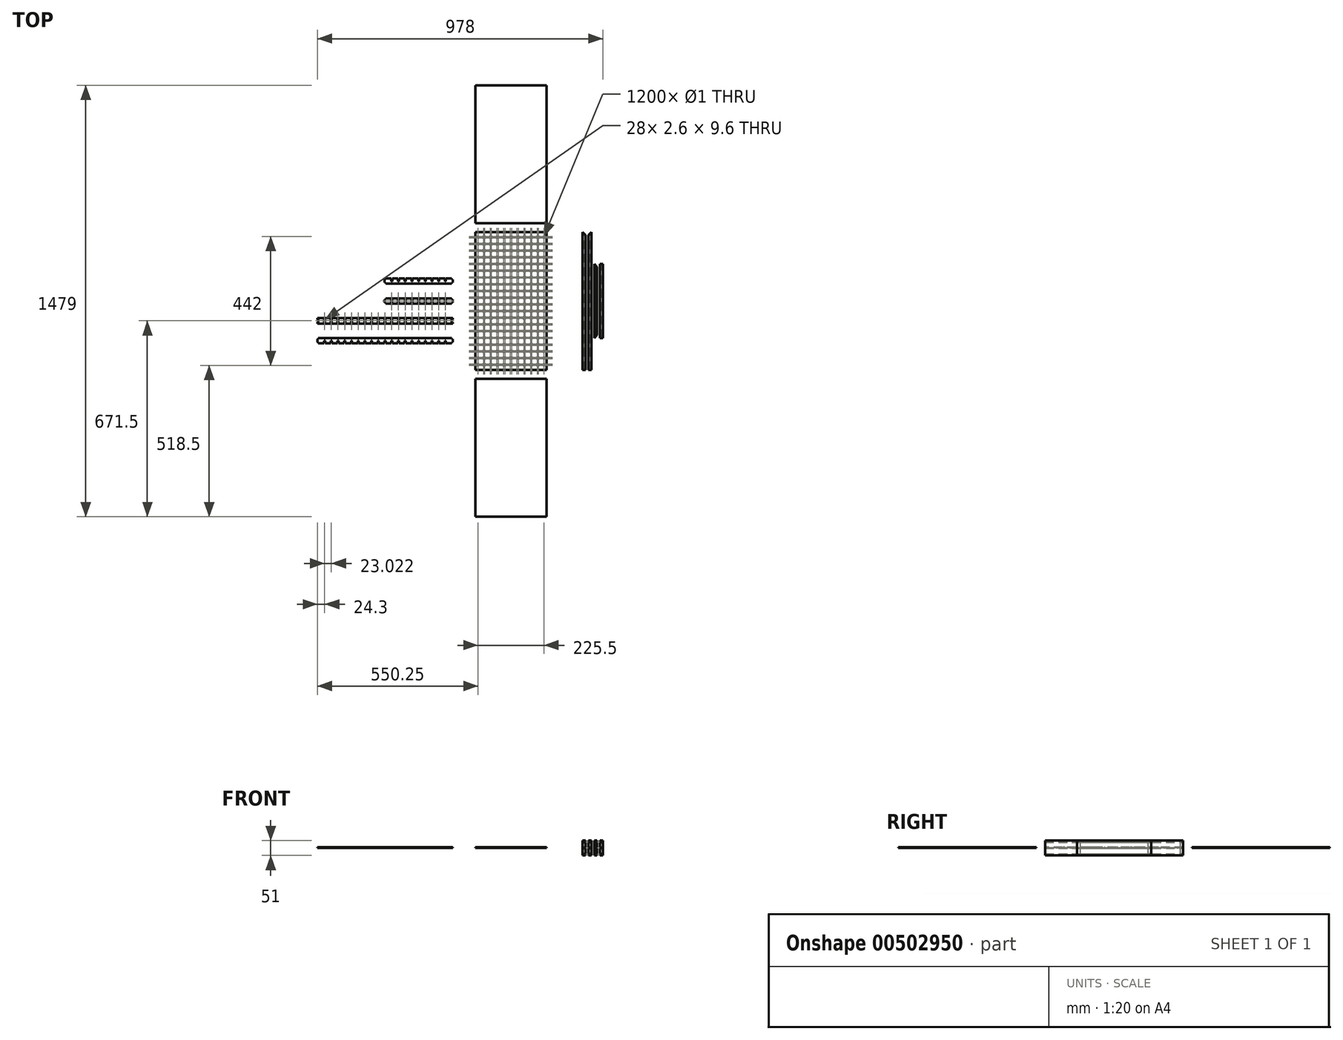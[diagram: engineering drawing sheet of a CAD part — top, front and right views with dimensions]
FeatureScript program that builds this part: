
annotation { "Feature Type Name" : "Feature", "Feature Type Description" : "" }
export const myFeature = defineFeature(function(context is Context, id is Id, definition is map)
    precondition{}
    {
        {
            assignVariable(context, id + "F0", {"name" : "Board_Size", "anyValue" : 10});
        }
        {
            assignVariable(context, id + "F1", {"name" : "Thickness", "anyValue" : 3});
        }
        {
            assignVariable(context, id + "F2", {"name" : "LED_Space", "anyValue" : 20});
        }
        {
            assignVariable(context, id + "F3", {"name" : "Gap_Fit", "anyValue" : 5});
        }
        {
            assignVariable(context, id + "F4", {"name" : "LED_Width", "anyValue" : (getVariable(context, 'Gap_Fit') * 2 + 10 * getVariable(context, 'LED_Space') + 11 * getVariable(context, 'Thickness'))});
        }
        {
            assignVariable(context, id + "F5", {"name" : "LED_Height", "anyValue" : (getVariable(context, 'Gap_Fit') * 2 + 20 * getVariable(context, 'LED_Space') + 21 * getVariable(context, 'Thickness'))});
        }
        {
            var Q0;
            Q0=qCreatedBy(makeId("Front.planeOp"),FACE);
            var sketch = newSketch(context, id + "F6", { "sketchPlane" : qUnion([Q0])});
            skLineSegment(sketch, "E0", {"start": v(5, 25.5) * mm, "end": v(-5, 25.5) * mm});
            skLineSegment(sketch, "E1", {"start": v(-5, 25.5) * mm, "end": v(-5, -25.5) * mm});
            skLineSegment(sketch, "E2", {"start": v(-5, -25.5) * mm, "end": v(5, -25.5) * mm});
            skLineSegment(sketch, "E3", {"start": v(5, -25.5) * mm, "end": v(5, -22.5) * mm});
            skLineSegment(sketch, "E4", {"start": v(5, -22.5) * mm, "end": v(0, -22.5) * mm});
            skLineSegment(sketch, "E5", {"start": v(0, -22.5) * mm, "end": v(0, -19.5) * mm});
            skLineSegment(sketch, "E6", {"start": v(0, -19.5) * mm, "end": v(5, -19.5) * mm});
            skLineSegment(sketch, "E7", {"start": v(5, -19.5) * mm, "end": v(5, -1.5) * mm});
            skLineSegment(sketch, "E8", {"start": v(5, -1.5) * mm, "end": v(0, -1.5) * mm});
            skLineSegment(sketch, "E9", {"start": v(0, -1.5) * mm, "end": v(0, 1.5) * mm});
            skLineSegment(sketch, "E10", {"start": v(0, 1.5) * mm, "end": v(5, 1.5) * mm});
            skLineSegment(sketch, "E11", {"start": v(5, 1.5) * mm, "end": v(5, 19.5) * mm});
            skLineSegment(sketch, "E12", {"start": v(5, 19.5) * mm, "end": v(0, 19.5) * mm});
            skLineSegment(sketch, "E13", {"start": v(0, 19.5) * mm, "end": v(0, 22.5) * mm});
            skLineSegment(sketch, "E14", {"start": v(0, 22.5) * mm, "end": v(5, 22.5) * mm});
            skLineSegment(sketch, "E15", {"start": v(5, 22.5) * mm, "end": v(5, 25.5) * mm});
            skSolve(sketch);
        }
        {
            var Q0;
            Q0=makeQuery(id+"F6.imprint","IMPRINT",FACE,{"disambiguationData":[TD([[makeQuery(id+"F6.imprint","IMPRINT",EDGE,{"derivedFrom":sQuery(id+"F6.wireOp",EDGE,"E0")}),1.0]])]});
            extrude(context, id + "F7", {"entities" : qUnion([Q0]), "endBound" : BoundingType.SYMMETRIC, "depth" : (getVariable(context, 'LED_Height')) * mm, "offsetDistance" : 25 * mm});
        }
        {
            var Q0;
            Q0=makeQuery(id+"F7.opExtrude","CAP_EDGE",EDGE,{"disambiguationData":[OSD([sQuery(id+"F6.wireOp",EDGE,"E11")])],"isStart":true});
            var Q1;
            Q1=makeQuery(id+"F7.opExtrude","CAP_EDGE",EDGE,{"disambiguationData":[OSD([sQuery(id+"F6.wireOp",EDGE,"E15")])],"isStart":true});
            var Q2;
            Q2=makeQuery(id+"F7.opExtrude","CAP_EDGE",EDGE,{"disambiguationData":[OSD([sQuery(id+"F6.wireOp",EDGE,"E7")])],"isStart":true});
            var Q3;
            Q3=makeQuery(id+"F7.opExtrude","CAP_EDGE",EDGE,{"disambiguationData":[OSD([sQuery(id+"F6.wireOp",EDGE,"E3")])],"isStart":true});
            chamfer(context, id + "F8", {"entities" : qUnion([Q0, Q1, Q2, Q3]), "width" : (getVariable(context, 'Board_Size')) * mm, "tangentPropagation" : true});
        }
        {
            var Q0;
            Q0=qCreatedBy(makeId("Front.planeOp"),FACE);
            var sketch = newSketch(context, id + "F9", { "sketchPlane" : qUnion([Q0])});
            skLineSegment(sketch, "E16", {"start": v(10, 50) * mm, "end": v(10, -50) * mm, "construction": true});
            skPoint(sketch, "E17", {"position": v(10, 0) * mm});
            skLineSegment(sketch, "E18", {"start": v(-5, 25.5) * mm, "end": v(5, 25.5) * mm, "construction": true});
            skLineSegment(sketch, "E19", {"start": v(5, 25.5) * mm, "end": v(5, 22.5) * mm, "construction": true});
            skLineSegment(sketch, "E20", {"start": v(5, 22.5) * mm, "end": v(0, 22.5) * mm, "construction": true});
            skLineSegment(sketch, "E21", {"start": v(0, 22.5) * mm, "end": v(0, 19.5) * mm, "construction": true});
            skLineSegment(sketch, "E22", {"start": v(0, 19.5) * mm, "end": v(5, 19.5) * mm, "construction": true});
            skLineSegment(sketch, "E23", {"start": v(5, 19.5) * mm, "end": v(5, 1.5) * mm, "construction": true});
            skLineSegment(sketch, "E24", {"start": v(5, -1.5) * mm, "end": v(5, -19.5) * mm, "construction": true});
            skLineSegment(sketch, "E25", {"start": v(5, 1.5) * mm, "end": v(0, 1.5) * mm, "construction": true});
            skLineSegment(sketch, "E26", {"start": v(0, 1.5) * mm, "end": v(0, -1.5) * mm, "construction": true});
            skLineSegment(sketch, "E27", {"start": v(0, -1.5) * mm, "end": v(5, -1.5) * mm, "construction": true});
            skLineSegment(sketch, "E28", {"start": v(0, -19.5) * mm, "end": v(0, -22.5) * mm, "construction": true});
            skLineSegment(sketch, "E29", {"start": v(5, -19.5) * mm, "end": v(0, -19.5) * mm, "construction": true});
            skLineSegment(sketch, "E30", {"start": v(0, -22.5) * mm, "end": v(5, -22.5) * mm, "construction": true});
            skLineSegment(sketch, "E31", {"start": v(5, -22.5) * mm, "end": v(5, -25.5) * mm, "construction": true});
            skLineSegment(sketch, "E32", {"start": v(5, -25.5) * mm, "end": v(-5, -25.5) * mm, "construction": true});
            skLineSegment(sketch, "E33", {"start": v(-5, -25.5) * mm, "end": v(-5, 25.5) * mm, "construction": true});
            skLineSegment(sketch, "E34.MirrorCS", {"start": v(15, 25.5) * mm, "end": v(15, 22.5) * mm});
            skLineSegment(sketch, "E35.MirrorCS", {"start": v(20, 22.5) * mm, "end": v(20, 19.5) * mm});
            skLineSegment(sketch, "E36.MirrorCS", {"start": v(20, 1.5) * mm, "end": v(20, -1.5) * mm});
            skLineSegment(sketch, "E37.MirrorCS", {"start": v(20, -19.5) * mm, "end": v(20, -22.5) * mm});
            skLineSegment(sketch, "E38.MirrorCS", {"start": v(15, -22.5) * mm, "end": v(15, -25.5) * mm});
            skLineSegment(sketch, "E39.MirrorCS", {"start": v(20, -22.5) * mm, "end": v(15, -22.5) * mm});
            skLineSegment(sketch, "E40.MirrorCS", {"start": v(15, 22.5) * mm, "end": v(20, 22.5) * mm});
            skLineSegment(sketch, "E41.MirrorCS", {"start": v(15, -25.5) * mm, "end": v(25, -25.5) * mm});
            skLineSegment(sketch, "E42.MirrorCS", {"start": v(15, 1.5) * mm, "end": v(20, 1.5) * mm});
            skLineSegment(sketch, "E43.MirrorCS", {"start": v(20, -1.5) * mm, "end": v(15, -1.5) * mm});
            skLineSegment(sketch, "E44.MirrorCS", {"start": v(15, -1.5) * mm, "end": v(15, -19.5) * mm});
            skLineSegment(sketch, "E45.MirrorCS", {"start": v(15, 19.5) * mm, "end": v(15, 1.5) * mm});
            skLineSegment(sketch, "E46.MirrorCS", {"start": v(15, -19.5) * mm, "end": v(20, -19.5) * mm});
            skLineSegment(sketch, "E47.MirrorCS", {"start": v(20, 19.5) * mm, "end": v(15, 19.5) * mm});
            skLineSegment(sketch, "E48.MirrorCS", {"start": v(25, -25.5) * mm, "end": v(25, 25.5) * mm});
            skLineSegment(sketch, "E49.MirrorCS", {"start": v(25, 25.5) * mm, "end": v(15, 25.5) * mm});
            skLineSegment(sketch, "E50", {"start": v(30, 50) * mm, "end": v(30, -50) * mm, "construction": true});
            skLineSegment(sketch, "E51.MirrorCS", {"start": v(45, -22.5) * mm, "end": v(45, -25.5) * mm});
            skLineSegment(sketch, "E52.MirrorCS", {"start": v(40, -19.5) * mm, "end": v(40, -22.5) * mm});
            skLineSegment(sketch, "E53.MirrorCS", {"start": v(45, -19.5) * mm, "end": v(40, -19.5) * mm});
            skLineSegment(sketch, "E54.MirrorCS", {"start": v(45, 1.5) * mm, "end": v(40, 1.5) * mm});
            skLineSegment(sketch, "E55.MirrorCS", {"start": v(35, 25.5) * mm, "end": v(45, 25.5) * mm});
            skLineSegment(sketch, "E56.MirrorCS", {"start": v(40, 1.5) * mm, "end": v(40, -1.5) * mm});
            skLineSegment(sketch, "E57.MirrorCS", {"start": v(40, 19.5) * mm, "end": v(45, 19.5) * mm});
            skLineSegment(sketch, "E58.MirrorCS", {"start": v(45, -25.5) * mm, "end": v(35, -25.5) * mm});
            skLineSegment(sketch, "E59.MirrorCS", {"start": v(40, 22.5) * mm, "end": v(40, 19.5) * mm});
            skLineSegment(sketch, "E60.MirrorCS", {"start": v(40, -1.5) * mm, "end": v(45, -1.5) * mm});
            skLineSegment(sketch, "E61.MirrorCS", {"start": v(40, -22.5) * mm, "end": v(45, -22.5) * mm});
            skLineSegment(sketch, "E62.MirrorCS", {"start": v(45, 22.5) * mm, "end": v(40, 22.5) * mm});
            skLineSegment(sketch, "E63.MirrorCS", {"start": v(45, 25.5) * mm, "end": v(45, 22.5) * mm});
            skLineSegment(sketch, "E64.MirrorCS", {"start": v(35, -25.5) * mm, "end": v(35, 25.5) * mm});
            skLineSegment(sketch, "E65.MirrorCS", {"start": v(45, -1.5) * mm, "end": v(45, -19.5) * mm});
            skLineSegment(sketch, "E66.MirrorCS", {"start": v(45, 19.5) * mm, "end": v(45, 1.5) * mm});
            skLineSegment(sketch, "E67.MirrorCS", {"start": v(55, -22.5) * mm, "end": v(55, -25.5) * mm});
            skLineSegment(sketch, "E68.MirrorCS", {"start": v(55, -19.5) * mm, "end": v(60, -19.5) * mm});
            skLineSegment(sketch, "E69.MirrorCS", {"start": v(60, 1.5) * mm, "end": v(60, -1.5) * mm});
            skLineSegment(sketch, "E70.MirrorCS", {"start": v(60, 19.5) * mm, "end": v(55, 19.5) * mm});
            skLineSegment(sketch, "E71.MirrorCS", {"start": v(60, 22.5) * mm, "end": v(60, 19.5) * mm});
            skLineSegment(sketch, "E72.MirrorCS", {"start": v(55, 22.5) * mm, "end": v(60, 22.5) * mm});
            skLineSegment(sketch, "E73.MirrorCS", {"start": v(55, 25.5) * mm, "end": v(55, 22.5) * mm});
            skLineSegment(sketch, "E74.MirrorCS", {"start": v(55, 1.5) * mm, "end": v(60, 1.5) * mm});
            skLineSegment(sketch, "E75.MirrorCS", {"start": v(60, -1.5) * mm, "end": v(55, -1.5) * mm});
            skLineSegment(sketch, "E76.MirrorCS", {"start": v(60, -19.5) * mm, "end": v(60, -22.5) * mm});
            skLineSegment(sketch, "E77.MirrorCS", {"start": v(60, -22.5) * mm, "end": v(55, -22.5) * mm});
            skLineSegment(sketch, "E78.MirrorCS", {"start": v(65, -25.5) * mm, "end": v(65, 25.5) * mm});
            skLineSegment(sketch, "E79.MirrorCS", {"start": v(55, 19.5) * mm, "end": v(55, 1.5) * mm});
            skLineSegment(sketch, "E80.MirrorCS", {"start": v(55, -25.5) * mm, "end": v(65, -25.5) * mm});
            skLineSegment(sketch, "E81.MirrorCS", {"start": v(55, -1.5) * mm, "end": v(55, -19.5) * mm});
            skLineSegment(sketch, "E82.MirrorCS", {"start": v(65, 25.5) * mm, "end": v(55, 25.5) * mm});
            skSolve(sketch);
        }
        {
            var Q0;
            Q0=makeQuery(id+"F9.imprint","IMPRINT",FACE,{"disambiguationData":[TD([[makeQuery(id+"F9.imprint","IMPRINT",EDGE,{"derivedFrom":sQuery(id+"F9.wireOp",EDGE,"E34.MirrorCS")}),1.0]])]});
            extrude(context, id + "F10", {"entities" : qUnion([Q0]), "endBound" : BoundingType.SYMMETRIC, "depth" : (getVariable(context, 'LED_Height')) * mm, "offsetDistance" : 25 * mm});
        }
        {
            var Q0;
            Q0=makeQuery(id+"F10.opExtrude","CAP_EDGE",EDGE,{"disambiguationData":[OSD([sQuery(id+"F9.wireOp",EDGE,"E44.MirrorCS")])],"isStart":true});
            var Q1;
            Q1=makeQuery(id+"F10.opExtrude","CAP_EDGE",EDGE,{"disambiguationData":[OSD([sQuery(id+"F9.wireOp",EDGE,"E38.MirrorCS")])],"isStart":true});
            var Q2;
            Q2=makeQuery(id+"F10.opExtrude","CAP_EDGE",EDGE,{"disambiguationData":[OSD([sQuery(id+"F9.wireOp",EDGE,"E45.MirrorCS")])],"isStart":true});
            var Q3;
            Q3=makeQuery(id+"F10.opExtrude","CAP_EDGE",EDGE,{"disambiguationData":[OSD([sQuery(id+"F9.wireOp",EDGE,"E34.MirrorCS")])],"isStart":true});
            chamfer(context, id + "F11", {"entities" : qUnion([Q0, Q1, Q2, Q3]), "width" : (getVariable(context, 'Board_Size')) * mm, "tangentPropagation" : true});
        }
        {
            var Q0;
            Q0=makeQuery(id+"F9.imprint","IMPRINT",FACE,{"disambiguationData":[TD([[makeQuery(id+"F9.imprint","IMPRINT",EDGE,{"derivedFrom":sQuery(id+"F9.wireOp",EDGE,"E51.MirrorCS")}),-1.0]])]});
            extrude(context, id + "F12", {"entities" : qUnion([Q0]), "endBound" : BoundingType.SYMMETRIC, "depth" : (getVariable(context, 'LED_Width') + 2 * getVariable(context, 'Gap_Fit')) * mm, "offsetDistance" : 25 * mm});
        }
        {
            var Q0;
            Q0=makeQuery(id+"F12.opExtrude","CAP_EDGE",EDGE,{"disambiguationData":[OSD([sQuery(id+"F9.wireOp",EDGE,"E63.MirrorCS")])],"isStart":false});
            var Q1;
            Q1=makeQuery(id+"F12.opExtrude","CAP_EDGE",EDGE,{"disambiguationData":[OSD([sQuery(id+"F9.wireOp",EDGE,"E66.MirrorCS")])],"isStart":false});
            var Q2;
            Q2=makeQuery(id+"F12.opExtrude","CAP_EDGE",EDGE,{"disambiguationData":[OSD([sQuery(id+"F9.wireOp",EDGE,"E65.MirrorCS")])],"isStart":false});
            var Q3;
            Q3=makeQuery(id+"F12.opExtrude","CAP_EDGE",EDGE,{"disambiguationData":[OSD([sQuery(id+"F9.wireOp",EDGE,"E51.MirrorCS")])],"isStart":false});
            var Q4;
            Q4=makeQuery(id+"F12.opExtrude","CAP_EDGE",EDGE,{"disambiguationData":[OSD([sQuery(id+"F9.wireOp",EDGE,"E63.MirrorCS")])],"isStart":true});
            var Q5;
            Q5=makeQuery(id+"F12.opExtrude","CAP_EDGE",EDGE,{"disambiguationData":[OSD([sQuery(id+"F9.wireOp",EDGE,"E66.MirrorCS")])],"isStart":true});
            var Q6;
            Q6=makeQuery(id+"F12.opExtrude","CAP_EDGE",EDGE,{"disambiguationData":[OSD([sQuery(id+"F9.wireOp",EDGE,"E65.MirrorCS")])],"isStart":true});
            var Q7;
            Q7=makeQuery(id+"F12.opExtrude","CAP_EDGE",EDGE,{"disambiguationData":[OSD([sQuery(id+"F9.wireOp",EDGE,"E51.MirrorCS")])],"isStart":true});
            chamfer(context, id + "F13", {"entities" : qUnion([Q0, Q1, Q2, Q3, Q4, Q5, Q6, Q7]), "width" : (getVariable(context, 'Board_Size')) * mm, "tangentPropagation" : true});
        }
        {
            var Q0;
            Q0=makeQuery(id+"F9.imprint","IMPRINT",FACE,{"disambiguationData":[TD([[makeQuery(id+"F9.imprint","IMPRINT",EDGE,{"derivedFrom":sQuery(id+"F9.wireOp",EDGE,"E67.MirrorCS")}),1.0]])]});
            extrude(context, id + "F14", {"entities" : qUnion([Q0]), "endBound" : BoundingType.SYMMETRIC, "depth" : (getVariable(context, 'LED_Width') + getVariable(context, 'Board_Size')) * mm, "offsetDistance" : 25 * mm});
        }
        {
            var Q0;
            Q0=qCreatedBy(makeId("Top.planeOp"),FACE);
            var sketch = newSketch(context, id + "F15", { "sketchPlane" : qUnion([Q0])});
            skLineSegment(sketch, "E83.bottom", {"start": v(-128.5, 236.5) * mm, "end": v(-371.5, 236.5) * mm});
            skLineSegment(sketch, "E83.top", {"start": v(-128.5, -236.5) * mm, "end": v(-371.5, -236.5) * mm});
            skLineSegment(sketch, "E83.left", {"start": v(-128.5, 236.5) * mm, "end": v(-128.5, -236.5) * mm});
            skLineSegment(sketch, "E83.right", {"start": v(-371.5, 236.5) * mm, "end": v(-371.5, -236.5) * mm});
            skPoint(sketch, "E83.middle", {"position": v(-250, 0) * mm});
            skLineSegment(sketch, "E84.bottom", {"start": v(-371.5, 266.5) * mm, "end": v(-128.5, 266.5) * mm});
            skLineSegment(sketch, "E84.top", {"start": v(-371.5, 739.5) * mm, "end": v(-128.5, 739.5) * mm});
            skLineSegment(sketch, "E84.left", {"start": v(-371.5, 266.5) * mm, "end": v(-371.5, 739.5) * mm});
            skLineSegment(sketch, "E84.right", {"start": v(-128.5, 266.5) * mm, "end": v(-128.5, 739.5) * mm});
            skLineSegment(sketch, "E85.bottom", {"start": v(-128.5, -266.5) * mm, "end": v(-371.5, -266.5) * mm});
            skLineSegment(sketch, "E85.top", {"start": v(-128.5, -739.5) * mm, "end": v(-371.5, -739.5) * mm});
            skLineSegment(sketch, "E85.left", {"start": v(-128.5, -266.5) * mm, "end": v(-128.5, -739.5) * mm});
            skLineSegment(sketch, "E85.right", {"start": v(-371.5, -266.5) * mm, "end": v(-371.5, -739.5) * mm});
            skLineSegment(sketch, "E86", {"start": v(-335.5, 236.5) * mm, "end": v(-335.5, 200.5) * mm, "construction": true});
            skLineSegment(sketch, "E87", {"start": v(-335.5, 200.5) * mm, "end": v(-371.5, 200.5) * mm, "construction": true});
            skCircle(sketch, "E88", {"center": v(-362.75, 221) * mm, "radius": 0.5 * mm});
            skCircle(sketch, "E89", {"center": v(-362.75, 218.5) * mm, "radius": 0.5 * mm});
            skCircle(sketch, "E90", {"center": v(-362.75, 216) * mm, "radius": 0.5 * mm});
            skCircle(sketch, "E91", {"center": v(-344.25, 221) * mm, "radius": 0.5 * mm});
            skCircle(sketch, "E92", {"center": v(-344.25, 218.5) * mm, "radius": 0.5 * mm});
            skCircle(sketch, "E93", {"center": v(-344.25, 216) * mm, "radius": 0.5 * mm});
            skLineSegment(sketch, "E94.bottom", {"start": v(-345, 223.5) * mm, "end": v(-362, 223.5) * mm, "construction": true});
            skLineSegment(sketch, "E94.top", {"start": v(-345, 213.5) * mm, "end": v(-362, 213.5) * mm, "construction": true});
            skLineSegment(sketch, "E94.left", {"start": v(-345, 223.5) * mm, "end": v(-345, 213.5) * mm, "construction": true});
            skLineSegment(sketch, "E94.right", {"start": v(-362, 223.5) * mm, "end": v(-362, 213.5) * mm, "construction": true});
            skPoint(sketch, "E94.middle", {"position": v(-353.5, 218.5) * mm});
            skPoint(sketch, "E94.middle.positionSnap0", {"position": v(-353.5, 200.5) * mm});
            skPoint(sketch, "E94.middle.positionSnap1", {"position": v(-335.5, 218.5) * mm});
            skPoint(sketch, "E94.centerSnap0", {"position": v(-353.5, 200.5) * mm});
            skPoint(sketch, "E94.centerSnap1", {"position": v(-335.5, 218.5) * mm});
            skCircle(sketch, "E95.1.0.0", {"center": v(-339.75, 216) * mm, "radius": 0.5 * mm});
            skCircle(sketch, "E95.1.0.1", {"center": v(-339.75, 221) * mm, "radius": 0.5 * mm});
            skCircle(sketch, "E95.1.0.2", {"center": v(-339.75, 218.5) * mm, "radius": 0.5 * mm});
            skCircle(sketch, "E95.1.0.3", {"center": v(-321.25, 221) * mm, "radius": 0.5 * mm});
            skCircle(sketch, "E95.1.0.4", {"center": v(-321.25, 216) * mm, "radius": 0.5 * mm});
            skCircle(sketch, "E95.1.0.5", {"center": v(-321.25, 218.5) * mm, "radius": 0.5 * mm});
            skCircle(sketch, "E95.2.0.0", {"center": v(-316.75, 216) * mm, "radius": 0.5 * mm});
            skCircle(sketch, "E95.2.0.1", {"center": v(-316.75, 221) * mm, "radius": 0.5 * mm});
            skCircle(sketch, "E95.2.0.2", {"center": v(-316.75, 218.5) * mm, "radius": 0.5 * mm});
            skCircle(sketch, "E95.2.0.3", {"center": v(-298.25, 221) * mm, "radius": 0.5 * mm});
            skCircle(sketch, "E95.2.0.4", {"center": v(-298.25, 216) * mm, "radius": 0.5 * mm});
            skCircle(sketch, "E95.2.0.5", {"center": v(-298.25, 218.5) * mm, "radius": 0.5 * mm});
            skCircle(sketch, "E95.3.0.0", {"center": v(-293.75, 216) * mm, "radius": 0.5 * mm});
            skCircle(sketch, "E95.3.0.1", {"center": v(-293.75, 221) * mm, "radius": 0.5 * mm});
            skCircle(sketch, "E95.3.0.2", {"center": v(-293.75, 218.5) * mm, "radius": 0.5 * mm});
            skCircle(sketch, "E95.3.0.3", {"center": v(-275.25, 221) * mm, "radius": 0.5 * mm});
            skCircle(sketch, "E95.3.0.4", {"center": v(-275.25, 216) * mm, "radius": 0.5 * mm});
            skCircle(sketch, "E95.3.0.5", {"center": v(-275.25, 218.5) * mm, "radius": 0.5 * mm});
            skCircle(sketch, "E95.4.0.0", {"center": v(-270.75, 216) * mm, "radius": 0.5 * mm});
            skCircle(sketch, "E95.4.0.1", {"center": v(-270.75, 221) * mm, "radius": 0.5 * mm});
            skCircle(sketch, "E95.4.0.2", {"center": v(-270.75, 218.5) * mm, "radius": 0.5 * mm});
            skCircle(sketch, "E95.4.0.3", {"center": v(-252.25, 221) * mm, "radius": 0.5 * mm});
            skCircle(sketch, "E95.4.0.4", {"center": v(-252.25, 216) * mm, "radius": 0.5 * mm});
            skCircle(sketch, "E95.4.0.5", {"center": v(-252.25, 218.5) * mm, "radius": 0.5 * mm});
            skCircle(sketch, "E95.5.0.0", {"center": v(-247.75, 216) * mm, "radius": 0.5 * mm});
            skCircle(sketch, "E95.5.0.1", {"center": v(-247.75, 221) * mm, "radius": 0.5 * mm});
            skCircle(sketch, "E95.5.0.2", {"center": v(-247.75, 218.5) * mm, "radius": 0.5 * mm});
            skCircle(sketch, "E95.5.0.3", {"center": v(-229.25, 221) * mm, "radius": 0.5 * mm});
            skCircle(sketch, "E95.5.0.4", {"center": v(-229.25, 216) * mm, "radius": 0.5 * mm});
            skCircle(sketch, "E95.5.0.5", {"center": v(-229.25, 218.5) * mm, "radius": 0.5 * mm});
            skCircle(sketch, "E95.6.0.0", {"center": v(-224.75, 216) * mm, "radius": 0.5 * mm});
            skCircle(sketch, "E95.6.0.1", {"center": v(-224.75, 221) * mm, "radius": 0.5 * mm});
            skCircle(sketch, "E95.6.0.2", {"center": v(-224.75, 218.5) * mm, "radius": 0.5 * mm});
            skCircle(sketch, "E95.6.0.3", {"center": v(-206.25, 221) * mm, "radius": 0.5 * mm});
            skCircle(sketch, "E95.6.0.4", {"center": v(-206.25, 216) * mm, "radius": 0.5 * mm});
            skCircle(sketch, "E95.6.0.5", {"center": v(-206.25, 218.5) * mm, "radius": 0.5 * mm});
            skCircle(sketch, "E95.7.0.0", {"center": v(-201.75, 216) * mm, "radius": 0.5 * mm});
            skCircle(sketch, "E95.7.0.1", {"center": v(-201.75, 221) * mm, "radius": 0.5 * mm});
            skCircle(sketch, "E95.7.0.2", {"center": v(-201.75, 218.5) * mm, "radius": 0.5 * mm});
            skCircle(sketch, "E95.7.0.3", {"center": v(-183.25, 221) * mm, "radius": 0.5 * mm});
            skCircle(sketch, "E95.7.0.4", {"center": v(-183.25, 216) * mm, "radius": 0.5 * mm});
            skCircle(sketch, "E95.7.0.5", {"center": v(-183.25, 218.5) * mm, "radius": 0.5 * mm});
            skCircle(sketch, "E95.8.0.0", {"center": v(-178.75, 216) * mm, "radius": 0.5 * mm});
            skCircle(sketch, "E95.8.0.1", {"center": v(-178.75, 221) * mm, "radius": 0.5 * mm});
            skCircle(sketch, "E95.8.0.2", {"center": v(-178.75, 218.5) * mm, "radius": 0.5 * mm});
            skCircle(sketch, "E95.8.0.3", {"center": v(-160.25, 221) * mm, "radius": 0.5 * mm});
            skCircle(sketch, "E95.8.0.4", {"center": v(-160.25, 216) * mm, "radius": 0.5 * mm});
            skCircle(sketch, "E95.8.0.5", {"center": v(-160.25, 218.5) * mm, "radius": 0.5 * mm});
            skCircle(sketch, "E95.9.0.0", {"center": v(-155.75, 216) * mm, "radius": 0.5 * mm});
            skCircle(sketch, "E95.9.0.1", {"center": v(-155.75, 221) * mm, "radius": 0.5 * mm});
            skCircle(sketch, "E95.9.0.2", {"center": v(-155.75, 218.5) * mm, "radius": 0.5 * mm});
            skCircle(sketch, "E95.9.0.3", {"center": v(-137.25, 221) * mm, "radius": 0.5 * mm});
            skCircle(sketch, "E95.9.0.4", {"center": v(-137.25, 216) * mm, "radius": 0.5 * mm});
            skCircle(sketch, "E95.9.0.5", {"center": v(-137.25, 218.5) * mm, "radius": 0.5 * mm});
            skLineSegment(sketch, "E95.direction1", {"start": v(-362.75, 216) * mm, "end": v(-339.75, 216) * mm, "construction": true});
            skCircle(sketch, "E96.1.0.0", {"center": v(-224.75, 193) * mm, "radius": 0.5 * mm});
            skCircle(sketch, "E96.1.0.1", {"center": v(-206.25, 195.5) * mm, "radius": 0.5 * mm});
            skCircle(sketch, "E96.1.0.2", {"center": v(-270.75, 193) * mm, "radius": 0.5 * mm});
            skCircle(sketch, "E96.1.0.3", {"center": v(-252.25, 193) * mm, "radius": 0.5 * mm});
            skCircle(sketch, "E96.1.0.4", {"center": v(-183.25, 198) * mm, "radius": 0.5 * mm});
            skCircle(sketch, "E96.1.0.5", {"center": v(-137.25, 193) * mm, "radius": 0.5 * mm});
            skCircle(sketch, "E96.1.0.6", {"center": v(-224.75, 195.5) * mm, "radius": 0.5 * mm});
            skCircle(sketch, "E96.1.0.7", {"center": v(-321.25, 193) * mm, "radius": 0.5 * mm});
            skCircle(sketch, "E96.1.0.8", {"center": v(-275.25, 193) * mm, "radius": 0.5 * mm});
            skCircle(sketch, "E96.1.0.9", {"center": v(-155.75, 193) * mm, "radius": 0.5 * mm});
            skCircle(sketch, "E96.1.0.10", {"center": v(-298.25, 193) * mm, "radius": 0.5 * mm});
            skCircle(sketch, "E96.1.0.11", {"center": v(-270.75, 195.5) * mm, "radius": 0.5 * mm});
            skCircle(sketch, "E96.1.0.12", {"center": v(-206.25, 198) * mm, "radius": 0.5 * mm});
            skCircle(sketch, "E96.1.0.13", {"center": v(-201.75, 193) * mm, "radius": 0.5 * mm});
            skCircle(sketch, "E96.1.0.14", {"center": v(-275.25, 195.5) * mm, "radius": 0.5 * mm});
            skCircle(sketch, "E96.1.0.15", {"center": v(-270.75, 198) * mm, "radius": 0.5 * mm});
            skCircle(sketch, "E96.1.0.16", {"center": v(-178.75, 198) * mm, "radius": 0.5 * mm});
            skCircle(sketch, "E96.1.0.17", {"center": v(-137.25, 198) * mm, "radius": 0.5 * mm});
            skCircle(sketch, "E96.1.0.18", {"center": v(-321.25, 198) * mm, "radius": 0.5 * mm});
            skCircle(sketch, "E96.1.0.19", {"center": v(-183.25, 193) * mm, "radius": 0.5 * mm});
            skCircle(sketch, "E96.1.0.20", {"center": v(-293.75, 195.5) * mm, "radius": 0.5 * mm});
            skCircle(sketch, "E96.1.0.21", {"center": v(-224.75, 198) * mm, "radius": 0.5 * mm});
            skCircle(sketch, "E96.1.0.22", {"center": v(-229.25, 198) * mm, "radius": 0.5 * mm});
            skCircle(sketch, "E96.1.0.23", {"center": v(-321.25, 195.5) * mm, "radius": 0.5 * mm});
            skCircle(sketch, "E96.1.0.24", {"center": v(-293.75, 193) * mm, "radius": 0.5 * mm});
            skCircle(sketch, "E96.1.0.25", {"center": v(-160.25, 198) * mm, "radius": 0.5 * mm});
            skCircle(sketch, "E96.1.0.26", {"center": v(-183.25, 195.5) * mm, "radius": 0.5 * mm});
            skCircle(sketch, "E96.1.0.27", {"center": v(-252.25, 195.5) * mm, "radius": 0.5 * mm});
            skCircle(sketch, "E96.1.0.28", {"center": v(-155.75, 195.5) * mm, "radius": 0.5 * mm});
            skCircle(sketch, "E96.1.0.29", {"center": v(-206.25, 193) * mm, "radius": 0.5 * mm});
            skCircle(sketch, "E96.1.0.30", {"center": v(-178.75, 195.5) * mm, "radius": 0.5 * mm});
            skCircle(sketch, "E96.1.0.31", {"center": v(-155.75, 198) * mm, "radius": 0.5 * mm});
            skCircle(sketch, "E96.1.0.32", {"center": v(-178.75, 193) * mm, "radius": 0.5 * mm});
            skCircle(sketch, "E96.1.0.33", {"center": v(-247.75, 195.5) * mm, "radius": 0.5 * mm});
            skCircle(sketch, "E96.1.0.34", {"center": v(-316.75, 193) * mm, "radius": 0.5 * mm});
            skCircle(sketch, "E96.1.0.35", {"center": v(-316.75, 198) * mm, "radius": 0.5 * mm});
            skCircle(sketch, "E96.1.0.36", {"center": v(-293.75, 198) * mm, "radius": 0.5 * mm});
            skCircle(sketch, "E96.1.0.37", {"center": v(-316.75, 195.5) * mm, "radius": 0.5 * mm});
            skCircle(sketch, "E96.1.0.38", {"center": v(-247.75, 193) * mm, "radius": 0.5 * mm});
            skCircle(sketch, "E96.1.0.39", {"center": v(-275.25, 198) * mm, "radius": 0.5 * mm});
            skCircle(sketch, "E96.1.0.40", {"center": v(-229.25, 195.5) * mm, "radius": 0.5 * mm});
            skCircle(sketch, "E96.1.0.41", {"center": v(-160.25, 193) * mm, "radius": 0.5 * mm});
            skCircle(sketch, "E96.1.0.42", {"center": v(-229.25, 193) * mm, "radius": 0.5 * mm});
            skCircle(sketch, "E96.1.0.43", {"center": v(-252.25, 198) * mm, "radius": 0.5 * mm});
            skCircle(sketch, "E96.1.0.44", {"center": v(-247.75, 198) * mm, "radius": 0.5 * mm});
            skCircle(sketch, "E96.1.0.45", {"center": v(-137.25, 195.5) * mm, "radius": 0.5 * mm});
            skCircle(sketch, "E96.1.0.46", {"center": v(-201.75, 198) * mm, "radius": 0.5 * mm});
            skCircle(sketch, "E96.1.0.47", {"center": v(-298.25, 198) * mm, "radius": 0.5 * mm});
            skCircle(sketch, "E96.1.0.48", {"center": v(-298.25, 195.5) * mm, "radius": 0.5 * mm});
            skCircle(sketch, "E96.1.0.49", {"center": v(-201.75, 195.5) * mm, "radius": 0.5 * mm});
            skCircle(sketch, "E96.1.0.50", {"center": v(-160.25, 195.5) * mm, "radius": 0.5 * mm});
            skCircle(sketch, "E96.1.0.51", {"center": v(-344.25, 193) * mm, "radius": 0.5 * mm});
            skCircle(sketch, "E96.1.0.52", {"center": v(-339.75, 193) * mm, "radius": 0.5 * mm});
            skCircle(sketch, "E96.1.0.53", {"center": v(-339.75, 198) * mm, "radius": 0.5 * mm});
            skCircle(sketch, "E96.1.0.54", {"center": v(-344.25, 195.5) * mm, "radius": 0.5 * mm});
            skCircle(sketch, "E96.1.0.55", {"center": v(-344.25, 198) * mm, "radius": 0.5 * mm});
            skCircle(sketch, "E96.1.0.56", {"center": v(-339.75, 195.5) * mm, "radius": 0.5 * mm});
            skCircle(sketch, "E96.1.0.57", {"center": v(-362.75, 193) * mm, "radius": 0.5 * mm});
            skCircle(sketch, "E96.1.0.58", {"center": v(-362.75, 198) * mm, "radius": 0.5 * mm});
            skCircle(sketch, "E96.1.0.59", {"center": v(-362.75, 195.5) * mm, "radius": 0.5 * mm});
            skCircle(sketch, "E96.2.0.0", {"center": v(-224.75, 170) * mm, "radius": 0.5 * mm});
            skCircle(sketch, "E96.2.0.1", {"center": v(-206.25, 172.5) * mm, "radius": 0.5 * mm});
            skCircle(sketch, "E96.2.0.2", {"center": v(-270.75, 170) * mm, "radius": 0.5 * mm});
            skCircle(sketch, "E96.2.0.3", {"center": v(-252.25, 170) * mm, "radius": 0.5 * mm});
            skCircle(sketch, "E96.2.0.4", {"center": v(-183.25, 175) * mm, "radius": 0.5 * mm});
            skCircle(sketch, "E96.2.0.5", {"center": v(-137.25, 170) * mm, "radius": 0.5 * mm});
            skCircle(sketch, "E96.2.0.6", {"center": v(-224.75, 172.5) * mm, "radius": 0.5 * mm});
            skCircle(sketch, "E96.2.0.7", {"center": v(-321.25, 170) * mm, "radius": 0.5 * mm});
            skCircle(sketch, "E96.2.0.8", {"center": v(-275.25, 170) * mm, "radius": 0.5 * mm});
            skCircle(sketch, "E96.2.0.9", {"center": v(-155.75, 170) * mm, "radius": 0.5 * mm});
            skCircle(sketch, "E96.2.0.10", {"center": v(-298.25, 170) * mm, "radius": 0.5 * mm});
            skCircle(sketch, "E96.2.0.11", {"center": v(-270.75, 172.5) * mm, "radius": 0.5 * mm});
            skCircle(sketch, "E96.2.0.12", {"center": v(-206.25, 175) * mm, "radius": 0.5 * mm});
            skCircle(sketch, "E96.2.0.13", {"center": v(-201.75, 170) * mm, "radius": 0.5 * mm});
            skCircle(sketch, "E96.2.0.14", {"center": v(-275.25, 172.5) * mm, "radius": 0.5 * mm});
            skCircle(sketch, "E96.2.0.15", {"center": v(-270.75, 175) * mm, "radius": 0.5 * mm});
            skCircle(sketch, "E96.2.0.16", {"center": v(-178.75, 175) * mm, "radius": 0.5 * mm});
            skCircle(sketch, "E96.2.0.17", {"center": v(-137.25, 175) * mm, "radius": 0.5 * mm});
            skCircle(sketch, "E96.2.0.18", {"center": v(-321.25, 175) * mm, "radius": 0.5 * mm});
            skCircle(sketch, "E96.2.0.19", {"center": v(-183.25, 170) * mm, "radius": 0.5 * mm});
            skCircle(sketch, "E96.2.0.20", {"center": v(-293.75, 172.5) * mm, "radius": 0.5 * mm});
            skCircle(sketch, "E96.2.0.21", {"center": v(-224.75, 175) * mm, "radius": 0.5 * mm});
            skCircle(sketch, "E96.2.0.22", {"center": v(-229.25, 175) * mm, "radius": 0.5 * mm});
            skCircle(sketch, "E96.2.0.23", {"center": v(-321.25, 172.5) * mm, "radius": 0.5 * mm});
            skCircle(sketch, "E96.2.0.24", {"center": v(-293.75, 170) * mm, "radius": 0.5 * mm});
            skCircle(sketch, "E96.2.0.25", {"center": v(-160.25, 175) * mm, "radius": 0.5 * mm});
            skCircle(sketch, "E96.2.0.26", {"center": v(-183.25, 172.5) * mm, "radius": 0.5 * mm});
            skCircle(sketch, "E96.2.0.27", {"center": v(-252.25, 172.5) * mm, "radius": 0.5 * mm});
            skCircle(sketch, "E96.2.0.28", {"center": v(-155.75, 172.5) * mm, "radius": 0.5 * mm});
            skCircle(sketch, "E96.2.0.29", {"center": v(-206.25, 170) * mm, "radius": 0.5 * mm});
            skCircle(sketch, "E96.2.0.30", {"center": v(-178.75, 172.5) * mm, "radius": 0.5 * mm});
            skCircle(sketch, "E96.2.0.31", {"center": v(-155.75, 175) * mm, "radius": 0.5 * mm});
            skCircle(sketch, "E96.2.0.32", {"center": v(-178.75, 170) * mm, "radius": 0.5 * mm});
            skCircle(sketch, "E96.2.0.33", {"center": v(-247.75, 172.5) * mm, "radius": 0.5 * mm});
            skCircle(sketch, "E96.2.0.34", {"center": v(-316.75, 170) * mm, "radius": 0.5 * mm});
            skCircle(sketch, "E96.2.0.35", {"center": v(-316.75, 175) * mm, "radius": 0.5 * mm});
            skCircle(sketch, "E96.2.0.36", {"center": v(-293.75, 175) * mm, "radius": 0.5 * mm});
            skCircle(sketch, "E96.2.0.37", {"center": v(-316.75, 172.5) * mm, "radius": 0.5 * mm});
            skCircle(sketch, "E96.2.0.38", {"center": v(-247.75, 170) * mm, "radius": 0.5 * mm});
            skCircle(sketch, "E96.2.0.39", {"center": v(-275.25, 175) * mm, "radius": 0.5 * mm});
            skCircle(sketch, "E96.2.0.40", {"center": v(-229.25, 172.5) * mm, "radius": 0.5 * mm});
            skCircle(sketch, "E96.2.0.41", {"center": v(-160.25, 170) * mm, "radius": 0.5 * mm});
            skCircle(sketch, "E96.2.0.42", {"center": v(-229.25, 170) * mm, "radius": 0.5 * mm});
            skCircle(sketch, "E96.2.0.43", {"center": v(-252.25, 175) * mm, "radius": 0.5 * mm});
            skCircle(sketch, "E96.2.0.44", {"center": v(-247.75, 175) * mm, "radius": 0.5 * mm});
            skCircle(sketch, "E96.2.0.45", {"center": v(-137.25, 172.5) * mm, "radius": 0.5 * mm});
            skCircle(sketch, "E96.2.0.46", {"center": v(-201.75, 175) * mm, "radius": 0.5 * mm});
            skCircle(sketch, "E96.2.0.47", {"center": v(-298.25, 175) * mm, "radius": 0.5 * mm});
            skCircle(sketch, "E96.2.0.48", {"center": v(-298.25, 172.5) * mm, "radius": 0.5 * mm});
            skCircle(sketch, "E96.2.0.49", {"center": v(-201.75, 172.5) * mm, "radius": 0.5 * mm});
            skCircle(sketch, "E96.2.0.50", {"center": v(-160.25, 172.5) * mm, "radius": 0.5 * mm});
            skCircle(sketch, "E96.2.0.51", {"center": v(-344.25, 170) * mm, "radius": 0.5 * mm});
            skCircle(sketch, "E96.2.0.52", {"center": v(-339.75, 170) * mm, "radius": 0.5 * mm});
            skCircle(sketch, "E96.2.0.53", {"center": v(-339.75, 175) * mm, "radius": 0.5 * mm});
            skCircle(sketch, "E96.2.0.54", {"center": v(-344.25, 172.5) * mm, "radius": 0.5 * mm});
            skCircle(sketch, "E96.2.0.55", {"center": v(-344.25, 175) * mm, "radius": 0.5 * mm});
            skCircle(sketch, "E96.2.0.56", {"center": v(-339.75, 172.5) * mm, "radius": 0.5 * mm});
            skCircle(sketch, "E96.2.0.57", {"center": v(-362.75, 170) * mm, "radius": 0.5 * mm});
            skCircle(sketch, "E96.2.0.58", {"center": v(-362.75, 175) * mm, "radius": 0.5 * mm});
            skCircle(sketch, "E96.2.0.59", {"center": v(-362.75, 172.5) * mm, "radius": 0.5 * mm});
            skLineSegment(sketch, "E96.direction1", {"start": v(-362.75, 216) * mm, "end": v(-362.75, 193) * mm, "construction": true});
            skCircle(sketch, "E97.0.3.0", {"center": v(-224.75, 147) * mm, "radius": 0.5 * mm});
            skCircle(sketch, "E97.2.3.0", {"center": v(-206.25, 149.5) * mm, "radius": 0.5 * mm});
            skCircle(sketch, "E97.4.3.0", {"center": v(-270.75, 147) * mm, "radius": 0.5 * mm});
            skCircle(sketch, "E97.6.3.0", {"center": v(-252.25, 147) * mm, "radius": 0.5 * mm});
            skCircle(sketch, "E97.8.3.0", {"center": v(-183.25, 152) * mm, "radius": 0.5 * mm});
            skCircle(sketch, "E97.10.3.0", {"center": v(-137.25, 147) * mm, "radius": 0.5 * mm});
            skCircle(sketch, "E97.12.3.0", {"center": v(-224.75, 149.5) * mm, "radius": 0.5 * mm});
            skCircle(sketch, "E97.14.3.0", {"center": v(-321.25, 147) * mm, "radius": 0.5 * mm});
            skCircle(sketch, "E97.16.3.0", {"center": v(-275.25, 147) * mm, "radius": 0.5 * mm});
            skCircle(sketch, "E97.18.3.0", {"center": v(-155.75, 147) * mm, "radius": 0.5 * mm});
            skCircle(sketch, "E97.20.3.0", {"center": v(-298.25, 147) * mm, "radius": 0.5 * mm});
            skCircle(sketch, "E97.22.3.0", {"center": v(-270.75, 149.5) * mm, "radius": 0.5 * mm});
            skCircle(sketch, "E97.24.3.0", {"center": v(-206.25, 152) * mm, "radius": 0.5 * mm});
            skCircle(sketch, "E97.26.3.0", {"center": v(-201.75, 147) * mm, "radius": 0.5 * mm});
            skCircle(sketch, "E97.28.3.0", {"center": v(-275.25, 149.5) * mm, "radius": 0.5 * mm});
            skCircle(sketch, "E97.30.3.0", {"center": v(-270.75, 152) * mm, "radius": 0.5 * mm});
            skCircle(sketch, "E97.32.3.0", {"center": v(-178.75, 152) * mm, "radius": 0.5 * mm});
            skCircle(sketch, "E97.34.3.0", {"center": v(-137.25, 152) * mm, "radius": 0.5 * mm});
            skCircle(sketch, "E97.36.3.0", {"center": v(-321.25, 152) * mm, "radius": 0.5 * mm});
            skCircle(sketch, "E97.38.3.0", {"center": v(-183.25, 147) * mm, "radius": 0.5 * mm});
            skCircle(sketch, "E97.40.3.0", {"center": v(-293.75, 149.5) * mm, "radius": 0.5 * mm});
            skCircle(sketch, "E97.42.3.0", {"center": v(-224.75, 152) * mm, "radius": 0.5 * mm});
            skCircle(sketch, "E97.44.3.0", {"center": v(-229.25, 152) * mm, "radius": 0.5 * mm});
            skCircle(sketch, "E97.46.3.0", {"center": v(-321.25, 149.5) * mm, "radius": 0.5 * mm});
            skCircle(sketch, "E97.48.3.0", {"center": v(-293.75, 147) * mm, "radius": 0.5 * mm});
            skCircle(sketch, "E97.50.3.0", {"center": v(-160.25, 152) * mm, "radius": 0.5 * mm});
            skCircle(sketch, "E97.52.3.0", {"center": v(-183.25, 149.5) * mm, "radius": 0.5 * mm});
            skCircle(sketch, "E97.54.3.0", {"center": v(-252.25, 149.5) * mm, "radius": 0.5 * mm});
            skCircle(sketch, "E97.56.3.0", {"center": v(-155.75, 149.5) * mm, "radius": 0.5 * mm});
            skCircle(sketch, "E97.58.3.0", {"center": v(-206.25, 147) * mm, "radius": 0.5 * mm});
            skCircle(sketch, "E97.60.3.0", {"center": v(-178.75, 149.5) * mm, "radius": 0.5 * mm});
            skCircle(sketch, "E97.62.3.0", {"center": v(-155.75, 152) * mm, "radius": 0.5 * mm});
            skCircle(sketch, "E97.64.3.0", {"center": v(-178.75, 147) * mm, "radius": 0.5 * mm});
            skCircle(sketch, "E97.66.3.0", {"center": v(-247.75, 149.5) * mm, "radius": 0.5 * mm});
            skCircle(sketch, "E97.68.3.0", {"center": v(-316.75, 147) * mm, "radius": 0.5 * mm});
            skCircle(sketch, "E97.70.3.0", {"center": v(-316.75, 152) * mm, "radius": 0.5 * mm});
            skCircle(sketch, "E97.72.3.0", {"center": v(-293.75, 152) * mm, "radius": 0.5 * mm});
            skCircle(sketch, "E97.74.3.0", {"center": v(-316.75, 149.5) * mm, "radius": 0.5 * mm});
            skCircle(sketch, "E97.76.3.0", {"center": v(-247.75, 147) * mm, "radius": 0.5 * mm});
            skCircle(sketch, "E97.78.3.0", {"center": v(-275.25, 152) * mm, "radius": 0.5 * mm});
            skCircle(sketch, "E97.80.3.0", {"center": v(-229.25, 149.5) * mm, "radius": 0.5 * mm});
            skCircle(sketch, "E97.82.3.0", {"center": v(-160.25, 147) * mm, "radius": 0.5 * mm});
            skCircle(sketch, "E97.84.3.0", {"center": v(-229.25, 147) * mm, "radius": 0.5 * mm});
            skCircle(sketch, "E97.86.3.0", {"center": v(-252.25, 152) * mm, "radius": 0.5 * mm});
            skCircle(sketch, "E97.88.3.0", {"center": v(-247.75, 152) * mm, "radius": 0.5 * mm});
            skCircle(sketch, "E97.90.3.0", {"center": v(-137.25, 149.5) * mm, "radius": 0.5 * mm});
            skCircle(sketch, "E97.92.3.0", {"center": v(-201.75, 152) * mm, "radius": 0.5 * mm});
            skCircle(sketch, "E97.94.3.0", {"center": v(-298.25, 152) * mm, "radius": 0.5 * mm});
            skCircle(sketch, "E97.96.3.0", {"center": v(-298.25, 149.5) * mm, "radius": 0.5 * mm});
            skCircle(sketch, "E97.98.3.0", {"center": v(-201.75, 149.5) * mm, "radius": 0.5 * mm});
            skCircle(sketch, "E97.100.3.0", {"center": v(-160.25, 149.5) * mm, "radius": 0.5 * mm});
            skCircle(sketch, "E97.102.3.0", {"center": v(-344.25, 147) * mm, "radius": 0.5 * mm});
            skCircle(sketch, "E97.104.3.0", {"center": v(-339.75, 147) * mm, "radius": 0.5 * mm});
            skCircle(sketch, "E97.106.3.0", {"center": v(-339.75, 152) * mm, "radius": 0.5 * mm});
            skCircle(sketch, "E97.108.3.0", {"center": v(-344.25, 149.5) * mm, "radius": 0.5 * mm});
            skCircle(sketch, "E97.110.3.0", {"center": v(-344.25, 152) * mm, "radius": 0.5 * mm});
            skCircle(sketch, "E97.112.3.0", {"center": v(-339.75, 149.5) * mm, "radius": 0.5 * mm});
            skCircle(sketch, "E97.114.3.0", {"center": v(-362.75, 147) * mm, "radius": 0.5 * mm});
            skCircle(sketch, "E97.116.3.0", {"center": v(-362.75, 152) * mm, "radius": 0.5 * mm});
            skCircle(sketch, "E97.118.3.0", {"center": v(-362.75, 149.5) * mm, "radius": 0.5 * mm});
            skCircle(sketch, "E97.0.4.0", {"center": v(-224.75, 124) * mm, "radius": 0.5 * mm});
            skCircle(sketch, "E97.2.4.0", {"center": v(-206.25, 126.5) * mm, "radius": 0.5 * mm});
            skCircle(sketch, "E97.4.4.0", {"center": v(-270.75, 124) * mm, "radius": 0.5 * mm});
            skCircle(sketch, "E97.6.4.0", {"center": v(-252.25, 124) * mm, "radius": 0.5 * mm});
            skCircle(sketch, "E97.8.4.0", {"center": v(-183.25, 129) * mm, "radius": 0.5 * mm});
            skCircle(sketch, "E97.10.4.0", {"center": v(-137.25, 124) * mm, "radius": 0.5 * mm});
            skCircle(sketch, "E97.12.4.0", {"center": v(-224.75, 126.5) * mm, "radius": 0.5 * mm});
            skCircle(sketch, "E97.14.4.0", {"center": v(-321.25, 124) * mm, "radius": 0.5 * mm});
            skCircle(sketch, "E97.16.4.0", {"center": v(-275.25, 124) * mm, "radius": 0.5 * mm});
            skCircle(sketch, "E97.18.4.0", {"center": v(-155.75, 124) * mm, "radius": 0.5 * mm});
            skCircle(sketch, "E97.20.4.0", {"center": v(-298.25, 124) * mm, "radius": 0.5 * mm});
            skCircle(sketch, "E97.22.4.0", {"center": v(-270.75, 126.5) * mm, "radius": 0.5 * mm});
            skCircle(sketch, "E97.24.4.0", {"center": v(-206.25, 129) * mm, "radius": 0.5 * mm});
            skCircle(sketch, "E97.26.4.0", {"center": v(-201.75, 124) * mm, "radius": 0.5 * mm});
            skCircle(sketch, "E97.28.4.0", {"center": v(-275.25, 126.5) * mm, "radius": 0.5 * mm});
            skCircle(sketch, "E97.30.4.0", {"center": v(-270.75, 129) * mm, "radius": 0.5 * mm});
            skCircle(sketch, "E97.32.4.0", {"center": v(-178.75, 129) * mm, "radius": 0.5 * mm});
            skCircle(sketch, "E97.34.4.0", {"center": v(-137.25, 129) * mm, "radius": 0.5 * mm});
            skCircle(sketch, "E97.36.4.0", {"center": v(-321.25, 129) * mm, "radius": 0.5 * mm});
            skCircle(sketch, "E97.38.4.0", {"center": v(-183.25, 124) * mm, "radius": 0.5 * mm});
            skCircle(sketch, "E97.40.4.0", {"center": v(-293.75, 126.5) * mm, "radius": 0.5 * mm});
            skCircle(sketch, "E97.42.4.0", {"center": v(-224.75, 129) * mm, "radius": 0.5 * mm});
            skCircle(sketch, "E97.44.4.0", {"center": v(-229.25, 129) * mm, "radius": 0.5 * mm});
            skCircle(sketch, "E97.46.4.0", {"center": v(-321.25, 126.5) * mm, "radius": 0.5 * mm});
            skCircle(sketch, "E97.48.4.0", {"center": v(-293.75, 124) * mm, "radius": 0.5 * mm});
            skCircle(sketch, "E97.50.4.0", {"center": v(-160.25, 129) * mm, "radius": 0.5 * mm});
            skCircle(sketch, "E97.52.4.0", {"center": v(-183.25, 126.5) * mm, "radius": 0.5 * mm});
            skCircle(sketch, "E97.54.4.0", {"center": v(-252.25, 126.5) * mm, "radius": 0.5 * mm});
            skCircle(sketch, "E97.56.4.0", {"center": v(-155.75, 126.5) * mm, "radius": 0.5 * mm});
            skCircle(sketch, "E97.58.4.0", {"center": v(-206.25, 124) * mm, "radius": 0.5 * mm});
            skCircle(sketch, "E97.60.4.0", {"center": v(-178.75, 126.5) * mm, "radius": 0.5 * mm});
            skCircle(sketch, "E97.62.4.0", {"center": v(-155.75, 129) * mm, "radius": 0.5 * mm});
            skCircle(sketch, "E97.64.4.0", {"center": v(-178.75, 124) * mm, "radius": 0.5 * mm});
            skCircle(sketch, "E97.66.4.0", {"center": v(-247.75, 126.5) * mm, "radius": 0.5 * mm});
            skCircle(sketch, "E97.68.4.0", {"center": v(-316.75, 124) * mm, "radius": 0.5 * mm});
            skCircle(sketch, "E97.70.4.0", {"center": v(-316.75, 129) * mm, "radius": 0.5 * mm});
            skCircle(sketch, "E97.72.4.0", {"center": v(-293.75, 129) * mm, "radius": 0.5 * mm});
            skCircle(sketch, "E97.74.4.0", {"center": v(-316.75, 126.5) * mm, "radius": 0.5 * mm});
            skCircle(sketch, "E97.76.4.0", {"center": v(-247.75, 124) * mm, "radius": 0.5 * mm});
            skCircle(sketch, "E97.78.4.0", {"center": v(-275.25, 129) * mm, "radius": 0.5 * mm});
            skCircle(sketch, "E97.80.4.0", {"center": v(-229.25, 126.5) * mm, "radius": 0.5 * mm});
            skCircle(sketch, "E97.82.4.0", {"center": v(-160.25, 124) * mm, "radius": 0.5 * mm});
            skCircle(sketch, "E97.84.4.0", {"center": v(-229.25, 124) * mm, "radius": 0.5 * mm});
            skCircle(sketch, "E97.86.4.0", {"center": v(-252.25, 129) * mm, "radius": 0.5 * mm});
            skCircle(sketch, "E97.88.4.0", {"center": v(-247.75, 129) * mm, "radius": 0.5 * mm});
            skCircle(sketch, "E97.90.4.0", {"center": v(-137.25, 126.5) * mm, "radius": 0.5 * mm});
            skCircle(sketch, "E97.92.4.0", {"center": v(-201.75, 129) * mm, "radius": 0.5 * mm});
            skCircle(sketch, "E97.94.4.0", {"center": v(-298.25, 129) * mm, "radius": 0.5 * mm});
            skCircle(sketch, "E97.96.4.0", {"center": v(-298.25, 126.5) * mm, "radius": 0.5 * mm});
            skCircle(sketch, "E97.98.4.0", {"center": v(-201.75, 126.5) * mm, "radius": 0.5 * mm});
            skCircle(sketch, "E97.100.4.0", {"center": v(-160.25, 126.5) * mm, "radius": 0.5 * mm});
            skCircle(sketch, "E97.102.4.0", {"center": v(-344.25, 124) * mm, "radius": 0.5 * mm});
            skCircle(sketch, "E97.104.4.0", {"center": v(-339.75, 124) * mm, "radius": 0.5 * mm});
            skCircle(sketch, "E97.106.4.0", {"center": v(-339.75, 129) * mm, "radius": 0.5 * mm});
            skCircle(sketch, "E97.108.4.0", {"center": v(-344.25, 126.5) * mm, "radius": 0.5 * mm});
            skCircle(sketch, "E97.110.4.0", {"center": v(-344.25, 129) * mm, "radius": 0.5 * mm});
            skCircle(sketch, "E97.112.4.0", {"center": v(-339.75, 126.5) * mm, "radius": 0.5 * mm});
            skCircle(sketch, "E97.114.4.0", {"center": v(-362.75, 124) * mm, "radius": 0.5 * mm});
            skCircle(sketch, "E97.116.4.0", {"center": v(-362.75, 129) * mm, "radius": 0.5 * mm});
            skCircle(sketch, "E97.118.4.0", {"center": v(-362.75, 126.5) * mm, "radius": 0.5 * mm});
            skCircle(sketch, "E97.0.5.0", {"center": v(-224.75, 101) * mm, "radius": 0.5 * mm});
            skCircle(sketch, "E97.2.5.0", {"center": v(-206.25, 103.5) * mm, "radius": 0.5 * mm});
            skCircle(sketch, "E97.4.5.0", {"center": v(-270.75, 101) * mm, "radius": 0.5 * mm});
            skCircle(sketch, "E97.6.5.0", {"center": v(-252.25, 101) * mm, "radius": 0.5 * mm});
            skCircle(sketch, "E97.8.5.0", {"center": v(-183.25, 106) * mm, "radius": 0.5 * mm});
            skCircle(sketch, "E97.10.5.0", {"center": v(-137.25, 101) * mm, "radius": 0.5 * mm});
            skCircle(sketch, "E97.12.5.0", {"center": v(-224.75, 103.5) * mm, "radius": 0.5 * mm});
            skCircle(sketch, "E97.14.5.0", {"center": v(-321.25, 101) * mm, "radius": 0.5 * mm});
            skCircle(sketch, "E97.16.5.0", {"center": v(-275.25, 101) * mm, "radius": 0.5 * mm});
            skCircle(sketch, "E97.18.5.0", {"center": v(-155.75, 101) * mm, "radius": 0.5 * mm});
            skCircle(sketch, "E97.20.5.0", {"center": v(-298.25, 101) * mm, "radius": 0.5 * mm});
            skCircle(sketch, "E97.22.5.0", {"center": v(-270.75, 103.5) * mm, "radius": 0.5 * mm});
            skCircle(sketch, "E97.24.5.0", {"center": v(-206.25, 106) * mm, "radius": 0.5 * mm});
            skCircle(sketch, "E97.26.5.0", {"center": v(-201.75, 101) * mm, "radius": 0.5 * mm});
            skCircle(sketch, "E97.28.5.0", {"center": v(-275.25, 103.5) * mm, "radius": 0.5 * mm});
            skCircle(sketch, "E97.30.5.0", {"center": v(-270.75, 106) * mm, "radius": 0.5 * mm});
            skCircle(sketch, "E97.32.5.0", {"center": v(-178.75, 106) * mm, "radius": 0.5 * mm});
            skCircle(sketch, "E97.34.5.0", {"center": v(-137.25, 106) * mm, "radius": 0.5 * mm});
            skCircle(sketch, "E97.36.5.0", {"center": v(-321.25, 106) * mm, "radius": 0.5 * mm});
            skCircle(sketch, "E97.38.5.0", {"center": v(-183.25, 101) * mm, "radius": 0.5 * mm});
            skCircle(sketch, "E97.40.5.0", {"center": v(-293.75, 103.5) * mm, "radius": 0.5 * mm});
            skCircle(sketch, "E97.42.5.0", {"center": v(-224.75, 106) * mm, "radius": 0.5 * mm});
            skCircle(sketch, "E97.44.5.0", {"center": v(-229.25, 106) * mm, "radius": 0.5 * mm});
            skCircle(sketch, "E97.46.5.0", {"center": v(-321.25, 103.5) * mm, "radius": 0.5 * mm});
            skCircle(sketch, "E97.48.5.0", {"center": v(-293.75, 101) * mm, "radius": 0.5 * mm});
            skCircle(sketch, "E97.50.5.0", {"center": v(-160.25, 106) * mm, "radius": 0.5 * mm});
            skCircle(sketch, "E97.52.5.0", {"center": v(-183.25, 103.5) * mm, "radius": 0.5 * mm});
            skCircle(sketch, "E97.54.5.0", {"center": v(-252.25, 103.5) * mm, "radius": 0.5 * mm});
            skCircle(sketch, "E97.56.5.0", {"center": v(-155.75, 103.5) * mm, "radius": 0.5 * mm});
            skCircle(sketch, "E97.58.5.0", {"center": v(-206.25, 101) * mm, "radius": 0.5 * mm});
            skCircle(sketch, "E97.60.5.0", {"center": v(-178.75, 103.5) * mm, "radius": 0.5 * mm});
            skCircle(sketch, "E97.62.5.0", {"center": v(-155.75, 106) * mm, "radius": 0.5 * mm});
            skCircle(sketch, "E97.64.5.0", {"center": v(-178.75, 101) * mm, "radius": 0.5 * mm});
            skCircle(sketch, "E97.66.5.0", {"center": v(-247.75, 103.5) * mm, "radius": 0.5 * mm});
            skCircle(sketch, "E97.68.5.0", {"center": v(-316.75, 101) * mm, "radius": 0.5 * mm});
            skCircle(sketch, "E97.70.5.0", {"center": v(-316.75, 106) * mm, "radius": 0.5 * mm});
            skCircle(sketch, "E97.72.5.0", {"center": v(-293.75, 106) * mm, "radius": 0.5 * mm});
            skCircle(sketch, "E97.74.5.0", {"center": v(-316.75, 103.5) * mm, "radius": 0.5 * mm});
            skCircle(sketch, "E97.76.5.0", {"center": v(-247.75, 101) * mm, "radius": 0.5 * mm});
            skCircle(sketch, "E97.78.5.0", {"center": v(-275.25, 106) * mm, "radius": 0.5 * mm});
            skCircle(sketch, "E97.80.5.0", {"center": v(-229.25, 103.5) * mm, "radius": 0.5 * mm});
            skCircle(sketch, "E97.82.5.0", {"center": v(-160.25, 101) * mm, "radius": 0.5 * mm});
            skCircle(sketch, "E97.84.5.0", {"center": v(-229.25, 101) * mm, "radius": 0.5 * mm});
            skCircle(sketch, "E97.86.5.0", {"center": v(-252.25, 106) * mm, "radius": 0.5 * mm});
            skCircle(sketch, "E97.88.5.0", {"center": v(-247.75, 106) * mm, "radius": 0.5 * mm});
            skCircle(sketch, "E97.90.5.0", {"center": v(-137.25, 103.5) * mm, "radius": 0.5 * mm});
            skCircle(sketch, "E97.92.5.0", {"center": v(-201.75, 106) * mm, "radius": 0.5 * mm});
            skCircle(sketch, "E97.94.5.0", {"center": v(-298.25, 106) * mm, "radius": 0.5 * mm});
            skCircle(sketch, "E97.96.5.0", {"center": v(-298.25, 103.5) * mm, "radius": 0.5 * mm});
            skCircle(sketch, "E97.98.5.0", {"center": v(-201.75, 103.5) * mm, "radius": 0.5 * mm});
            skCircle(sketch, "E97.100.5.0", {"center": v(-160.25, 103.5) * mm, "radius": 0.5 * mm});
            skCircle(sketch, "E97.102.5.0", {"center": v(-344.25, 101) * mm, "radius": 0.5 * mm});
            skCircle(sketch, "E97.104.5.0", {"center": v(-339.75, 101) * mm, "radius": 0.5 * mm});
            skCircle(sketch, "E97.106.5.0", {"center": v(-339.75, 106) * mm, "radius": 0.5 * mm});
            skCircle(sketch, "E97.108.5.0", {"center": v(-344.25, 103.5) * mm, "radius": 0.5 * mm});
            skCircle(sketch, "E97.110.5.0", {"center": v(-344.25, 106) * mm, "radius": 0.5 * mm});
            skCircle(sketch, "E97.112.5.0", {"center": v(-339.75, 103.5) * mm, "radius": 0.5 * mm});
            skCircle(sketch, "E97.114.5.0", {"center": v(-362.75, 101) * mm, "radius": 0.5 * mm});
            skCircle(sketch, "E97.116.5.0", {"center": v(-362.75, 106) * mm, "radius": 0.5 * mm});
            skCircle(sketch, "E97.118.5.0", {"center": v(-362.75, 103.5) * mm, "radius": 0.5 * mm});
            skCircle(sketch, "E97.0.6.0", {"center": v(-224.75, 78) * mm, "radius": 0.5 * mm});
            skCircle(sketch, "E97.2.6.0", {"center": v(-206.25, 80.5) * mm, "radius": 0.5 * mm});
            skCircle(sketch, "E97.4.6.0", {"center": v(-270.75, 78) * mm, "radius": 0.5 * mm});
            skCircle(sketch, "E97.6.6.0", {"center": v(-252.25, 78) * mm, "radius": 0.5 * mm});
            skCircle(sketch, "E97.8.6.0", {"center": v(-183.25, 83) * mm, "radius": 0.5 * mm});
            skCircle(sketch, "E97.10.6.0", {"center": v(-137.25, 78) * mm, "radius": 0.5 * mm});
            skCircle(sketch, "E97.12.6.0", {"center": v(-224.75, 80.5) * mm, "radius": 0.5 * mm});
            skCircle(sketch, "E97.14.6.0", {"center": v(-321.25, 78) * mm, "radius": 0.5 * mm});
            skCircle(sketch, "E97.16.6.0", {"center": v(-275.25, 78) * mm, "radius": 0.5 * mm});
            skCircle(sketch, "E97.18.6.0", {"center": v(-155.75, 78) * mm, "radius": 0.5 * mm});
            skCircle(sketch, "E97.20.6.0", {"center": v(-298.25, 78) * mm, "radius": 0.5 * mm});
            skCircle(sketch, "E97.22.6.0", {"center": v(-270.75, 80.5) * mm, "radius": 0.5 * mm});
            skCircle(sketch, "E97.24.6.0", {"center": v(-206.25, 83) * mm, "radius": 0.5 * mm});
            skCircle(sketch, "E97.26.6.0", {"center": v(-201.75, 78) * mm, "radius": 0.5 * mm});
            skCircle(sketch, "E97.28.6.0", {"center": v(-275.25, 80.5) * mm, "radius": 0.5 * mm});
            skCircle(sketch, "E97.30.6.0", {"center": v(-270.75, 83) * mm, "radius": 0.5 * mm});
            skCircle(sketch, "E97.32.6.0", {"center": v(-178.75, 83) * mm, "radius": 0.5 * mm});
            skCircle(sketch, "E97.34.6.0", {"center": v(-137.25, 83) * mm, "radius": 0.5 * mm});
            skCircle(sketch, "E97.36.6.0", {"center": v(-321.25, 83) * mm, "radius": 0.5 * mm});
            skCircle(sketch, "E97.38.6.0", {"center": v(-183.25, 78) * mm, "radius": 0.5 * mm});
            skCircle(sketch, "E97.40.6.0", {"center": v(-293.75, 80.5) * mm, "radius": 0.5 * mm});
            skCircle(sketch, "E97.42.6.0", {"center": v(-224.75, 83) * mm, "radius": 0.5 * mm});
            skCircle(sketch, "E97.44.6.0", {"center": v(-229.25, 83) * mm, "radius": 0.5 * mm});
            skCircle(sketch, "E97.46.6.0", {"center": v(-321.25, 80.5) * mm, "radius": 0.5 * mm});
            skCircle(sketch, "E97.48.6.0", {"center": v(-293.75, 78) * mm, "radius": 0.5 * mm});
            skCircle(sketch, "E97.50.6.0", {"center": v(-160.25, 83) * mm, "radius": 0.5 * mm});
            skCircle(sketch, "E97.52.6.0", {"center": v(-183.25, 80.5) * mm, "radius": 0.5 * mm});
            skCircle(sketch, "E97.54.6.0", {"center": v(-252.25, 80.5) * mm, "radius": 0.5 * mm});
            skCircle(sketch, "E97.56.6.0", {"center": v(-155.75, 80.5) * mm, "radius": 0.5 * mm});
            skCircle(sketch, "E97.58.6.0", {"center": v(-206.25, 78) * mm, "radius": 0.5 * mm});
            skCircle(sketch, "E97.60.6.0", {"center": v(-178.75, 80.5) * mm, "radius": 0.5 * mm});
            skCircle(sketch, "E97.62.6.0", {"center": v(-155.75, 83) * mm, "radius": 0.5 * mm});
            skCircle(sketch, "E97.64.6.0", {"center": v(-178.75, 78) * mm, "radius": 0.5 * mm});
            skCircle(sketch, "E97.66.6.0", {"center": v(-247.75, 80.5) * mm, "radius": 0.5 * mm});
            skCircle(sketch, "E97.68.6.0", {"center": v(-316.75, 78) * mm, "radius": 0.5 * mm});
            skCircle(sketch, "E97.70.6.0", {"center": v(-316.75, 83) * mm, "radius": 0.5 * mm});
            skCircle(sketch, "E97.72.6.0", {"center": v(-293.75, 83) * mm, "radius": 0.5 * mm});
            skCircle(sketch, "E97.74.6.0", {"center": v(-316.75, 80.5) * mm, "radius": 0.5 * mm});
            skCircle(sketch, "E97.76.6.0", {"center": v(-247.75, 78) * mm, "radius": 0.5 * mm});
            skCircle(sketch, "E97.78.6.0", {"center": v(-275.25, 83) * mm, "radius": 0.5 * mm});
            skCircle(sketch, "E97.80.6.0", {"center": v(-229.25, 80.5) * mm, "radius": 0.5 * mm});
            skCircle(sketch, "E97.82.6.0", {"center": v(-160.25, 78) * mm, "radius": 0.5 * mm});
            skCircle(sketch, "E97.84.6.0", {"center": v(-229.25, 78) * mm, "radius": 0.5 * mm});
            skCircle(sketch, "E97.86.6.0", {"center": v(-252.25, 83) * mm, "radius": 0.5 * mm});
            skCircle(sketch, "E97.88.6.0", {"center": v(-247.75, 83) * mm, "radius": 0.5 * mm});
            skCircle(sketch, "E97.90.6.0", {"center": v(-137.25, 80.5) * mm, "radius": 0.5 * mm});
            skCircle(sketch, "E97.92.6.0", {"center": v(-201.75, 83) * mm, "radius": 0.5 * mm});
            skCircle(sketch, "E97.94.6.0", {"center": v(-298.25, 83) * mm, "radius": 0.5 * mm});
            skCircle(sketch, "E97.96.6.0", {"center": v(-298.25, 80.5) * mm, "radius": 0.5 * mm});
            skCircle(sketch, "E97.98.6.0", {"center": v(-201.75, 80.5) * mm, "radius": 0.5 * mm});
            skCircle(sketch, "E97.100.6.0", {"center": v(-160.25, 80.5) * mm, "radius": 0.5 * mm});
            skCircle(sketch, "E97.102.6.0", {"center": v(-344.25, 78) * mm, "radius": 0.5 * mm});
            skCircle(sketch, "E97.104.6.0", {"center": v(-339.75, 78) * mm, "radius": 0.5 * mm});
            skCircle(sketch, "E97.106.6.0", {"center": v(-339.75, 83) * mm, "radius": 0.5 * mm});
            skCircle(sketch, "E97.108.6.0", {"center": v(-344.25, 80.5) * mm, "radius": 0.5 * mm});
            skCircle(sketch, "E97.110.6.0", {"center": v(-344.25, 83) * mm, "radius": 0.5 * mm});
            skCircle(sketch, "E97.112.6.0", {"center": v(-339.75, 80.5) * mm, "radius": 0.5 * mm});
            skCircle(sketch, "E97.114.6.0", {"center": v(-362.75, 78) * mm, "radius": 0.5 * mm});
            skCircle(sketch, "E97.116.6.0", {"center": v(-362.75, 83) * mm, "radius": 0.5 * mm});
            skCircle(sketch, "E97.118.6.0", {"center": v(-362.75, 80.5) * mm, "radius": 0.5 * mm});
            skCircle(sketch, "E97.0.7.0", {"center": v(-224.75, 55) * mm, "radius": 0.5 * mm});
            skCircle(sketch, "E97.2.7.0", {"center": v(-206.25, 57.5) * mm, "radius": 0.5 * mm});
            skCircle(sketch, "E97.4.7.0", {"center": v(-270.75, 55) * mm, "radius": 0.5 * mm});
            skCircle(sketch, "E97.6.7.0", {"center": v(-252.25, 55) * mm, "radius": 0.5 * mm});
            skCircle(sketch, "E97.8.7.0", {"center": v(-183.25, 60) * mm, "radius": 0.5 * mm});
            skCircle(sketch, "E97.10.7.0", {"center": v(-137.25, 55) * mm, "radius": 0.5 * mm});
            skCircle(sketch, "E97.12.7.0", {"center": v(-224.75, 57.5) * mm, "radius": 0.5 * mm});
            skCircle(sketch, "E97.14.7.0", {"center": v(-321.25, 55) * mm, "radius": 0.5 * mm});
            skCircle(sketch, "E97.16.7.0", {"center": v(-275.25, 55) * mm, "radius": 0.5 * mm});
            skCircle(sketch, "E97.18.7.0", {"center": v(-155.75, 55) * mm, "radius": 0.5 * mm});
            skCircle(sketch, "E97.20.7.0", {"center": v(-298.25, 55) * mm, "radius": 0.5 * mm});
            skCircle(sketch, "E97.22.7.0", {"center": v(-270.75, 57.5) * mm, "radius": 0.5 * mm});
            skCircle(sketch, "E97.24.7.0", {"center": v(-206.25, 60) * mm, "radius": 0.5 * mm});
            skCircle(sketch, "E97.26.7.0", {"center": v(-201.75, 55) * mm, "radius": 0.5 * mm});
            skCircle(sketch, "E97.28.7.0", {"center": v(-275.25, 57.5) * mm, "radius": 0.5 * mm});
            skCircle(sketch, "E97.30.7.0", {"center": v(-270.75, 60) * mm, "radius": 0.5 * mm});
            skCircle(sketch, "E97.32.7.0", {"center": v(-178.75, 60) * mm, "radius": 0.5 * mm});
            skCircle(sketch, "E97.34.7.0", {"center": v(-137.25, 60) * mm, "radius": 0.5 * mm});
            skCircle(sketch, "E97.36.7.0", {"center": v(-321.25, 60) * mm, "radius": 0.5 * mm});
            skCircle(sketch, "E97.38.7.0", {"center": v(-183.25, 55) * mm, "radius": 0.5 * mm});
            skCircle(sketch, "E97.40.7.0", {"center": v(-293.75, 57.5) * mm, "radius": 0.5 * mm});
            skCircle(sketch, "E97.42.7.0", {"center": v(-224.75, 60) * mm, "radius": 0.5 * mm});
            skCircle(sketch, "E97.44.7.0", {"center": v(-229.25, 60) * mm, "radius": 0.5 * mm});
            skCircle(sketch, "E97.46.7.0", {"center": v(-321.25, 57.5) * mm, "radius": 0.5 * mm});
            skCircle(sketch, "E97.48.7.0", {"center": v(-293.75, 55) * mm, "radius": 0.5 * mm});
            skCircle(sketch, "E97.50.7.0", {"center": v(-160.25, 60) * mm, "radius": 0.5 * mm});
            skCircle(sketch, "E97.52.7.0", {"center": v(-183.25, 57.5) * mm, "radius": 0.5 * mm});
            skCircle(sketch, "E97.54.7.0", {"center": v(-252.25, 57.5) * mm, "radius": 0.5 * mm});
            skCircle(sketch, "E97.56.7.0", {"center": v(-155.75, 57.5) * mm, "radius": 0.5 * mm});
            skCircle(sketch, "E97.58.7.0", {"center": v(-206.25, 55) * mm, "radius": 0.5 * mm});
            skCircle(sketch, "E97.60.7.0", {"center": v(-178.75, 57.5) * mm, "radius": 0.5 * mm});
            skCircle(sketch, "E97.62.7.0", {"center": v(-155.75, 60) * mm, "radius": 0.5 * mm});
            skCircle(sketch, "E97.64.7.0", {"center": v(-178.75, 55) * mm, "radius": 0.5 * mm});
            skCircle(sketch, "E97.66.7.0", {"center": v(-247.75, 57.5) * mm, "radius": 0.5 * mm});
            skCircle(sketch, "E97.68.7.0", {"center": v(-316.75, 55) * mm, "radius": 0.5 * mm});
            skCircle(sketch, "E97.70.7.0", {"center": v(-316.75, 60) * mm, "radius": 0.5 * mm});
            skCircle(sketch, "E97.72.7.0", {"center": v(-293.75, 60) * mm, "radius": 0.5 * mm});
            skCircle(sketch, "E97.74.7.0", {"center": v(-316.75, 57.5) * mm, "radius": 0.5 * mm});
            skCircle(sketch, "E97.76.7.0", {"center": v(-247.75, 55) * mm, "radius": 0.5 * mm});
            skCircle(sketch, "E97.78.7.0", {"center": v(-275.25, 60) * mm, "radius": 0.5 * mm});
            skCircle(sketch, "E97.80.7.0", {"center": v(-229.25, 57.5) * mm, "radius": 0.5 * mm});
            skCircle(sketch, "E97.82.7.0", {"center": v(-160.25, 55) * mm, "radius": 0.5 * mm});
            skCircle(sketch, "E97.84.7.0", {"center": v(-229.25, 55) * mm, "radius": 0.5 * mm});
            skCircle(sketch, "E97.86.7.0", {"center": v(-252.25, 60) * mm, "radius": 0.5 * mm});
            skCircle(sketch, "E97.88.7.0", {"center": v(-247.75, 60) * mm, "radius": 0.5 * mm});
            skCircle(sketch, "E97.90.7.0", {"center": v(-137.25, 57.5) * mm, "radius": 0.5 * mm});
            skCircle(sketch, "E97.92.7.0", {"center": v(-201.75, 60) * mm, "radius": 0.5 * mm});
            skCircle(sketch, "E97.94.7.0", {"center": v(-298.25, 60) * mm, "radius": 0.5 * mm});
            skCircle(sketch, "E97.96.7.0", {"center": v(-298.25, 57.5) * mm, "radius": 0.5 * mm});
            skCircle(sketch, "E97.98.7.0", {"center": v(-201.75, 57.5) * mm, "radius": 0.5 * mm});
            skCircle(sketch, "E97.100.7.0", {"center": v(-160.25, 57.5) * mm, "radius": 0.5 * mm});
            skCircle(sketch, "E97.102.7.0", {"center": v(-344.25, 55) * mm, "radius": 0.5 * mm});
            skCircle(sketch, "E97.104.7.0", {"center": v(-339.75, 55) * mm, "radius": 0.5 * mm});
            skCircle(sketch, "E97.106.7.0", {"center": v(-339.75, 60) * mm, "radius": 0.5 * mm});
            skCircle(sketch, "E97.108.7.0", {"center": v(-344.25, 57.5) * mm, "radius": 0.5 * mm});
            skCircle(sketch, "E97.110.7.0", {"center": v(-344.25, 60) * mm, "radius": 0.5 * mm});
            skCircle(sketch, "E97.112.7.0", {"center": v(-339.75, 57.5) * mm, "radius": 0.5 * mm});
            skCircle(sketch, "E97.114.7.0", {"center": v(-362.75, 55) * mm, "radius": 0.5 * mm});
            skCircle(sketch, "E97.116.7.0", {"center": v(-362.75, 60) * mm, "radius": 0.5 * mm});
            skCircle(sketch, "E97.118.7.0", {"center": v(-362.75, 57.5) * mm, "radius": 0.5 * mm});
            skCircle(sketch, "E97.0.8.0", {"center": v(-224.75, 32) * mm, "radius": 0.5 * mm});
            skCircle(sketch, "E97.2.8.0", {"center": v(-206.25, 34.5) * mm, "radius": 0.5 * mm});
            skCircle(sketch, "E97.4.8.0", {"center": v(-270.75, 32) * mm, "radius": 0.5 * mm});
            skCircle(sketch, "E97.6.8.0", {"center": v(-252.25, 32) * mm, "radius": 0.5 * mm});
            skCircle(sketch, "E97.8.8.0", {"center": v(-183.25, 37) * mm, "radius": 0.5 * mm});
            skCircle(sketch, "E97.10.8.0", {"center": v(-137.25, 32) * mm, "radius": 0.5 * mm});
            skCircle(sketch, "E97.12.8.0", {"center": v(-224.75, 34.5) * mm, "radius": 0.5 * mm});
            skCircle(sketch, "E97.14.8.0", {"center": v(-321.25, 32) * mm, "radius": 0.5 * mm});
            skCircle(sketch, "E97.16.8.0", {"center": v(-275.25, 32) * mm, "radius": 0.5 * mm});
            skCircle(sketch, "E97.18.8.0", {"center": v(-155.75, 32) * mm, "radius": 0.5 * mm});
            skCircle(sketch, "E97.20.8.0", {"center": v(-298.25, 32) * mm, "radius": 0.5 * mm});
            skCircle(sketch, "E97.22.8.0", {"center": v(-270.75, 34.5) * mm, "radius": 0.5 * mm});
            skCircle(sketch, "E97.24.8.0", {"center": v(-206.25, 37) * mm, "radius": 0.5 * mm});
            skCircle(sketch, "E97.26.8.0", {"center": v(-201.75, 32) * mm, "radius": 0.5 * mm});
            skCircle(sketch, "E97.28.8.0", {"center": v(-275.25, 34.5) * mm, "radius": 0.5 * mm});
            skCircle(sketch, "E97.30.8.0", {"center": v(-270.75, 37) * mm, "radius": 0.5 * mm});
            skCircle(sketch, "E97.32.8.0", {"center": v(-178.75, 37) * mm, "radius": 0.5 * mm});
            skCircle(sketch, "E97.34.8.0", {"center": v(-137.25, 37) * mm, "radius": 0.5 * mm});
            skCircle(sketch, "E97.36.8.0", {"center": v(-321.25, 37) * mm, "radius": 0.5 * mm});
            skCircle(sketch, "E97.38.8.0", {"center": v(-183.25, 32) * mm, "radius": 0.5 * mm});
            skCircle(sketch, "E97.40.8.0", {"center": v(-293.75, 34.5) * mm, "radius": 0.5 * mm});
            skCircle(sketch, "E97.42.8.0", {"center": v(-224.75, 37) * mm, "radius": 0.5 * mm});
            skCircle(sketch, "E97.44.8.0", {"center": v(-229.25, 37) * mm, "radius": 0.5 * mm});
            skCircle(sketch, "E97.46.8.0", {"center": v(-321.25, 34.5) * mm, "radius": 0.5 * mm});
            skCircle(sketch, "E97.48.8.0", {"center": v(-293.75, 32) * mm, "radius": 0.5 * mm});
            skCircle(sketch, "E97.50.8.0", {"center": v(-160.25, 37) * mm, "radius": 0.5 * mm});
            skCircle(sketch, "E97.52.8.0", {"center": v(-183.25, 34.5) * mm, "radius": 0.5 * mm});
            skCircle(sketch, "E97.54.8.0", {"center": v(-252.25, 34.5) * mm, "radius": 0.5 * mm});
            skCircle(sketch, "E97.56.8.0", {"center": v(-155.75, 34.5) * mm, "radius": 0.5 * mm});
            skCircle(sketch, "E97.58.8.0", {"center": v(-206.25, 32) * mm, "radius": 0.5 * mm});
            skCircle(sketch, "E97.60.8.0", {"center": v(-178.75, 34.5) * mm, "radius": 0.5 * mm});
            skCircle(sketch, "E97.62.8.0", {"center": v(-155.75, 37) * mm, "radius": 0.5 * mm});
            skCircle(sketch, "E97.64.8.0", {"center": v(-178.75, 32) * mm, "radius": 0.5 * mm});
            skCircle(sketch, "E97.66.8.0", {"center": v(-247.75, 34.5) * mm, "radius": 0.5 * mm});
            skCircle(sketch, "E97.68.8.0", {"center": v(-316.75, 32) * mm, "radius": 0.5 * mm});
            skCircle(sketch, "E97.70.8.0", {"center": v(-316.75, 37) * mm, "radius": 0.5 * mm});
            skCircle(sketch, "E97.72.8.0", {"center": v(-293.75, 37) * mm, "radius": 0.5 * mm});
            skCircle(sketch, "E97.74.8.0", {"center": v(-316.75, 34.5) * mm, "radius": 0.5 * mm});
            skCircle(sketch, "E97.76.8.0", {"center": v(-247.75, 32) * mm, "radius": 0.5 * mm});
            skCircle(sketch, "E97.78.8.0", {"center": v(-275.25, 37) * mm, "radius": 0.5 * mm});
            skCircle(sketch, "E97.80.8.0", {"center": v(-229.25, 34.5) * mm, "radius": 0.5 * mm});
            skCircle(sketch, "E97.82.8.0", {"center": v(-160.25, 32) * mm, "radius": 0.5 * mm});
            skCircle(sketch, "E97.84.8.0", {"center": v(-229.25, 32) * mm, "radius": 0.5 * mm});
            skCircle(sketch, "E97.86.8.0", {"center": v(-252.25, 37) * mm, "radius": 0.5 * mm});
            skCircle(sketch, "E97.88.8.0", {"center": v(-247.75, 37) * mm, "radius": 0.5 * mm});
            skCircle(sketch, "E97.90.8.0", {"center": v(-137.25, 34.5) * mm, "radius": 0.5 * mm});
            skCircle(sketch, "E97.92.8.0", {"center": v(-201.75, 37) * mm, "radius": 0.5 * mm});
            skCircle(sketch, "E97.94.8.0", {"center": v(-298.25, 37) * mm, "radius": 0.5 * mm});
            skCircle(sketch, "E97.96.8.0", {"center": v(-298.25, 34.5) * mm, "radius": 0.5 * mm});
            skCircle(sketch, "E97.98.8.0", {"center": v(-201.75, 34.5) * mm, "radius": 0.5 * mm});
            skCircle(sketch, "E97.100.8.0", {"center": v(-160.25, 34.5) * mm, "radius": 0.5 * mm});
            skCircle(sketch, "E97.102.8.0", {"center": v(-344.25, 32) * mm, "radius": 0.5 * mm});
            skCircle(sketch, "E97.104.8.0", {"center": v(-339.75, 32) * mm, "radius": 0.5 * mm});
            skCircle(sketch, "E97.106.8.0", {"center": v(-339.75, 37) * mm, "radius": 0.5 * mm});
            skCircle(sketch, "E97.108.8.0", {"center": v(-344.25, 34.5) * mm, "radius": 0.5 * mm});
            skCircle(sketch, "E97.110.8.0", {"center": v(-344.25, 37) * mm, "radius": 0.5 * mm});
            skCircle(sketch, "E97.112.8.0", {"center": v(-339.75, 34.5) * mm, "radius": 0.5 * mm});
            skCircle(sketch, "E97.114.8.0", {"center": v(-362.75, 32) * mm, "radius": 0.5 * mm});
            skCircle(sketch, "E97.116.8.0", {"center": v(-362.75, 37) * mm, "radius": 0.5 * mm});
            skCircle(sketch, "E97.118.8.0", {"center": v(-362.75, 34.5) * mm, "radius": 0.5 * mm});
            skCircle(sketch, "E97.0.9.0", {"center": v(-224.75, 9) * mm, "radius": 0.5 * mm});
            skCircle(sketch, "E97.2.9.0", {"center": v(-206.25, 11.5) * mm, "radius": 0.5 * mm});
            skCircle(sketch, "E97.4.9.0", {"center": v(-270.75, 9) * mm, "radius": 0.5 * mm});
            skCircle(sketch, "E97.6.9.0", {"center": v(-252.25, 9) * mm, "radius": 0.5 * mm});
            skCircle(sketch, "E97.8.9.0", {"center": v(-183.25, 14) * mm, "radius": 0.5 * mm});
            skCircle(sketch, "E97.10.9.0", {"center": v(-137.25, 9) * mm, "radius": 0.5 * mm});
            skCircle(sketch, "E97.12.9.0", {"center": v(-224.75, 11.5) * mm, "radius": 0.5 * mm});
            skCircle(sketch, "E97.14.9.0", {"center": v(-321.25, 9) * mm, "radius": 0.5 * mm});
            skCircle(sketch, "E97.16.9.0", {"center": v(-275.25, 9) * mm, "radius": 0.5 * mm});
            skCircle(sketch, "E97.18.9.0", {"center": v(-155.75, 9) * mm, "radius": 0.5 * mm});
            skCircle(sketch, "E97.20.9.0", {"center": v(-298.25, 9) * mm, "radius": 0.5 * mm});
            skCircle(sketch, "E97.22.9.0", {"center": v(-270.75, 11.5) * mm, "radius": 0.5 * mm});
            skCircle(sketch, "E97.24.9.0", {"center": v(-206.25, 14) * mm, "radius": 0.5 * mm});
            skCircle(sketch, "E97.26.9.0", {"center": v(-201.75, 9) * mm, "radius": 0.5 * mm});
            skCircle(sketch, "E97.28.9.0", {"center": v(-275.25, 11.5) * mm, "radius": 0.5 * mm});
            skCircle(sketch, "E97.30.9.0", {"center": v(-270.75, 14) * mm, "radius": 0.5 * mm});
            skCircle(sketch, "E97.32.9.0", {"center": v(-178.75, 14) * mm, "radius": 0.5 * mm});
            skCircle(sketch, "E97.34.9.0", {"center": v(-137.25, 14) * mm, "radius": 0.5 * mm});
            skCircle(sketch, "E97.36.9.0", {"center": v(-321.25, 14) * mm, "radius": 0.5 * mm});
            skCircle(sketch, "E97.38.9.0", {"center": v(-183.25, 9) * mm, "radius": 0.5 * mm});
            skCircle(sketch, "E97.40.9.0", {"center": v(-293.75, 11.5) * mm, "radius": 0.5 * mm});
            skCircle(sketch, "E97.42.9.0", {"center": v(-224.75, 14) * mm, "radius": 0.5 * mm});
            skCircle(sketch, "E97.44.9.0", {"center": v(-229.25, 14) * mm, "radius": 0.5 * mm});
            skCircle(sketch, "E97.46.9.0", {"center": v(-321.25, 11.5) * mm, "radius": 0.5 * mm});
            skCircle(sketch, "E97.48.9.0", {"center": v(-293.75, 9) * mm, "radius": 0.5 * mm});
            skCircle(sketch, "E97.50.9.0", {"center": v(-160.25, 14) * mm, "radius": 0.5 * mm});
            skCircle(sketch, "E97.52.9.0", {"center": v(-183.25, 11.5) * mm, "radius": 0.5 * mm});
            skCircle(sketch, "E97.54.9.0", {"center": v(-252.25, 11.5) * mm, "radius": 0.5 * mm});
            skCircle(sketch, "E97.56.9.0", {"center": v(-155.75, 11.5) * mm, "radius": 0.5 * mm});
            skCircle(sketch, "E97.58.9.0", {"center": v(-206.25, 9) * mm, "radius": 0.5 * mm});
            skCircle(sketch, "E97.60.9.0", {"center": v(-178.75, 11.5) * mm, "radius": 0.5 * mm});
            skCircle(sketch, "E97.62.9.0", {"center": v(-155.75, 14) * mm, "radius": 0.5 * mm});
            skCircle(sketch, "E97.64.9.0", {"center": v(-178.75, 9) * mm, "radius": 0.5 * mm});
            skCircle(sketch, "E97.66.9.0", {"center": v(-247.75, 11.5) * mm, "radius": 0.5 * mm});
            skCircle(sketch, "E97.68.9.0", {"center": v(-316.75, 9) * mm, "radius": 0.5 * mm});
            skCircle(sketch, "E97.70.9.0", {"center": v(-316.75, 14) * mm, "radius": 0.5 * mm});
            skCircle(sketch, "E97.72.9.0", {"center": v(-293.75, 14) * mm, "radius": 0.5 * mm});
            skCircle(sketch, "E97.74.9.0", {"center": v(-316.75, 11.5) * mm, "radius": 0.5 * mm});
            skCircle(sketch, "E97.76.9.0", {"center": v(-247.75, 9) * mm, "radius": 0.5 * mm});
            skCircle(sketch, "E97.78.9.0", {"center": v(-275.25, 14) * mm, "radius": 0.5 * mm});
            skCircle(sketch, "E97.80.9.0", {"center": v(-229.25, 11.5) * mm, "radius": 0.5 * mm});
            skCircle(sketch, "E97.82.9.0", {"center": v(-160.25, 9) * mm, "radius": 0.5 * mm});
            skCircle(sketch, "E97.84.9.0", {"center": v(-229.25, 9) * mm, "radius": 0.5 * mm});
            skCircle(sketch, "E97.86.9.0", {"center": v(-252.25, 14) * mm, "radius": 0.5 * mm});
            skCircle(sketch, "E97.88.9.0", {"center": v(-247.75, 14) * mm, "radius": 0.5 * mm});
            skCircle(sketch, "E97.90.9.0", {"center": v(-137.25, 11.5) * mm, "radius": 0.5 * mm});
            skCircle(sketch, "E97.92.9.0", {"center": v(-201.75, 14) * mm, "radius": 0.5 * mm});
            skCircle(sketch, "E97.94.9.0", {"center": v(-298.25, 14) * mm, "radius": 0.5 * mm});
            skCircle(sketch, "E97.96.9.0", {"center": v(-298.25, 11.5) * mm, "radius": 0.5 * mm});
            skCircle(sketch, "E97.98.9.0", {"center": v(-201.75, 11.5) * mm, "radius": 0.5 * mm});
            skCircle(sketch, "E97.100.9.0", {"center": v(-160.25, 11.5) * mm, "radius": 0.5 * mm});
            skCircle(sketch, "E97.102.9.0", {"center": v(-344.25, 9) * mm, "radius": 0.5 * mm});
            skCircle(sketch, "E97.104.9.0", {"center": v(-339.75, 9) * mm, "radius": 0.5 * mm});
            skCircle(sketch, "E97.106.9.0", {"center": v(-339.75, 14) * mm, "radius": 0.5 * mm});
            skCircle(sketch, "E97.108.9.0", {"center": v(-344.25, 11.5) * mm, "radius": 0.5 * mm});
            skCircle(sketch, "E97.110.9.0", {"center": v(-344.25, 14) * mm, "radius": 0.5 * mm});
            skCircle(sketch, "E97.112.9.0", {"center": v(-339.75, 11.5) * mm, "radius": 0.5 * mm});
            skCircle(sketch, "E97.114.9.0", {"center": v(-362.75, 9) * mm, "radius": 0.5 * mm});
            skCircle(sketch, "E97.116.9.0", {"center": v(-362.75, 14) * mm, "radius": 0.5 * mm});
            skCircle(sketch, "E97.118.9.0", {"center": v(-362.75, 11.5) * mm, "radius": 0.5 * mm});
            skCircle(sketch, "E97.0.10.0", {"center": v(-224.75, -14) * mm, "radius": 0.5 * mm});
            skCircle(sketch, "E97.2.10.0", {"center": v(-206.25, -11.5) * mm, "radius": 0.5 * mm});
            skCircle(sketch, "E97.4.10.0", {"center": v(-270.75, -14) * mm, "radius": 0.5 * mm});
            skCircle(sketch, "E97.6.10.0", {"center": v(-252.25, -14) * mm, "radius": 0.5 * mm});
            skCircle(sketch, "E97.8.10.0", {"center": v(-183.25, -9) * mm, "radius": 0.5 * mm});
            skCircle(sketch, "E97.10.10.0", {"center": v(-137.25, -14) * mm, "radius": 0.5 * mm});
            skCircle(sketch, "E97.12.10.0", {"center": v(-224.75, -11.5) * mm, "radius": 0.5 * mm});
            skCircle(sketch, "E97.14.10.0", {"center": v(-321.25, -14) * mm, "radius": 0.5 * mm});
            skCircle(sketch, "E97.16.10.0", {"center": v(-275.25, -14) * mm, "radius": 0.5 * mm});
            skCircle(sketch, "E97.18.10.0", {"center": v(-155.75, -14) * mm, "radius": 0.5 * mm});
            skCircle(sketch, "E97.20.10.0", {"center": v(-298.25, -14) * mm, "radius": 0.5 * mm});
            skCircle(sketch, "E97.22.10.0", {"center": v(-270.75, -11.5) * mm, "radius": 0.5 * mm});
            skCircle(sketch, "E97.24.10.0", {"center": v(-206.25, -9) * mm, "radius": 0.5 * mm});
            skCircle(sketch, "E97.26.10.0", {"center": v(-201.75, -14) * mm, "radius": 0.5 * mm});
            skCircle(sketch, "E97.28.10.0", {"center": v(-275.25, -11.5) * mm, "radius": 0.5 * mm});
            skCircle(sketch, "E97.30.10.0", {"center": v(-270.75, -9) * mm, "radius": 0.5 * mm});
            skCircle(sketch, "E97.32.10.0", {"center": v(-178.75, -9) * mm, "radius": 0.5 * mm});
            skCircle(sketch, "E97.34.10.0", {"center": v(-137.25, -9) * mm, "radius": 0.5 * mm});
            skCircle(sketch, "E97.36.10.0", {"center": v(-321.25, -9) * mm, "radius": 0.5 * mm});
            skCircle(sketch, "E97.38.10.0", {"center": v(-183.25, -14) * mm, "radius": 0.5 * mm});
            skCircle(sketch, "E97.40.10.0", {"center": v(-293.75, -11.5) * mm, "radius": 0.5 * mm});
            skCircle(sketch, "E97.42.10.0", {"center": v(-224.75, -9) * mm, "radius": 0.5 * mm});
            skCircle(sketch, "E97.44.10.0", {"center": v(-229.25, -9) * mm, "radius": 0.5 * mm});
            skCircle(sketch, "E97.46.10.0", {"center": v(-321.25, -11.5) * mm, "radius": 0.5 * mm});
            skCircle(sketch, "E97.48.10.0", {"center": v(-293.75, -14) * mm, "radius": 0.5 * mm});
            skCircle(sketch, "E97.50.10.0", {"center": v(-160.25, -9) * mm, "radius": 0.5 * mm});
            skCircle(sketch, "E97.52.10.0", {"center": v(-183.25, -11.5) * mm, "radius": 0.5 * mm});
            skCircle(sketch, "E97.54.10.0", {"center": v(-252.25, -11.5) * mm, "radius": 0.5 * mm});
            skCircle(sketch, "E97.56.10.0", {"center": v(-155.75, -11.5) * mm, "radius": 0.5 * mm});
            skCircle(sketch, "E97.58.10.0", {"center": v(-206.25, -14) * mm, "radius": 0.5 * mm});
            skCircle(sketch, "E97.60.10.0", {"center": v(-178.75, -11.5) * mm, "radius": 0.5 * mm});
            skCircle(sketch, "E97.62.10.0", {"center": v(-155.75, -9) * mm, "radius": 0.5 * mm});
            skCircle(sketch, "E97.64.10.0", {"center": v(-178.75, -14) * mm, "radius": 0.5 * mm});
            skCircle(sketch, "E97.66.10.0", {"center": v(-247.75, -11.5) * mm, "radius": 0.5 * mm});
            skCircle(sketch, "E97.68.10.0", {"center": v(-316.75, -14) * mm, "radius": 0.5 * mm});
            skCircle(sketch, "E97.70.10.0", {"center": v(-316.75, -9) * mm, "radius": 0.5 * mm});
            skCircle(sketch, "E97.72.10.0", {"center": v(-293.75, -9) * mm, "radius": 0.5 * mm});
            skCircle(sketch, "E97.74.10.0", {"center": v(-316.75, -11.5) * mm, "radius": 0.5 * mm});
            skCircle(sketch, "E97.76.10.0", {"center": v(-247.75, -14) * mm, "radius": 0.5 * mm});
            skCircle(sketch, "E97.78.10.0", {"center": v(-275.25, -9) * mm, "radius": 0.5 * mm});
            skCircle(sketch, "E97.80.10.0", {"center": v(-229.25, -11.5) * mm, "radius": 0.5 * mm});
            skCircle(sketch, "E97.82.10.0", {"center": v(-160.25, -14) * mm, "radius": 0.5 * mm});
            skCircle(sketch, "E97.84.10.0", {"center": v(-229.25, -14) * mm, "radius": 0.5 * mm});
            skCircle(sketch, "E97.86.10.0", {"center": v(-252.25, -9) * mm, "radius": 0.5 * mm});
            skCircle(sketch, "E97.88.10.0", {"center": v(-247.75, -9) * mm, "radius": 0.5 * mm});
            skCircle(sketch, "E97.90.10.0", {"center": v(-137.25, -11.5) * mm, "radius": 0.5 * mm});
            skCircle(sketch, "E97.92.10.0", {"center": v(-201.75, -9) * mm, "radius": 0.5 * mm});
            skCircle(sketch, "E97.94.10.0", {"center": v(-298.25, -9) * mm, "radius": 0.5 * mm});
            skCircle(sketch, "E97.96.10.0", {"center": v(-298.25, -11.5) * mm, "radius": 0.5 * mm});
            skCircle(sketch, "E97.98.10.0", {"center": v(-201.75, -11.5) * mm, "radius": 0.5 * mm});
            skCircle(sketch, "E97.100.10.0", {"center": v(-160.25, -11.5) * mm, "radius": 0.5 * mm});
            skCircle(sketch, "E97.102.10.0", {"center": v(-344.25, -14) * mm, "radius": 0.5 * mm});
            skCircle(sketch, "E97.104.10.0", {"center": v(-339.75, -14) * mm, "radius": 0.5 * mm});
            skCircle(sketch, "E97.106.10.0", {"center": v(-339.75, -9) * mm, "radius": 0.5 * mm});
            skCircle(sketch, "E97.108.10.0", {"center": v(-344.25, -11.5) * mm, "radius": 0.5 * mm});
            skCircle(sketch, "E97.110.10.0", {"center": v(-344.25, -9) * mm, "radius": 0.5 * mm});
            skCircle(sketch, "E97.112.10.0", {"center": v(-339.75, -11.5) * mm, "radius": 0.5 * mm});
            skCircle(sketch, "E97.114.10.0", {"center": v(-362.75, -14) * mm, "radius": 0.5 * mm});
            skCircle(sketch, "E97.116.10.0", {"center": v(-362.75, -9) * mm, "radius": 0.5 * mm});
            skCircle(sketch, "E97.118.10.0", {"center": v(-362.75, -11.5) * mm, "radius": 0.5 * mm});
            skCircle(sketch, "E97.0.11.0", {"center": v(-224.75, -37) * mm, "radius": 0.5 * mm});
            skCircle(sketch, "E97.2.11.0", {"center": v(-206.25, -34.5) * mm, "radius": 0.5 * mm});
            skCircle(sketch, "E97.4.11.0", {"center": v(-270.75, -37) * mm, "radius": 0.5 * mm});
            skCircle(sketch, "E97.6.11.0", {"center": v(-252.25, -37) * mm, "radius": 0.5 * mm});
            skCircle(sketch, "E97.8.11.0", {"center": v(-183.25, -32) * mm, "radius": 0.5 * mm});
            skCircle(sketch, "E97.10.11.0", {"center": v(-137.25, -37) * mm, "radius": 0.5 * mm});
            skCircle(sketch, "E97.12.11.0", {"center": v(-224.75, -34.5) * mm, "radius": 0.5 * mm});
            skCircle(sketch, "E97.14.11.0", {"center": v(-321.25, -37) * mm, "radius": 0.5 * mm});
            skCircle(sketch, "E97.16.11.0", {"center": v(-275.25, -37) * mm, "radius": 0.5 * mm});
            skCircle(sketch, "E97.18.11.0", {"center": v(-155.75, -37) * mm, "radius": 0.5 * mm});
            skCircle(sketch, "E97.20.11.0", {"center": v(-298.25, -37) * mm, "radius": 0.5 * mm});
            skCircle(sketch, "E97.22.11.0", {"center": v(-270.75, -34.5) * mm, "radius": 0.5 * mm});
            skCircle(sketch, "E97.24.11.0", {"center": v(-206.25, -32) * mm, "radius": 0.5 * mm});
            skCircle(sketch, "E97.26.11.0", {"center": v(-201.75, -37) * mm, "radius": 0.5 * mm});
            skCircle(sketch, "E97.28.11.0", {"center": v(-275.25, -34.5) * mm, "radius": 0.5 * mm});
            skCircle(sketch, "E97.30.11.0", {"center": v(-270.75, -32) * mm, "radius": 0.5 * mm});
            skCircle(sketch, "E97.32.11.0", {"center": v(-178.75, -32) * mm, "radius": 0.5 * mm});
            skCircle(sketch, "E97.34.11.0", {"center": v(-137.25, -32) * mm, "radius": 0.5 * mm});
            skCircle(sketch, "E97.36.11.0", {"center": v(-321.25, -32) * mm, "radius": 0.5 * mm});
            skCircle(sketch, "E97.38.11.0", {"center": v(-183.25, -37) * mm, "radius": 0.5 * mm});
            skCircle(sketch, "E97.40.11.0", {"center": v(-293.75, -34.5) * mm, "radius": 0.5 * mm});
            skCircle(sketch, "E97.42.11.0", {"center": v(-224.75, -32) * mm, "radius": 0.5 * mm});
            skCircle(sketch, "E97.44.11.0", {"center": v(-229.25, -32) * mm, "radius": 0.5 * mm});
            skCircle(sketch, "E97.46.11.0", {"center": v(-321.25, -34.5) * mm, "radius": 0.5 * mm});
            skCircle(sketch, "E97.48.11.0", {"center": v(-293.75, -37) * mm, "radius": 0.5 * mm});
            skCircle(sketch, "E97.50.11.0", {"center": v(-160.25, -32) * mm, "radius": 0.5 * mm});
            skCircle(sketch, "E97.52.11.0", {"center": v(-183.25, -34.5) * mm, "radius": 0.5 * mm});
            skCircle(sketch, "E97.54.11.0", {"center": v(-252.25, -34.5) * mm, "radius": 0.5 * mm});
            skCircle(sketch, "E97.56.11.0", {"center": v(-155.75, -34.5) * mm, "radius": 0.5 * mm});
            skCircle(sketch, "E97.58.11.0", {"center": v(-206.25, -37) * mm, "radius": 0.5 * mm});
            skCircle(sketch, "E97.60.11.0", {"center": v(-178.75, -34.5) * mm, "radius": 0.5 * mm});
            skCircle(sketch, "E97.62.11.0", {"center": v(-155.75, -32) * mm, "radius": 0.5 * mm});
            skCircle(sketch, "E97.64.11.0", {"center": v(-178.75, -37) * mm, "radius": 0.5 * mm});
            skCircle(sketch, "E97.66.11.0", {"center": v(-247.75, -34.5) * mm, "radius": 0.5 * mm});
            skCircle(sketch, "E97.68.11.0", {"center": v(-316.75, -37) * mm, "radius": 0.5 * mm});
            skCircle(sketch, "E97.70.11.0", {"center": v(-316.75, -32) * mm, "radius": 0.5 * mm});
            skCircle(sketch, "E97.72.11.0", {"center": v(-293.75, -32) * mm, "radius": 0.5 * mm});
            skCircle(sketch, "E97.74.11.0", {"center": v(-316.75, -34.5) * mm, "radius": 0.5 * mm});
            skCircle(sketch, "E97.76.11.0", {"center": v(-247.75, -37) * mm, "radius": 0.5 * mm});
            skCircle(sketch, "E97.78.11.0", {"center": v(-275.25, -32) * mm, "radius": 0.5 * mm});
            skCircle(sketch, "E97.80.11.0", {"center": v(-229.25, -34.5) * mm, "radius": 0.5 * mm});
            skCircle(sketch, "E97.82.11.0", {"center": v(-160.25, -37) * mm, "radius": 0.5 * mm});
            skCircle(sketch, "E97.84.11.0", {"center": v(-229.25, -37) * mm, "radius": 0.5 * mm});
            skCircle(sketch, "E97.86.11.0", {"center": v(-252.25, -32) * mm, "radius": 0.5 * mm});
            skCircle(sketch, "E97.88.11.0", {"center": v(-247.75, -32) * mm, "radius": 0.5 * mm});
            skCircle(sketch, "E97.90.11.0", {"center": v(-137.25, -34.5) * mm, "radius": 0.5 * mm});
            skCircle(sketch, "E97.92.11.0", {"center": v(-201.75, -32) * mm, "radius": 0.5 * mm});
            skCircle(sketch, "E97.94.11.0", {"center": v(-298.25, -32) * mm, "radius": 0.5 * mm});
            skCircle(sketch, "E97.96.11.0", {"center": v(-298.25, -34.5) * mm, "radius": 0.5 * mm});
            skCircle(sketch, "E97.98.11.0", {"center": v(-201.75, -34.5) * mm, "radius": 0.5 * mm});
            skCircle(sketch, "E97.100.11.0", {"center": v(-160.25, -34.5) * mm, "radius": 0.5 * mm});
            skCircle(sketch, "E97.102.11.0", {"center": v(-344.25, -37) * mm, "radius": 0.5 * mm});
            skCircle(sketch, "E97.104.11.0", {"center": v(-339.75, -37) * mm, "radius": 0.5 * mm});
            skCircle(sketch, "E97.106.11.0", {"center": v(-339.75, -32) * mm, "radius": 0.5 * mm});
            skCircle(sketch, "E97.108.11.0", {"center": v(-344.25, -34.5) * mm, "radius": 0.5 * mm});
            skCircle(sketch, "E97.110.11.0", {"center": v(-344.25, -32) * mm, "radius": 0.5 * mm});
            skCircle(sketch, "E97.112.11.0", {"center": v(-339.75, -34.5) * mm, "radius": 0.5 * mm});
            skCircle(sketch, "E97.114.11.0", {"center": v(-362.75, -37) * mm, "radius": 0.5 * mm});
            skCircle(sketch, "E97.116.11.0", {"center": v(-362.75, -32) * mm, "radius": 0.5 * mm});
            skCircle(sketch, "E97.118.11.0", {"center": v(-362.75, -34.5) * mm, "radius": 0.5 * mm});
            skCircle(sketch, "E97.0.12.0", {"center": v(-224.75, -60) * mm, "radius": 0.5 * mm});
            skCircle(sketch, "E97.2.12.0", {"center": v(-206.25, -57.5) * mm, "radius": 0.5 * mm});
            skCircle(sketch, "E97.4.12.0", {"center": v(-270.75, -60) * mm, "radius": 0.5 * mm});
            skCircle(sketch, "E97.6.12.0", {"center": v(-252.25, -60) * mm, "radius": 0.5 * mm});
            skCircle(sketch, "E97.8.12.0", {"center": v(-183.25, -55) * mm, "radius": 0.5 * mm});
            skCircle(sketch, "E97.10.12.0", {"center": v(-137.25, -60) * mm, "radius": 0.5 * mm});
            skCircle(sketch, "E97.12.12.0", {"center": v(-224.75, -57.5) * mm, "radius": 0.5 * mm});
            skCircle(sketch, "E97.14.12.0", {"center": v(-321.25, -60) * mm, "radius": 0.5 * mm});
            skCircle(sketch, "E97.16.12.0", {"center": v(-275.25, -60) * mm, "radius": 0.5 * mm});
            skCircle(sketch, "E97.18.12.0", {"center": v(-155.75, -60) * mm, "radius": 0.5 * mm});
            skCircle(sketch, "E97.20.12.0", {"center": v(-298.25, -60) * mm, "radius": 0.5 * mm});
            skCircle(sketch, "E97.22.12.0", {"center": v(-270.75, -57.5) * mm, "radius": 0.5 * mm});
            skCircle(sketch, "E97.24.12.0", {"center": v(-206.25, -55) * mm, "radius": 0.5 * mm});
            skCircle(sketch, "E97.26.12.0", {"center": v(-201.75, -60) * mm, "radius": 0.5 * mm});
            skCircle(sketch, "E97.28.12.0", {"center": v(-275.25, -57.5) * mm, "radius": 0.5 * mm});
            skCircle(sketch, "E97.30.12.0", {"center": v(-270.75, -55) * mm, "radius": 0.5 * mm});
            skCircle(sketch, "E97.32.12.0", {"center": v(-178.75, -55) * mm, "radius": 0.5 * mm});
            skCircle(sketch, "E97.34.12.0", {"center": v(-137.25, -55) * mm, "radius": 0.5 * mm});
            skCircle(sketch, "E97.36.12.0", {"center": v(-321.25, -55) * mm, "radius": 0.5 * mm});
            skCircle(sketch, "E97.38.12.0", {"center": v(-183.25, -60) * mm, "radius": 0.5 * mm});
            skCircle(sketch, "E97.40.12.0", {"center": v(-293.75, -57.5) * mm, "radius": 0.5 * mm});
            skCircle(sketch, "E97.42.12.0", {"center": v(-224.75, -55) * mm, "radius": 0.5 * mm});
            skCircle(sketch, "E97.44.12.0", {"center": v(-229.25, -55) * mm, "radius": 0.5 * mm});
            skCircle(sketch, "E97.46.12.0", {"center": v(-321.25, -57.5) * mm, "radius": 0.5 * mm});
            skCircle(sketch, "E97.48.12.0", {"center": v(-293.75, -60) * mm, "radius": 0.5 * mm});
            skCircle(sketch, "E97.50.12.0", {"center": v(-160.25, -55) * mm, "radius": 0.5 * mm});
            skCircle(sketch, "E97.52.12.0", {"center": v(-183.25, -57.5) * mm, "radius": 0.5 * mm});
            skCircle(sketch, "E97.54.12.0", {"center": v(-252.25, -57.5) * mm, "radius": 0.5 * mm});
            skCircle(sketch, "E97.56.12.0", {"center": v(-155.75, -57.5) * mm, "radius": 0.5 * mm});
            skCircle(sketch, "E97.58.12.0", {"center": v(-206.25, -60) * mm, "radius": 0.5 * mm});
            skCircle(sketch, "E97.60.12.0", {"center": v(-178.75, -57.5) * mm, "radius": 0.5 * mm});
            skCircle(sketch, "E97.62.12.0", {"center": v(-155.75, -55) * mm, "radius": 0.5 * mm});
            skCircle(sketch, "E97.64.12.0", {"center": v(-178.75, -60) * mm, "radius": 0.5 * mm});
            skCircle(sketch, "E97.66.12.0", {"center": v(-247.75, -57.5) * mm, "radius": 0.5 * mm});
            skCircle(sketch, "E97.68.12.0", {"center": v(-316.75, -60) * mm, "radius": 0.5 * mm});
            skCircle(sketch, "E97.70.12.0", {"center": v(-316.75, -55) * mm, "radius": 0.5 * mm});
            skCircle(sketch, "E97.72.12.0", {"center": v(-293.75, -55) * mm, "radius": 0.5 * mm});
            skCircle(sketch, "E97.74.12.0", {"center": v(-316.75, -57.5) * mm, "radius": 0.5 * mm});
            skCircle(sketch, "E97.76.12.0", {"center": v(-247.75, -60) * mm, "radius": 0.5 * mm});
            skCircle(sketch, "E97.78.12.0", {"center": v(-275.25, -55) * mm, "radius": 0.5 * mm});
            skCircle(sketch, "E97.80.12.0", {"center": v(-229.25, -57.5) * mm, "radius": 0.5 * mm});
            skCircle(sketch, "E97.82.12.0", {"center": v(-160.25, -60) * mm, "radius": 0.5 * mm});
            skCircle(sketch, "E97.84.12.0", {"center": v(-229.25, -60) * mm, "radius": 0.5 * mm});
            skCircle(sketch, "E97.86.12.0", {"center": v(-252.25, -55) * mm, "radius": 0.5 * mm});
            skCircle(sketch, "E97.88.12.0", {"center": v(-247.75, -55) * mm, "radius": 0.5 * mm});
            skCircle(sketch, "E97.90.12.0", {"center": v(-137.25, -57.5) * mm, "radius": 0.5 * mm});
            skCircle(sketch, "E97.92.12.0", {"center": v(-201.75, -55) * mm, "radius": 0.5 * mm});
            skCircle(sketch, "E97.94.12.0", {"center": v(-298.25, -55) * mm, "radius": 0.5 * mm});
            skCircle(sketch, "E97.96.12.0", {"center": v(-298.25, -57.5) * mm, "radius": 0.5 * mm});
            skCircle(sketch, "E97.98.12.0", {"center": v(-201.75, -57.5) * mm, "radius": 0.5 * mm});
            skCircle(sketch, "E97.100.12.0", {"center": v(-160.25, -57.5) * mm, "radius": 0.5 * mm});
            skCircle(sketch, "E97.102.12.0", {"center": v(-344.25, -60) * mm, "radius": 0.5 * mm});
            skCircle(sketch, "E97.104.12.0", {"center": v(-339.75, -60) * mm, "radius": 0.5 * mm});
            skCircle(sketch, "E97.106.12.0", {"center": v(-339.75, -55) * mm, "radius": 0.5 * mm});
            skCircle(sketch, "E97.108.12.0", {"center": v(-344.25, -57.5) * mm, "radius": 0.5 * mm});
            skCircle(sketch, "E97.110.12.0", {"center": v(-344.25, -55) * mm, "radius": 0.5 * mm});
            skCircle(sketch, "E97.112.12.0", {"center": v(-339.75, -57.5) * mm, "radius": 0.5 * mm});
            skCircle(sketch, "E97.114.12.0", {"center": v(-362.75, -60) * mm, "radius": 0.5 * mm});
            skCircle(sketch, "E97.116.12.0", {"center": v(-362.75, -55) * mm, "radius": 0.5 * mm});
            skCircle(sketch, "E97.118.12.0", {"center": v(-362.75, -57.5) * mm, "radius": 0.5 * mm});
            skCircle(sketch, "E97.0.13.0", {"center": v(-224.75, -83) * mm, "radius": 0.5 * mm});
            skCircle(sketch, "E97.2.13.0", {"center": v(-206.25, -80.5) * mm, "radius": 0.5 * mm});
            skCircle(sketch, "E97.4.13.0", {"center": v(-270.75, -83) * mm, "radius": 0.5 * mm});
            skCircle(sketch, "E97.6.13.0", {"center": v(-252.25, -83) * mm, "radius": 0.5 * mm});
            skCircle(sketch, "E97.8.13.0", {"center": v(-183.25, -78) * mm, "radius": 0.5 * mm});
            skCircle(sketch, "E97.10.13.0", {"center": v(-137.25, -83) * mm, "radius": 0.5 * mm});
            skCircle(sketch, "E97.12.13.0", {"center": v(-224.75, -80.5) * mm, "radius": 0.5 * mm});
            skCircle(sketch, "E97.14.13.0", {"center": v(-321.25, -83) * mm, "radius": 0.5 * mm});
            skCircle(sketch, "E97.16.13.0", {"center": v(-275.25, -83) * mm, "radius": 0.5 * mm});
            skCircle(sketch, "E97.18.13.0", {"center": v(-155.75, -83) * mm, "radius": 0.5 * mm});
            skCircle(sketch, "E97.20.13.0", {"center": v(-298.25, -83) * mm, "radius": 0.5 * mm});
            skCircle(sketch, "E97.22.13.0", {"center": v(-270.75, -80.5) * mm, "radius": 0.5 * mm});
            skCircle(sketch, "E97.24.13.0", {"center": v(-206.25, -78) * mm, "radius": 0.5 * mm});
            skCircle(sketch, "E97.26.13.0", {"center": v(-201.75, -83) * mm, "radius": 0.5 * mm});
            skCircle(sketch, "E97.28.13.0", {"center": v(-275.25, -80.5) * mm, "radius": 0.5 * mm});
            skCircle(sketch, "E97.30.13.0", {"center": v(-270.75, -78) * mm, "radius": 0.5 * mm});
            skCircle(sketch, "E97.32.13.0", {"center": v(-178.75, -78) * mm, "radius": 0.5 * mm});
            skCircle(sketch, "E97.34.13.0", {"center": v(-137.25, -78) * mm, "radius": 0.5 * mm});
            skCircle(sketch, "E97.36.13.0", {"center": v(-321.25, -78) * mm, "radius": 0.5 * mm});
            skCircle(sketch, "E97.38.13.0", {"center": v(-183.25, -83) * mm, "radius": 0.5 * mm});
            skCircle(sketch, "E97.40.13.0", {"center": v(-293.75, -80.5) * mm, "radius": 0.5 * mm});
            skCircle(sketch, "E97.42.13.0", {"center": v(-224.75, -78) * mm, "radius": 0.5 * mm});
            skCircle(sketch, "E97.44.13.0", {"center": v(-229.25, -78) * mm, "radius": 0.5 * mm});
            skCircle(sketch, "E97.46.13.0", {"center": v(-321.25, -80.5) * mm, "radius": 0.5 * mm});
            skCircle(sketch, "E97.48.13.0", {"center": v(-293.75, -83) * mm, "radius": 0.5 * mm});
            skCircle(sketch, "E97.50.13.0", {"center": v(-160.25, -78) * mm, "radius": 0.5 * mm});
            skCircle(sketch, "E97.52.13.0", {"center": v(-183.25, -80.5) * mm, "radius": 0.5 * mm});
            skCircle(sketch, "E97.54.13.0", {"center": v(-252.25, -80.5) * mm, "radius": 0.5 * mm});
            skCircle(sketch, "E97.56.13.0", {"center": v(-155.75, -80.5) * mm, "radius": 0.5 * mm});
            skCircle(sketch, "E97.58.13.0", {"center": v(-206.25, -83) * mm, "radius": 0.5 * mm});
            skCircle(sketch, "E97.60.13.0", {"center": v(-178.75, -80.5) * mm, "radius": 0.5 * mm});
            skCircle(sketch, "E97.62.13.0", {"center": v(-155.75, -78) * mm, "radius": 0.5 * mm});
            skCircle(sketch, "E97.64.13.0", {"center": v(-178.75, -83) * mm, "radius": 0.5 * mm});
            skCircle(sketch, "E97.66.13.0", {"center": v(-247.75, -80.5) * mm, "radius": 0.5 * mm});
            skCircle(sketch, "E97.68.13.0", {"center": v(-316.75, -83) * mm, "radius": 0.5 * mm});
            skCircle(sketch, "E97.70.13.0", {"center": v(-316.75, -78) * mm, "radius": 0.5 * mm});
            skCircle(sketch, "E97.72.13.0", {"center": v(-293.75, -78) * mm, "radius": 0.5 * mm});
            skCircle(sketch, "E97.74.13.0", {"center": v(-316.75, -80.5) * mm, "radius": 0.5 * mm});
            skCircle(sketch, "E97.76.13.0", {"center": v(-247.75, -83) * mm, "radius": 0.5 * mm});
            skCircle(sketch, "E97.78.13.0", {"center": v(-275.25, -78) * mm, "radius": 0.5 * mm});
            skCircle(sketch, "E97.80.13.0", {"center": v(-229.25, -80.5) * mm, "radius": 0.5 * mm});
            skCircle(sketch, "E97.82.13.0", {"center": v(-160.25, -83) * mm, "radius": 0.5 * mm});
            skCircle(sketch, "E97.84.13.0", {"center": v(-229.25, -83) * mm, "radius": 0.5 * mm});
            skCircle(sketch, "E97.86.13.0", {"center": v(-252.25, -78) * mm, "radius": 0.5 * mm});
            skCircle(sketch, "E97.88.13.0", {"center": v(-247.75, -78) * mm, "radius": 0.5 * mm});
            skCircle(sketch, "E97.90.13.0", {"center": v(-137.25, -80.5) * mm, "radius": 0.5 * mm});
            skCircle(sketch, "E97.92.13.0", {"center": v(-201.75, -78) * mm, "radius": 0.5 * mm});
            skCircle(sketch, "E97.94.13.0", {"center": v(-298.25, -78) * mm, "radius": 0.5 * mm});
            skCircle(sketch, "E97.96.13.0", {"center": v(-298.25, -80.5) * mm, "radius": 0.5 * mm});
            skCircle(sketch, "E97.98.13.0", {"center": v(-201.75, -80.5) * mm, "radius": 0.5 * mm});
            skCircle(sketch, "E97.100.13.0", {"center": v(-160.25, -80.5) * mm, "radius": 0.5 * mm});
            skCircle(sketch, "E97.102.13.0", {"center": v(-344.25, -83) * mm, "radius": 0.5 * mm});
            skCircle(sketch, "E97.104.13.0", {"center": v(-339.75, -83) * mm, "radius": 0.5 * mm});
            skCircle(sketch, "E97.106.13.0", {"center": v(-339.75, -78) * mm, "radius": 0.5 * mm});
            skCircle(sketch, "E97.108.13.0", {"center": v(-344.25, -80.5) * mm, "radius": 0.5 * mm});
            skCircle(sketch, "E97.110.13.0", {"center": v(-344.25, -78) * mm, "radius": 0.5 * mm});
            skCircle(sketch, "E97.112.13.0", {"center": v(-339.75, -80.5) * mm, "radius": 0.5 * mm});
            skCircle(sketch, "E97.114.13.0", {"center": v(-362.75, -83) * mm, "radius": 0.5 * mm});
            skCircle(sketch, "E97.116.13.0", {"center": v(-362.75, -78) * mm, "radius": 0.5 * mm});
            skCircle(sketch, "E97.118.13.0", {"center": v(-362.75, -80.5) * mm, "radius": 0.5 * mm});
            skCircle(sketch, "E97.0.14.0", {"center": v(-224.75, -106) * mm, "radius": 0.5 * mm});
            skCircle(sketch, "E97.2.14.0", {"center": v(-206.25, -103.5) * mm, "radius": 0.5 * mm});
            skCircle(sketch, "E97.4.14.0", {"center": v(-270.75, -106) * mm, "radius": 0.5 * mm});
            skCircle(sketch, "E97.6.14.0", {"center": v(-252.25, -106) * mm, "radius": 0.5 * mm});
            skCircle(sketch, "E97.8.14.0", {"center": v(-183.25, -101) * mm, "radius": 0.5 * mm});
            skCircle(sketch, "E97.10.14.0", {"center": v(-137.25, -106) * mm, "radius": 0.5 * mm});
            skCircle(sketch, "E97.12.14.0", {"center": v(-224.75, -103.5) * mm, "radius": 0.5 * mm});
            skCircle(sketch, "E97.14.14.0", {"center": v(-321.25, -106) * mm, "radius": 0.5 * mm});
            skCircle(sketch, "E97.16.14.0", {"center": v(-275.25, -106) * mm, "radius": 0.5 * mm});
            skCircle(sketch, "E97.18.14.0", {"center": v(-155.75, -106) * mm, "radius": 0.5 * mm});
            skCircle(sketch, "E97.20.14.0", {"center": v(-298.25, -106) * mm, "radius": 0.5 * mm});
            skCircle(sketch, "E97.22.14.0", {"center": v(-270.75, -103.5) * mm, "radius": 0.5 * mm});
            skCircle(sketch, "E97.24.14.0", {"center": v(-206.25, -101) * mm, "radius": 0.5 * mm});
            skCircle(sketch, "E97.26.14.0", {"center": v(-201.75, -106) * mm, "radius": 0.5 * mm});
            skCircle(sketch, "E97.28.14.0", {"center": v(-275.25, -103.5) * mm, "radius": 0.5 * mm});
            skCircle(sketch, "E97.30.14.0", {"center": v(-270.75, -101) * mm, "radius": 0.5 * mm});
            skCircle(sketch, "E97.32.14.0", {"center": v(-178.75, -101) * mm, "radius": 0.5 * mm});
            skCircle(sketch, "E97.34.14.0", {"center": v(-137.25, -101) * mm, "radius": 0.5 * mm});
            skCircle(sketch, "E97.36.14.0", {"center": v(-321.25, -101) * mm, "radius": 0.5 * mm});
            skCircle(sketch, "E97.38.14.0", {"center": v(-183.25, -106) * mm, "radius": 0.5 * mm});
            skCircle(sketch, "E97.40.14.0", {"center": v(-293.75, -103.5) * mm, "radius": 0.5 * mm});
            skCircle(sketch, "E97.42.14.0", {"center": v(-224.75, -101) * mm, "radius": 0.5 * mm});
            skCircle(sketch, "E97.44.14.0", {"center": v(-229.25, -101) * mm, "radius": 0.5 * mm});
            skCircle(sketch, "E97.46.14.0", {"center": v(-321.25, -103.5) * mm, "radius": 0.5 * mm});
            skCircle(sketch, "E97.48.14.0", {"center": v(-293.75, -106) * mm, "radius": 0.5 * mm});
            skCircle(sketch, "E97.50.14.0", {"center": v(-160.25, -101) * mm, "radius": 0.5 * mm});
            skCircle(sketch, "E97.52.14.0", {"center": v(-183.25, -103.5) * mm, "radius": 0.5 * mm});
            skCircle(sketch, "E97.54.14.0", {"center": v(-252.25, -103.5) * mm, "radius": 0.5 * mm});
            skCircle(sketch, "E97.56.14.0", {"center": v(-155.75, -103.5) * mm, "radius": 0.5 * mm});
            skCircle(sketch, "E97.58.14.0", {"center": v(-206.25, -106) * mm, "radius": 0.5 * mm});
            skCircle(sketch, "E97.60.14.0", {"center": v(-178.75, -103.5) * mm, "radius": 0.5 * mm});
            skCircle(sketch, "E97.62.14.0", {"center": v(-155.75, -101) * mm, "radius": 0.5 * mm});
            skCircle(sketch, "E97.64.14.0", {"center": v(-178.75, -106) * mm, "radius": 0.5 * mm});
            skCircle(sketch, "E97.66.14.0", {"center": v(-247.75, -103.5) * mm, "radius": 0.5 * mm});
            skCircle(sketch, "E97.68.14.0", {"center": v(-316.75, -106) * mm, "radius": 0.5 * mm});
            skCircle(sketch, "E97.70.14.0", {"center": v(-316.75, -101) * mm, "radius": 0.5 * mm});
            skCircle(sketch, "E97.72.14.0", {"center": v(-293.75, -101) * mm, "radius": 0.5 * mm});
            skCircle(sketch, "E97.74.14.0", {"center": v(-316.75, -103.5) * mm, "radius": 0.5 * mm});
            skCircle(sketch, "E97.76.14.0", {"center": v(-247.75, -106) * mm, "radius": 0.5 * mm});
            skCircle(sketch, "E97.78.14.0", {"center": v(-275.25, -101) * mm, "radius": 0.5 * mm});
            skCircle(sketch, "E97.80.14.0", {"center": v(-229.25, -103.5) * mm, "radius": 0.5 * mm});
            skCircle(sketch, "E97.82.14.0", {"center": v(-160.25, -106) * mm, "radius": 0.5 * mm});
            skCircle(sketch, "E97.84.14.0", {"center": v(-229.25, -106) * mm, "radius": 0.5 * mm});
            skCircle(sketch, "E97.86.14.0", {"center": v(-252.25, -101) * mm, "radius": 0.5 * mm});
            skCircle(sketch, "E97.88.14.0", {"center": v(-247.75, -101) * mm, "radius": 0.5 * mm});
            skCircle(sketch, "E97.90.14.0", {"center": v(-137.25, -103.5) * mm, "radius": 0.5 * mm});
            skCircle(sketch, "E97.92.14.0", {"center": v(-201.75, -101) * mm, "radius": 0.5 * mm});
            skCircle(sketch, "E97.94.14.0", {"center": v(-298.25, -101) * mm, "radius": 0.5 * mm});
            skCircle(sketch, "E97.96.14.0", {"center": v(-298.25, -103.5) * mm, "radius": 0.5 * mm});
            skCircle(sketch, "E97.98.14.0", {"center": v(-201.75, -103.5) * mm, "radius": 0.5 * mm});
            skCircle(sketch, "E97.100.14.0", {"center": v(-160.25, -103.5) * mm, "radius": 0.5 * mm});
            skCircle(sketch, "E97.102.14.0", {"center": v(-344.25, -106) * mm, "radius": 0.5 * mm});
            skCircle(sketch, "E97.104.14.0", {"center": v(-339.75, -106) * mm, "radius": 0.5 * mm});
            skCircle(sketch, "E97.106.14.0", {"center": v(-339.75, -101) * mm, "radius": 0.5 * mm});
            skCircle(sketch, "E97.108.14.0", {"center": v(-344.25, -103.5) * mm, "radius": 0.5 * mm});
            skCircle(sketch, "E97.110.14.0", {"center": v(-344.25, -101) * mm, "radius": 0.5 * mm});
            skCircle(sketch, "E97.112.14.0", {"center": v(-339.75, -103.5) * mm, "radius": 0.5 * mm});
            skCircle(sketch, "E97.114.14.0", {"center": v(-362.75, -106) * mm, "radius": 0.5 * mm});
            skCircle(sketch, "E97.116.14.0", {"center": v(-362.75, -101) * mm, "radius": 0.5 * mm});
            skCircle(sketch, "E97.118.14.0", {"center": v(-362.75, -103.5) * mm, "radius": 0.5 * mm});
            skCircle(sketch, "E97.0.15.0", {"center": v(-224.75, -129) * mm, "radius": 0.5 * mm});
            skCircle(sketch, "E97.2.15.0", {"center": v(-206.25, -126.5) * mm, "radius": 0.5 * mm});
            skCircle(sketch, "E97.4.15.0", {"center": v(-270.75, -129) * mm, "radius": 0.5 * mm});
            skCircle(sketch, "E97.6.15.0", {"center": v(-252.25, -129) * mm, "radius": 0.5 * mm});
            skCircle(sketch, "E97.8.15.0", {"center": v(-183.25, -124) * mm, "radius": 0.5 * mm});
            skCircle(sketch, "E97.10.15.0", {"center": v(-137.25, -129) * mm, "radius": 0.5 * mm});
            skCircle(sketch, "E97.12.15.0", {"center": v(-224.75, -126.5) * mm, "radius": 0.5 * mm});
            skCircle(sketch, "E97.14.15.0", {"center": v(-321.25, -129) * mm, "radius": 0.5 * mm});
            skCircle(sketch, "E97.16.15.0", {"center": v(-275.25, -129) * mm, "radius": 0.5 * mm});
            skCircle(sketch, "E97.18.15.0", {"center": v(-155.75, -129) * mm, "radius": 0.5 * mm});
            skCircle(sketch, "E97.20.15.0", {"center": v(-298.25, -129) * mm, "radius": 0.5 * mm});
            skCircle(sketch, "E97.22.15.0", {"center": v(-270.75, -126.5) * mm, "radius": 0.5 * mm});
            skCircle(sketch, "E97.24.15.0", {"center": v(-206.25, -124) * mm, "radius": 0.5 * mm});
            skCircle(sketch, "E97.26.15.0", {"center": v(-201.75, -129) * mm, "radius": 0.5 * mm});
            skCircle(sketch, "E97.28.15.0", {"center": v(-275.25, -126.5) * mm, "radius": 0.5 * mm});
            skCircle(sketch, "E97.30.15.0", {"center": v(-270.75, -124) * mm, "radius": 0.5 * mm});
            skCircle(sketch, "E97.32.15.0", {"center": v(-178.75, -124) * mm, "radius": 0.5 * mm});
            skCircle(sketch, "E97.34.15.0", {"center": v(-137.25, -124) * mm, "radius": 0.5 * mm});
            skCircle(sketch, "E97.36.15.0", {"center": v(-321.25, -124) * mm, "radius": 0.5 * mm});
            skCircle(sketch, "E97.38.15.0", {"center": v(-183.25, -129) * mm, "radius": 0.5 * mm});
            skCircle(sketch, "E97.40.15.0", {"center": v(-293.75, -126.5) * mm, "radius": 0.5 * mm});
            skCircle(sketch, "E97.42.15.0", {"center": v(-224.75, -124) * mm, "radius": 0.5 * mm});
            skCircle(sketch, "E97.44.15.0", {"center": v(-229.25, -124) * mm, "radius": 0.5 * mm});
            skCircle(sketch, "E97.46.15.0", {"center": v(-321.25, -126.5) * mm, "radius": 0.5 * mm});
            skCircle(sketch, "E97.48.15.0", {"center": v(-293.75, -129) * mm, "radius": 0.5 * mm});
            skCircle(sketch, "E97.50.15.0", {"center": v(-160.25, -124) * mm, "radius": 0.5 * mm});
            skCircle(sketch, "E97.52.15.0", {"center": v(-183.25, -126.5) * mm, "radius": 0.5 * mm});
            skCircle(sketch, "E97.54.15.0", {"center": v(-252.25, -126.5) * mm, "radius": 0.5 * mm});
            skCircle(sketch, "E97.56.15.0", {"center": v(-155.75, -126.5) * mm, "radius": 0.5 * mm});
            skCircle(sketch, "E97.58.15.0", {"center": v(-206.25, -129) * mm, "radius": 0.5 * mm});
            skCircle(sketch, "E97.60.15.0", {"center": v(-178.75, -126.5) * mm, "radius": 0.5 * mm});
            skCircle(sketch, "E97.62.15.0", {"center": v(-155.75, -124) * mm, "radius": 0.5 * mm});
            skCircle(sketch, "E97.64.15.0", {"center": v(-178.75, -129) * mm, "radius": 0.5 * mm});
            skCircle(sketch, "E97.66.15.0", {"center": v(-247.75, -126.5) * mm, "radius": 0.5 * mm});
            skCircle(sketch, "E97.68.15.0", {"center": v(-316.75, -129) * mm, "radius": 0.5 * mm});
            skCircle(sketch, "E97.70.15.0", {"center": v(-316.75, -124) * mm, "radius": 0.5 * mm});
            skCircle(sketch, "E97.72.15.0", {"center": v(-293.75, -124) * mm, "radius": 0.5 * mm});
            skCircle(sketch, "E97.74.15.0", {"center": v(-316.75, -126.5) * mm, "radius": 0.5 * mm});
            skCircle(sketch, "E97.76.15.0", {"center": v(-247.75, -129) * mm, "radius": 0.5 * mm});
            skCircle(sketch, "E97.78.15.0", {"center": v(-275.25, -124) * mm, "radius": 0.5 * mm});
            skCircle(sketch, "E97.80.15.0", {"center": v(-229.25, -126.5) * mm, "radius": 0.5 * mm});
            skCircle(sketch, "E97.82.15.0", {"center": v(-160.25, -129) * mm, "radius": 0.5 * mm});
            skCircle(sketch, "E97.84.15.0", {"center": v(-229.25, -129) * mm, "radius": 0.5 * mm});
            skCircle(sketch, "E97.86.15.0", {"center": v(-252.25, -124) * mm, "radius": 0.5 * mm});
            skCircle(sketch, "E97.88.15.0", {"center": v(-247.75, -124) * mm, "radius": 0.5 * mm});
            skCircle(sketch, "E97.90.15.0", {"center": v(-137.25, -126.5) * mm, "radius": 0.5 * mm});
            skCircle(sketch, "E97.92.15.0", {"center": v(-201.75, -124) * mm, "radius": 0.5 * mm});
            skCircle(sketch, "E97.94.15.0", {"center": v(-298.25, -124) * mm, "radius": 0.5 * mm});
            skCircle(sketch, "E97.96.15.0", {"center": v(-298.25, -126.5) * mm, "radius": 0.5 * mm});
            skCircle(sketch, "E97.98.15.0", {"center": v(-201.75, -126.5) * mm, "radius": 0.5 * mm});
            skCircle(sketch, "E97.100.15.0", {"center": v(-160.25, -126.5) * mm, "radius": 0.5 * mm});
            skCircle(sketch, "E97.102.15.0", {"center": v(-344.25, -129) * mm, "radius": 0.5 * mm});
            skCircle(sketch, "E97.104.15.0", {"center": v(-339.75, -129) * mm, "radius": 0.5 * mm});
            skCircle(sketch, "E97.106.15.0", {"center": v(-339.75, -124) * mm, "radius": 0.5 * mm});
            skCircle(sketch, "E97.108.15.0", {"center": v(-344.25, -126.5) * mm, "radius": 0.5 * mm});
            skCircle(sketch, "E97.110.15.0", {"center": v(-344.25, -124) * mm, "radius": 0.5 * mm});
            skCircle(sketch, "E97.112.15.0", {"center": v(-339.75, -126.5) * mm, "radius": 0.5 * mm});
            skCircle(sketch, "E97.114.15.0", {"center": v(-362.75, -129) * mm, "radius": 0.5 * mm});
            skCircle(sketch, "E97.116.15.0", {"center": v(-362.75, -124) * mm, "radius": 0.5 * mm});
            skCircle(sketch, "E97.118.15.0", {"center": v(-362.75, -126.5) * mm, "radius": 0.5 * mm});
            skCircle(sketch, "E97.0.16.0", {"center": v(-224.75, -152) * mm, "radius": 0.5 * mm});
            skCircle(sketch, "E97.2.16.0", {"center": v(-206.25, -149.5) * mm, "radius": 0.5 * mm});
            skCircle(sketch, "E97.4.16.0", {"center": v(-270.75, -152) * mm, "radius": 0.5 * mm});
            skCircle(sketch, "E97.6.16.0", {"center": v(-252.25, -152) * mm, "radius": 0.5 * mm});
            skCircle(sketch, "E97.8.16.0", {"center": v(-183.25, -147) * mm, "radius": 0.5 * mm});
            skCircle(sketch, "E97.10.16.0", {"center": v(-137.25, -152) * mm, "radius": 0.5 * mm});
            skCircle(sketch, "E97.12.16.0", {"center": v(-224.75, -149.5) * mm, "radius": 0.5 * mm});
            skCircle(sketch, "E97.14.16.0", {"center": v(-321.25, -152) * mm, "radius": 0.5 * mm});
            skCircle(sketch, "E97.16.16.0", {"center": v(-275.25, -152) * mm, "radius": 0.5 * mm});
            skCircle(sketch, "E97.18.16.0", {"center": v(-155.75, -152) * mm, "radius": 0.5 * mm});
            skCircle(sketch, "E97.20.16.0", {"center": v(-298.25, -152) * mm, "radius": 0.5 * mm});
            skCircle(sketch, "E97.22.16.0", {"center": v(-270.75, -149.5) * mm, "radius": 0.5 * mm});
            skCircle(sketch, "E97.24.16.0", {"center": v(-206.25, -147) * mm, "radius": 0.5 * mm});
            skCircle(sketch, "E97.26.16.0", {"center": v(-201.75, -152) * mm, "radius": 0.5 * mm});
            skCircle(sketch, "E97.28.16.0", {"center": v(-275.25, -149.5) * mm, "radius": 0.5 * mm});
            skCircle(sketch, "E97.30.16.0", {"center": v(-270.75, -147) * mm, "radius": 0.5 * mm});
            skCircle(sketch, "E97.32.16.0", {"center": v(-178.75, -147) * mm, "radius": 0.5 * mm});
            skCircle(sketch, "E97.34.16.0", {"center": v(-137.25, -147) * mm, "radius": 0.5 * mm});
            skCircle(sketch, "E97.36.16.0", {"center": v(-321.25, -147) * mm, "radius": 0.5 * mm});
            skCircle(sketch, "E97.38.16.0", {"center": v(-183.25, -152) * mm, "radius": 0.5 * mm});
            skCircle(sketch, "E97.40.16.0", {"center": v(-293.75, -149.5) * mm, "radius": 0.5 * mm});
            skCircle(sketch, "E97.42.16.0", {"center": v(-224.75, -147) * mm, "radius": 0.5 * mm});
            skCircle(sketch, "E97.44.16.0", {"center": v(-229.25, -147) * mm, "radius": 0.5 * mm});
            skCircle(sketch, "E97.46.16.0", {"center": v(-321.25, -149.5) * mm, "radius": 0.5 * mm});
            skCircle(sketch, "E97.48.16.0", {"center": v(-293.75, -152) * mm, "radius": 0.5 * mm});
            skCircle(sketch, "E97.50.16.0", {"center": v(-160.25, -147) * mm, "radius": 0.5 * mm});
            skCircle(sketch, "E97.52.16.0", {"center": v(-183.25, -149.5) * mm, "radius": 0.5 * mm});
            skCircle(sketch, "E97.54.16.0", {"center": v(-252.25, -149.5) * mm, "radius": 0.5 * mm});
            skCircle(sketch, "E97.56.16.0", {"center": v(-155.75, -149.5) * mm, "radius": 0.5 * mm});
            skCircle(sketch, "E97.58.16.0", {"center": v(-206.25, -152) * mm, "radius": 0.5 * mm});
            skCircle(sketch, "E97.60.16.0", {"center": v(-178.75, -149.5) * mm, "radius": 0.5 * mm});
            skCircle(sketch, "E97.62.16.0", {"center": v(-155.75, -147) * mm, "radius": 0.5 * mm});
            skCircle(sketch, "E97.64.16.0", {"center": v(-178.75, -152) * mm, "radius": 0.5 * mm});
            skCircle(sketch, "E97.66.16.0", {"center": v(-247.75, -149.5) * mm, "radius": 0.5 * mm});
            skCircle(sketch, "E97.68.16.0", {"center": v(-316.75, -152) * mm, "radius": 0.5 * mm});
            skCircle(sketch, "E97.70.16.0", {"center": v(-316.75, -147) * mm, "radius": 0.5 * mm});
            skCircle(sketch, "E97.72.16.0", {"center": v(-293.75, -147) * mm, "radius": 0.5 * mm});
            skCircle(sketch, "E97.74.16.0", {"center": v(-316.75, -149.5) * mm, "radius": 0.5 * mm});
            skCircle(sketch, "E97.76.16.0", {"center": v(-247.75, -152) * mm, "radius": 0.5 * mm});
            skCircle(sketch, "E97.78.16.0", {"center": v(-275.25, -147) * mm, "radius": 0.5 * mm});
            skCircle(sketch, "E97.80.16.0", {"center": v(-229.25, -149.5) * mm, "radius": 0.5 * mm});
            skCircle(sketch, "E97.82.16.0", {"center": v(-160.25, -152) * mm, "radius": 0.5 * mm});
            skCircle(sketch, "E97.84.16.0", {"center": v(-229.25, -152) * mm, "radius": 0.5 * mm});
            skCircle(sketch, "E97.86.16.0", {"center": v(-252.25, -147) * mm, "radius": 0.5 * mm});
            skCircle(sketch, "E97.88.16.0", {"center": v(-247.75, -147) * mm, "radius": 0.5 * mm});
            skCircle(sketch, "E97.90.16.0", {"center": v(-137.25, -149.5) * mm, "radius": 0.5 * mm});
            skCircle(sketch, "E97.92.16.0", {"center": v(-201.75, -147) * mm, "radius": 0.5 * mm});
            skCircle(sketch, "E97.94.16.0", {"center": v(-298.25, -147) * mm, "radius": 0.5 * mm});
            skCircle(sketch, "E97.96.16.0", {"center": v(-298.25, -149.5) * mm, "radius": 0.5 * mm});
            skCircle(sketch, "E97.98.16.0", {"center": v(-201.75, -149.5) * mm, "radius": 0.5 * mm});
            skCircle(sketch, "E97.100.16.0", {"center": v(-160.25, -149.5) * mm, "radius": 0.5 * mm});
            skCircle(sketch, "E97.102.16.0", {"center": v(-344.25, -152) * mm, "radius": 0.5 * mm});
            skCircle(sketch, "E97.104.16.0", {"center": v(-339.75, -152) * mm, "radius": 0.5 * mm});
            skCircle(sketch, "E97.106.16.0", {"center": v(-339.75, -147) * mm, "radius": 0.5 * mm});
            skCircle(sketch, "E97.108.16.0", {"center": v(-344.25, -149.5) * mm, "radius": 0.5 * mm});
            skCircle(sketch, "E97.110.16.0", {"center": v(-344.25, -147) * mm, "radius": 0.5 * mm});
            skCircle(sketch, "E97.112.16.0", {"center": v(-339.75, -149.5) * mm, "radius": 0.5 * mm});
            skCircle(sketch, "E97.114.16.0", {"center": v(-362.75, -152) * mm, "radius": 0.5 * mm});
            skCircle(sketch, "E97.116.16.0", {"center": v(-362.75, -147) * mm, "radius": 0.5 * mm});
            skCircle(sketch, "E97.118.16.0", {"center": v(-362.75, -149.5) * mm, "radius": 0.5 * mm});
            skCircle(sketch, "E97.0.17.0", {"center": v(-224.75, -175) * mm, "radius": 0.5 * mm});
            skCircle(sketch, "E97.2.17.0", {"center": v(-206.25, -172.5) * mm, "radius": 0.5 * mm});
            skCircle(sketch, "E97.4.17.0", {"center": v(-270.75, -175) * mm, "radius": 0.5 * mm});
            skCircle(sketch, "E97.6.17.0", {"center": v(-252.25, -175) * mm, "radius": 0.5 * mm});
            skCircle(sketch, "E97.8.17.0", {"center": v(-183.25, -170) * mm, "radius": 0.5 * mm});
            skCircle(sketch, "E97.10.17.0", {"center": v(-137.25, -175) * mm, "radius": 0.5 * mm});
            skCircle(sketch, "E97.12.17.0", {"center": v(-224.75, -172.5) * mm, "radius": 0.5 * mm});
            skCircle(sketch, "E97.14.17.0", {"center": v(-321.25, -175) * mm, "radius": 0.5 * mm});
            skCircle(sketch, "E97.16.17.0", {"center": v(-275.25, -175) * mm, "radius": 0.5 * mm});
            skCircle(sketch, "E97.18.17.0", {"center": v(-155.75, -175) * mm, "radius": 0.5 * mm});
            skCircle(sketch, "E97.20.17.0", {"center": v(-298.25, -175) * mm, "radius": 0.5 * mm});
            skCircle(sketch, "E97.22.17.0", {"center": v(-270.75, -172.5) * mm, "radius": 0.5 * mm});
            skCircle(sketch, "E97.24.17.0", {"center": v(-206.25, -170) * mm, "radius": 0.5 * mm});
            skCircle(sketch, "E97.26.17.0", {"center": v(-201.75, -175) * mm, "radius": 0.5 * mm});
            skCircle(sketch, "E97.28.17.0", {"center": v(-275.25, -172.5) * mm, "radius": 0.5 * mm});
            skCircle(sketch, "E97.30.17.0", {"center": v(-270.75, -170) * mm, "radius": 0.5 * mm});
            skCircle(sketch, "E97.32.17.0", {"center": v(-178.75, -170) * mm, "radius": 0.5 * mm});
            skCircle(sketch, "E97.34.17.0", {"center": v(-137.25, -170) * mm, "radius": 0.5 * mm});
            skCircle(sketch, "E97.36.17.0", {"center": v(-321.25, -170) * mm, "radius": 0.5 * mm});
            skCircle(sketch, "E97.38.17.0", {"center": v(-183.25, -175) * mm, "radius": 0.5 * mm});
            skCircle(sketch, "E97.40.17.0", {"center": v(-293.75, -172.5) * mm, "radius": 0.5 * mm});
            skCircle(sketch, "E97.42.17.0", {"center": v(-224.75, -170) * mm, "radius": 0.5 * mm});
            skCircle(sketch, "E97.44.17.0", {"center": v(-229.25, -170) * mm, "radius": 0.5 * mm});
            skCircle(sketch, "E97.46.17.0", {"center": v(-321.25, -172.5) * mm, "radius": 0.5 * mm});
            skCircle(sketch, "E97.48.17.0", {"center": v(-293.75, -175) * mm, "radius": 0.5 * mm});
            skCircle(sketch, "E97.50.17.0", {"center": v(-160.25, -170) * mm, "radius": 0.5 * mm});
            skCircle(sketch, "E97.52.17.0", {"center": v(-183.25, -172.5) * mm, "radius": 0.5 * mm});
            skCircle(sketch, "E97.54.17.0", {"center": v(-252.25, -172.5) * mm, "radius": 0.5 * mm});
            skCircle(sketch, "E97.56.17.0", {"center": v(-155.75, -172.5) * mm, "radius": 0.5 * mm});
            skCircle(sketch, "E97.58.17.0", {"center": v(-206.25, -175) * mm, "radius": 0.5 * mm});
            skCircle(sketch, "E97.60.17.0", {"center": v(-178.75, -172.5) * mm, "radius": 0.5 * mm});
            skCircle(sketch, "E97.62.17.0", {"center": v(-155.75, -170) * mm, "radius": 0.5 * mm});
            skCircle(sketch, "E97.64.17.0", {"center": v(-178.75, -175) * mm, "radius": 0.5 * mm});
            skCircle(sketch, "E97.66.17.0", {"center": v(-247.75, -172.5) * mm, "radius": 0.5 * mm});
            skCircle(sketch, "E97.68.17.0", {"center": v(-316.75, -175) * mm, "radius": 0.5 * mm});
            skCircle(sketch, "E97.70.17.0", {"center": v(-316.75, -170) * mm, "radius": 0.5 * mm});
            skCircle(sketch, "E97.72.17.0", {"center": v(-293.75, -170) * mm, "radius": 0.5 * mm});
            skCircle(sketch, "E97.74.17.0", {"center": v(-316.75, -172.5) * mm, "radius": 0.5 * mm});
            skCircle(sketch, "E97.76.17.0", {"center": v(-247.75, -175) * mm, "radius": 0.5 * mm});
            skCircle(sketch, "E97.78.17.0", {"center": v(-275.25, -170) * mm, "radius": 0.5 * mm});
            skCircle(sketch, "E97.80.17.0", {"center": v(-229.25, -172.5) * mm, "radius": 0.5 * mm});
            skCircle(sketch, "E97.82.17.0", {"center": v(-160.25, -175) * mm, "radius": 0.5 * mm});
            skCircle(sketch, "E97.84.17.0", {"center": v(-229.25, -175) * mm, "radius": 0.5 * mm});
            skCircle(sketch, "E97.86.17.0", {"center": v(-252.25, -170) * mm, "radius": 0.5 * mm});
            skCircle(sketch, "E97.88.17.0", {"center": v(-247.75, -170) * mm, "radius": 0.5 * mm});
            skCircle(sketch, "E97.90.17.0", {"center": v(-137.25, -172.5) * mm, "radius": 0.5 * mm});
            skCircle(sketch, "E97.92.17.0", {"center": v(-201.75, -170) * mm, "radius": 0.5 * mm});
            skCircle(sketch, "E97.94.17.0", {"center": v(-298.25, -170) * mm, "radius": 0.5 * mm});
            skCircle(sketch, "E97.96.17.0", {"center": v(-298.25, -172.5) * mm, "radius": 0.5 * mm});
            skCircle(sketch, "E97.98.17.0", {"center": v(-201.75, -172.5) * mm, "radius": 0.5 * mm});
            skCircle(sketch, "E97.100.17.0", {"center": v(-160.25, -172.5) * mm, "radius": 0.5 * mm});
            skCircle(sketch, "E97.102.17.0", {"center": v(-344.25, -175) * mm, "radius": 0.5 * mm});
            skCircle(sketch, "E97.104.17.0", {"center": v(-339.75, -175) * mm, "radius": 0.5 * mm});
            skCircle(sketch, "E97.106.17.0", {"center": v(-339.75, -170) * mm, "radius": 0.5 * mm});
            skCircle(sketch, "E97.108.17.0", {"center": v(-344.25, -172.5) * mm, "radius": 0.5 * mm});
            skCircle(sketch, "E97.110.17.0", {"center": v(-344.25, -170) * mm, "radius": 0.5 * mm});
            skCircle(sketch, "E97.112.17.0", {"center": v(-339.75, -172.5) * mm, "radius": 0.5 * mm});
            skCircle(sketch, "E97.114.17.0", {"center": v(-362.75, -175) * mm, "radius": 0.5 * mm});
            skCircle(sketch, "E97.116.17.0", {"center": v(-362.75, -170) * mm, "radius": 0.5 * mm});
            skCircle(sketch, "E97.118.17.0", {"center": v(-362.75, -172.5) * mm, "radius": 0.5 * mm});
            skCircle(sketch, "E97.0.18.0", {"center": v(-224.75, -198) * mm, "radius": 0.5 * mm});
            skCircle(sketch, "E97.2.18.0", {"center": v(-206.25, -195.5) * mm, "radius": 0.5 * mm});
            skCircle(sketch, "E97.4.18.0", {"center": v(-270.75, -198) * mm, "radius": 0.5 * mm});
            skCircle(sketch, "E97.6.18.0", {"center": v(-252.25, -198) * mm, "radius": 0.5 * mm});
            skCircle(sketch, "E97.8.18.0", {"center": v(-183.25, -193) * mm, "radius": 0.5 * mm});
            skCircle(sketch, "E97.10.18.0", {"center": v(-137.25, -198) * mm, "radius": 0.5 * mm});
            skCircle(sketch, "E97.12.18.0", {"center": v(-224.75, -195.5) * mm, "radius": 0.5 * mm});
            skCircle(sketch, "E97.14.18.0", {"center": v(-321.25, -198) * mm, "radius": 0.5 * mm});
            skCircle(sketch, "E97.16.18.0", {"center": v(-275.25, -198) * mm, "radius": 0.5 * mm});
            skCircle(sketch, "E97.18.18.0", {"center": v(-155.75, -198) * mm, "radius": 0.5 * mm});
            skCircle(sketch, "E97.20.18.0", {"center": v(-298.25, -198) * mm, "radius": 0.5 * mm});
            skCircle(sketch, "E97.22.18.0", {"center": v(-270.75, -195.5) * mm, "radius": 0.5 * mm});
            skCircle(sketch, "E97.24.18.0", {"center": v(-206.25, -193) * mm, "radius": 0.5 * mm});
            skCircle(sketch, "E97.26.18.0", {"center": v(-201.75, -198) * mm, "radius": 0.5 * mm});
            skCircle(sketch, "E97.28.18.0", {"center": v(-275.25, -195.5) * mm, "radius": 0.5 * mm});
            skCircle(sketch, "E97.30.18.0", {"center": v(-270.75, -193) * mm, "radius": 0.5 * mm});
            skCircle(sketch, "E97.32.18.0", {"center": v(-178.75, -193) * mm, "radius": 0.5 * mm});
            skCircle(sketch, "E97.34.18.0", {"center": v(-137.25, -193) * mm, "radius": 0.5 * mm});
            skCircle(sketch, "E97.36.18.0", {"center": v(-321.25, -193) * mm, "radius": 0.5 * mm});
            skCircle(sketch, "E97.38.18.0", {"center": v(-183.25, -198) * mm, "radius": 0.5 * mm});
            skCircle(sketch, "E97.40.18.0", {"center": v(-293.75, -195.5) * mm, "radius": 0.5 * mm});
            skCircle(sketch, "E97.42.18.0", {"center": v(-224.75, -193) * mm, "radius": 0.5 * mm});
            skCircle(sketch, "E97.44.18.0", {"center": v(-229.25, -193) * mm, "radius": 0.5 * mm});
            skCircle(sketch, "E97.46.18.0", {"center": v(-321.25, -195.5) * mm, "radius": 0.5 * mm});
            skCircle(sketch, "E97.48.18.0", {"center": v(-293.75, -198) * mm, "radius": 0.5 * mm});
            skCircle(sketch, "E97.50.18.0", {"center": v(-160.25, -193) * mm, "radius": 0.5 * mm});
            skCircle(sketch, "E97.52.18.0", {"center": v(-183.25, -195.5) * mm, "radius": 0.5 * mm});
            skCircle(sketch, "E97.54.18.0", {"center": v(-252.25, -195.5) * mm, "radius": 0.5 * mm});
            skCircle(sketch, "E97.56.18.0", {"center": v(-155.75, -195.5) * mm, "radius": 0.5 * mm});
            skCircle(sketch, "E97.58.18.0", {"center": v(-206.25, -198) * mm, "radius": 0.5 * mm});
            skCircle(sketch, "E97.60.18.0", {"center": v(-178.75, -195.5) * mm, "radius": 0.5 * mm});
            skCircle(sketch, "E97.62.18.0", {"center": v(-155.75, -193) * mm, "radius": 0.5 * mm});
            skCircle(sketch, "E97.64.18.0", {"center": v(-178.75, -198) * mm, "radius": 0.5 * mm});
            skCircle(sketch, "E97.66.18.0", {"center": v(-247.75, -195.5) * mm, "radius": 0.5 * mm});
            skCircle(sketch, "E97.68.18.0", {"center": v(-316.75, -198) * mm, "radius": 0.5 * mm});
            skCircle(sketch, "E97.70.18.0", {"center": v(-316.75, -193) * mm, "radius": 0.5 * mm});
            skCircle(sketch, "E97.72.18.0", {"center": v(-293.75, -193) * mm, "radius": 0.5 * mm});
            skCircle(sketch, "E97.74.18.0", {"center": v(-316.75, -195.5) * mm, "radius": 0.5 * mm});
            skCircle(sketch, "E97.76.18.0", {"center": v(-247.75, -198) * mm, "radius": 0.5 * mm});
            skCircle(sketch, "E97.78.18.0", {"center": v(-275.25, -193) * mm, "radius": 0.5 * mm});
            skCircle(sketch, "E97.80.18.0", {"center": v(-229.25, -195.5) * mm, "radius": 0.5 * mm});
            skCircle(sketch, "E97.82.18.0", {"center": v(-160.25, -198) * mm, "radius": 0.5 * mm});
            skCircle(sketch, "E97.84.18.0", {"center": v(-229.25, -198) * mm, "radius": 0.5 * mm});
            skCircle(sketch, "E97.86.18.0", {"center": v(-252.25, -193) * mm, "radius": 0.5 * mm});
            skCircle(sketch, "E97.88.18.0", {"center": v(-247.75, -193) * mm, "radius": 0.5 * mm});
            skCircle(sketch, "E97.90.18.0", {"center": v(-137.25, -195.5) * mm, "radius": 0.5 * mm});
            skCircle(sketch, "E97.92.18.0", {"center": v(-201.75, -193) * mm, "radius": 0.5 * mm});
            skCircle(sketch, "E97.94.18.0", {"center": v(-298.25, -193) * mm, "radius": 0.5 * mm});
            skCircle(sketch, "E97.96.18.0", {"center": v(-298.25, -195.5) * mm, "radius": 0.5 * mm});
            skCircle(sketch, "E97.98.18.0", {"center": v(-201.75, -195.5) * mm, "radius": 0.5 * mm});
            skCircle(sketch, "E97.100.18.0", {"center": v(-160.25, -195.5) * mm, "radius": 0.5 * mm});
            skCircle(sketch, "E97.102.18.0", {"center": v(-344.25, -198) * mm, "radius": 0.5 * mm});
            skCircle(sketch, "E97.104.18.0", {"center": v(-339.75, -198) * mm, "radius": 0.5 * mm});
            skCircle(sketch, "E97.106.18.0", {"center": v(-339.75, -193) * mm, "radius": 0.5 * mm});
            skCircle(sketch, "E97.108.18.0", {"center": v(-344.25, -195.5) * mm, "radius": 0.5 * mm});
            skCircle(sketch, "E97.110.18.0", {"center": v(-344.25, -193) * mm, "radius": 0.5 * mm});
            skCircle(sketch, "E97.112.18.0", {"center": v(-339.75, -195.5) * mm, "radius": 0.5 * mm});
            skCircle(sketch, "E97.114.18.0", {"center": v(-362.75, -198) * mm, "radius": 0.5 * mm});
            skCircle(sketch, "E97.116.18.0", {"center": v(-362.75, -193) * mm, "radius": 0.5 * mm});
            skCircle(sketch, "E97.118.18.0", {"center": v(-362.75, -195.5) * mm, "radius": 0.5 * mm});
            skCircle(sketch, "E97.0.19.0", {"center": v(-224.75, -221) * mm, "radius": 0.5 * mm});
            skCircle(sketch, "E97.2.19.0", {"center": v(-206.25, -218.5) * mm, "radius": 0.5 * mm});
            skCircle(sketch, "E97.4.19.0", {"center": v(-270.75, -221) * mm, "radius": 0.5 * mm});
            skCircle(sketch, "E97.6.19.0", {"center": v(-252.25, -221) * mm, "radius": 0.5 * mm});
            skCircle(sketch, "E97.8.19.0", {"center": v(-183.25, -216) * mm, "radius": 0.5 * mm});
            skCircle(sketch, "E97.10.19.0", {"center": v(-137.25, -221) * mm, "radius": 0.5 * mm});
            skCircle(sketch, "E97.12.19.0", {"center": v(-224.75, -218.5) * mm, "radius": 0.5 * mm});
            skCircle(sketch, "E97.14.19.0", {"center": v(-321.25, -221) * mm, "radius": 0.5 * mm});
            skCircle(sketch, "E97.16.19.0", {"center": v(-275.25, -221) * mm, "radius": 0.5 * mm});
            skCircle(sketch, "E97.18.19.0", {"center": v(-155.75, -221) * mm, "radius": 0.5 * mm});
            skCircle(sketch, "E97.20.19.0", {"center": v(-298.25, -221) * mm, "radius": 0.5 * mm});
            skCircle(sketch, "E97.22.19.0", {"center": v(-270.75, -218.5) * mm, "radius": 0.5 * mm});
            skCircle(sketch, "E97.24.19.0", {"center": v(-206.25, -216) * mm, "radius": 0.5 * mm});
            skCircle(sketch, "E97.26.19.0", {"center": v(-201.75, -221) * mm, "radius": 0.5 * mm});
            skCircle(sketch, "E97.28.19.0", {"center": v(-275.25, -218.5) * mm, "radius": 0.5 * mm});
            skCircle(sketch, "E97.30.19.0", {"center": v(-270.75, -216) * mm, "radius": 0.5 * mm});
            skCircle(sketch, "E97.32.19.0", {"center": v(-178.75, -216) * mm, "radius": 0.5 * mm});
            skCircle(sketch, "E97.34.19.0", {"center": v(-137.25, -216) * mm, "radius": 0.5 * mm});
            skCircle(sketch, "E97.36.19.0", {"center": v(-321.25, -216) * mm, "radius": 0.5 * mm});
            skCircle(sketch, "E97.38.19.0", {"center": v(-183.25, -221) * mm, "radius": 0.5 * mm});
            skCircle(sketch, "E97.40.19.0", {"center": v(-293.75, -218.5) * mm, "radius": 0.5 * mm});
            skCircle(sketch, "E97.42.19.0", {"center": v(-224.75, -216) * mm, "radius": 0.5 * mm});
            skCircle(sketch, "E97.44.19.0", {"center": v(-229.25, -216) * mm, "radius": 0.5 * mm});
            skCircle(sketch, "E97.46.19.0", {"center": v(-321.25, -218.5) * mm, "radius": 0.5 * mm});
            skCircle(sketch, "E97.48.19.0", {"center": v(-293.75, -221) * mm, "radius": 0.5 * mm});
            skCircle(sketch, "E97.50.19.0", {"center": v(-160.25, -216) * mm, "radius": 0.5 * mm});
            skCircle(sketch, "E97.52.19.0", {"center": v(-183.25, -218.5) * mm, "radius": 0.5 * mm});
            skCircle(sketch, "E97.54.19.0", {"center": v(-252.25, -218.5) * mm, "radius": 0.5 * mm});
            skCircle(sketch, "E97.56.19.0", {"center": v(-155.75, -218.5) * mm, "radius": 0.5 * mm});
            skCircle(sketch, "E97.58.19.0", {"center": v(-206.25, -221) * mm, "radius": 0.5 * mm});
            skCircle(sketch, "E97.60.19.0", {"center": v(-178.75, -218.5) * mm, "radius": 0.5 * mm});
            skCircle(sketch, "E97.62.19.0", {"center": v(-155.75, -216) * mm, "radius": 0.5 * mm});
            skCircle(sketch, "E97.64.19.0", {"center": v(-178.75, -221) * mm, "radius": 0.5 * mm});
            skCircle(sketch, "E97.66.19.0", {"center": v(-247.75, -218.5) * mm, "radius": 0.5 * mm});
            skCircle(sketch, "E97.68.19.0", {"center": v(-316.75, -221) * mm, "radius": 0.5 * mm});
            skCircle(sketch, "E97.70.19.0", {"center": v(-316.75, -216) * mm, "radius": 0.5 * mm});
            skCircle(sketch, "E97.72.19.0", {"center": v(-293.75, -216) * mm, "radius": 0.5 * mm});
            skCircle(sketch, "E97.74.19.0", {"center": v(-316.75, -218.5) * mm, "radius": 0.5 * mm});
            skCircle(sketch, "E97.76.19.0", {"center": v(-247.75, -221) * mm, "radius": 0.5 * mm});
            skCircle(sketch, "E97.78.19.0", {"center": v(-275.25, -216) * mm, "radius": 0.5 * mm});
            skCircle(sketch, "E97.80.19.0", {"center": v(-229.25, -218.5) * mm, "radius": 0.5 * mm});
            skCircle(sketch, "E97.82.19.0", {"center": v(-160.25, -221) * mm, "radius": 0.5 * mm});
            skCircle(sketch, "E97.84.19.0", {"center": v(-229.25, -221) * mm, "radius": 0.5 * mm});
            skCircle(sketch, "E97.86.19.0", {"center": v(-252.25, -216) * mm, "radius": 0.5 * mm});
            skCircle(sketch, "E97.88.19.0", {"center": v(-247.75, -216) * mm, "radius": 0.5 * mm});
            skCircle(sketch, "E97.90.19.0", {"center": v(-137.25, -218.5) * mm, "radius": 0.5 * mm});
            skCircle(sketch, "E97.92.19.0", {"center": v(-201.75, -216) * mm, "radius": 0.5 * mm});
            skCircle(sketch, "E97.94.19.0", {"center": v(-298.25, -216) * mm, "radius": 0.5 * mm});
            skCircle(sketch, "E97.96.19.0", {"center": v(-298.25, -218.5) * mm, "radius": 0.5 * mm});
            skCircle(sketch, "E97.98.19.0", {"center": v(-201.75, -218.5) * mm, "radius": 0.5 * mm});
            skCircle(sketch, "E97.100.19.0", {"center": v(-160.25, -218.5) * mm, "radius": 0.5 * mm});
            skCircle(sketch, "E97.102.19.0", {"center": v(-344.25, -221) * mm, "radius": 0.5 * mm});
            skCircle(sketch, "E97.104.19.0", {"center": v(-339.75, -221) * mm, "radius": 0.5 * mm});
            skCircle(sketch, "E97.106.19.0", {"center": v(-339.75, -216) * mm, "radius": 0.5 * mm});
            skCircle(sketch, "E97.108.19.0", {"center": v(-344.25, -218.5) * mm, "radius": 0.5 * mm});
            skCircle(sketch, "E97.110.19.0", {"center": v(-344.25, -216) * mm, "radius": 0.5 * mm});
            skCircle(sketch, "E97.112.19.0", {"center": v(-339.75, -218.5) * mm, "radius": 0.5 * mm});
            skCircle(sketch, "E97.114.19.0", {"center": v(-362.75, -221) * mm, "radius": 0.5 * mm});
            skCircle(sketch, "E97.116.19.0", {"center": v(-362.75, -216) * mm, "radius": 0.5 * mm});
            skCircle(sketch, "E97.118.19.0", {"center": v(-362.75, -218.5) * mm, "radius": 0.5 * mm});
            skSolve(sketch);
        }
        {
            var Q0;
            Q0=makeQuery(id+"F15.imprint","IMPRINT",FACE,{"disambiguationData":[TD([[makeQuery(id+"F15.imprint","IMPRINT",EDGE,{"derivedFrom":sQuery(id+"F15.wireOp",EDGE,"E84.bottom")}),1.0]])]});
            var Q1;
            Q1=makeQuery(id+"F15.imprint","IMPRINT",FACE,{"disambiguationData":[TD([[makeQuery(id+"F15.imprint","IMPRINT",EDGE,{"derivedFrom":sQuery(id+"F15.wireOp",EDGE,"E83.bottom")}),1.0]])]});
            var Q2;
            Q2=makeQuery(id+"F15.imprint","IMPRINT",FACE,{"disambiguationData":[TD([[makeQuery(id+"F15.imprint","IMPRINT",EDGE,{"derivedFrom":sQuery(id+"F15.wireOp",EDGE,"E85.bottom")}),1.0]])]});
            extrude(context, id + "F16", {"entities" : qUnion([Q0, Q1, Q2]), "depth" : (getVariable(context, 'Thickness')) * mm});
        }
        {
            var Q0;
            Q0=qCreatedBy(makeId("Top.planeOp"),FACE);
            var sketch = newSketch(context, id + "F17", { "sketchPlane" : qUnion([Q0])});
            skLineSegment(sketch, "E98.bottom", {"start": v(-453, 9) * mm, "end": v(-680, 9) * mm});
            skLineSegment(sketch, "E98.top", {"start": v(-453, -9) * mm, "end": v(-680, -9) * mm});
            skLineSegment(sketch, "E98.left", {"start": v(-450, 5) * mm, "end": v(-450, -5) * mm});
            skPoint(sketch, "E98.middle", {"position": v(-565, 0) * mm});
            skLineSegment(sketch, "E99", {"start": v(-453, -9) * mm, "end": v(-453, -5) * mm});
            skLineSegment(sketch, "E100", {"start": v(-453, -5) * mm, "end": v(-450, -5) * mm});
            skLineSegment(sketch, "E101", {"start": v(-450, -5) * mm, "end": v(-450, 5) * mm});
            skLineSegment(sketch, "E102", {"start": v(-450, 5) * mm, "end": v(-453, 5) * mm});
            skLineSegment(sketch, "E103", {"start": v(-453, 5) * mm, "end": v(-453, 9) * mm});
            skPoint(sketch, "E104.orphan", {"position": v(-450, 9) * mm});
            skPoint(sketch, "E105.orphan", {"position": v(-450, -9) * mm});
            skLineSegment(sketch, "E106", {"start": v(-680, 9) * mm, "end": v(-680, 5) * mm});
            skLineSegment(sketch, "E107", {"start": v(-680, 5) * mm, "end": v(-683, 5) * mm});
            skLineSegment(sketch, "E108", {"start": v(-683, 5) * mm, "end": v(-683, -5) * mm});
            skLineSegment(sketch, "E109", {"start": v(-683, -5) * mm, "end": v(-680, -5) * mm});
            skLineSegment(sketch, "E110", {"start": v(-680, -5) * mm, "end": v(-680, -9) * mm});
            skLineSegment(sketch, "E111.bottom", {"start": v(-657.4, 4.8) * mm, "end": v(-660, 4.8) * mm});
            skLineSegment(sketch, "E111.top", {"start": v(-657.4, -4.8) * mm, "end": v(-660, -4.8) * mm});
            skLineSegment(sketch, "E111.left", {"start": v(-657.4, 4.8) * mm, "end": v(-657.4, -4.8) * mm});
            skLineSegment(sketch, "E111.right", {"start": v(-660, 4.8) * mm, "end": v(-660, -4.8) * mm});
            skPoint(sketch, "E111.middle", {"position": v(-658.7, 0) * mm});
            skPoint(sketch, "E112.1.0.0", {"position": v(-635.65, 0) * mm});
            skLineSegment(sketch, "E112.1.0.1", {"start": v(-634.35, 4.8) * mm, "end": v(-634.35, -4.8) * mm});
            skLineSegment(sketch, "E112.1.0.2", {"start": v(-636.95, 4.8) * mm, "end": v(-636.95, -4.8) * mm});
            skLineSegment(sketch, "E112.1.0.3", {"start": v(-634.35, -4.8) * mm, "end": v(-636.95, -4.8) * mm});
            skLineSegment(sketch, "E112.1.0.4", {"start": v(-634.35, 4.8) * mm, "end": v(-636.95, 4.8) * mm});
            skPoint(sketch, "E112.2.0.0", {"position": v(-612.6, 0) * mm});
            skLineSegment(sketch, "E112.2.0.1", {"start": v(-611.3, 4.8) * mm, "end": v(-611.3, -4.8) * mm});
            skLineSegment(sketch, "E112.2.0.2", {"start": v(-613.9, 4.8) * mm, "end": v(-613.9, -4.8) * mm});
            skLineSegment(sketch, "E112.2.0.3", {"start": v(-611.3, -4.8) * mm, "end": v(-613.9, -4.8) * mm});
            skLineSegment(sketch, "E112.2.0.4", {"start": v(-611.3, 4.8) * mm, "end": v(-613.9, 4.8) * mm});
            skPoint(sketch, "E112.3.0.0", {"position": v(-589.55, 0) * mm});
            skLineSegment(sketch, "E112.3.0.1", {"start": v(-588.25, 4.8) * mm, "end": v(-588.25, -4.8) * mm});
            skLineSegment(sketch, "E112.3.0.2", {"start": v(-590.85, 4.8) * mm, "end": v(-590.85, -4.8) * mm});
            skLineSegment(sketch, "E112.3.0.3", {"start": v(-588.25, -4.8) * mm, "end": v(-590.85, -4.8) * mm});
            skLineSegment(sketch, "E112.3.0.4", {"start": v(-588.25, 4.8) * mm, "end": v(-590.85, 4.8) * mm});
            skPoint(sketch, "E112.4.0.0", {"position": v(-566.5, 0) * mm});
            skLineSegment(sketch, "E112.4.0.1", {"start": v(-565.2, 4.8) * mm, "end": v(-565.2, -4.8) * mm});
            skLineSegment(sketch, "E112.4.0.2", {"start": v(-567.8, 4.8) * mm, "end": v(-567.8, -4.8) * mm});
            skLineSegment(sketch, "E112.4.0.3", {"start": v(-565.2, -4.8) * mm, "end": v(-567.8, -4.8) * mm});
            skLineSegment(sketch, "E112.4.0.4", {"start": v(-565.2, 4.8) * mm, "end": v(-567.8, 4.8) * mm});
            skPoint(sketch, "E112.5.0.0", {"position": v(-543.45, 0) * mm});
            skLineSegment(sketch, "E112.5.0.1", {"start": v(-542.15, 4.8) * mm, "end": v(-542.15, -4.8) * mm});
            skLineSegment(sketch, "E112.5.0.2", {"start": v(-544.75, 4.8) * mm, "end": v(-544.75, -4.8) * mm});
            skLineSegment(sketch, "E112.5.0.3", {"start": v(-542.15, -4.8) * mm, "end": v(-544.75, -4.8) * mm});
            skLineSegment(sketch, "E112.5.0.4", {"start": v(-542.15, 4.8) * mm, "end": v(-544.75, 4.8) * mm});
            skPoint(sketch, "E112.6.0.0", {"position": v(-520.4, 0) * mm});
            skLineSegment(sketch, "E112.6.0.1", {"start": v(-519.1, 4.8) * mm, "end": v(-519.1, -4.8) * mm});
            skLineSegment(sketch, "E112.6.0.2", {"start": v(-521.7, 4.8) * mm, "end": v(-521.7, -4.8) * mm});
            skLineSegment(sketch, "E112.6.0.3", {"start": v(-519.1, -4.8) * mm, "end": v(-521.7, -4.8) * mm});
            skLineSegment(sketch, "E112.6.0.4", {"start": v(-519.1, 4.8) * mm, "end": v(-521.7, 4.8) * mm});
            skPoint(sketch, "E112.7.0.0", {"position": v(-497.35, 0) * mm});
            skLineSegment(sketch, "E112.7.0.1", {"start": v(-496.05, 4.8) * mm, "end": v(-496.05, -4.8) * mm});
            skLineSegment(sketch, "E112.7.0.2", {"start": v(-498.65, 4.8) * mm, "end": v(-498.65, -4.8) * mm});
            skLineSegment(sketch, "E112.7.0.3", {"start": v(-496.05, -4.8) * mm, "end": v(-498.65, -4.8) * mm});
            skLineSegment(sketch, "E112.7.0.4", {"start": v(-496.05, 4.8) * mm, "end": v(-498.65, 4.8) * mm});
            skPoint(sketch, "E112.8.0.0", {"position": v(-474.3, 0) * mm});
            skLineSegment(sketch, "E112.8.0.1", {"start": v(-473, 4.8) * mm, "end": v(-473, -4.8) * mm});
            skLineSegment(sketch, "E112.8.0.2", {"start": v(-475.6, 4.8) * mm, "end": v(-475.6, -4.8) * mm});
            skLineSegment(sketch, "E112.8.0.3", {"start": v(-473, -4.8) * mm, "end": v(-475.6, -4.8) * mm});
            skLineSegment(sketch, "E112.8.0.4", {"start": v(-473, 4.8) * mm, "end": v(-475.6, 4.8) * mm});
            skLineSegment(sketch, "E112.direction1", {"start": v(-660, -4.8) * mm, "end": v(-636.95, -4.8) * mm, "construction": true});
            skLineSegment(sketch, "E113", {"start": v(-913, -59) * mm, "end": v(-913, -63.2) * mm});
            skLineSegment(sketch, "E114", {"start": v(-913, -63.2) * mm, "end": v(-910, -63.2) * mm});
            skLineSegment(sketch, "E115", {"start": v(-910, -63.2) * mm, "end": v(-910, -72.8) * mm});
            skLineSegment(sketch, "E116", {"start": v(-910, -72.8) * mm, "end": v(-913, -72.8) * mm});
            skLineSegment(sketch, "E117", {"start": v(-913, -72.8) * mm, "end": v(-913, -77) * mm});
            skLineSegment(sketch, "E118", {"start": v(-913, -77) * mm, "end": v(-450, -77) * mm});
            skLineSegment(sketch, "E119", {"start": v(-450, -77) * mm, "end": v(-450, -72.8) * mm});
            skLineSegment(sketch, "E120", {"start": v(-450, -72.8) * mm, "end": v(-453, -72.8) * mm});
            skLineSegment(sketch, "E121", {"start": v(-453, -72.8) * mm, "end": v(-453, -63.2) * mm});
            skLineSegment(sketch, "E122", {"start": v(-453, -63.2) * mm, "end": v(-450, -63.2) * mm});
            skLineSegment(sketch, "E123", {"start": v(-450, -63.2) * mm, "end": v(-450, -59) * mm});
            skLineSegment(sketch, "E124", {"start": v(-450, -59) * mm, "end": v(-913, -59) * mm});
            skLineSegment(sketch, "E125.bottom", {"start": v(-890, -63.2) * mm, "end": v(-887.4, -63.2) * mm});
            skLineSegment(sketch, "E125.top", {"start": v(-890, -72.8) * mm, "end": v(-887.4, -72.8) * mm});
            skLineSegment(sketch, "E125.left", {"start": v(-890, -63.2) * mm, "end": v(-890, -72.8) * mm});
            skLineSegment(sketch, "E125.right", {"start": v(-887.4, -63.2) * mm, "end": v(-887.4, -72.8) * mm});
            skPoint(sketch, "E125.middle", {"position": v(-888.7, -68) * mm});
            skPoint(sketch, "E125.middle.positionSnap0", {"position": v(-910, -68) * mm});
            skPoint(sketch, "E125.centerSnap0", {"position": v(-910, -68) * mm});
            skLineSegment(sketch, "E126.1.0.0", {"start": v(-866.98, -72.8) * mm, "end": v(-864.38, -72.8) * mm});
            skLineSegment(sketch, "E126.1.0.1", {"start": v(-866.98, -63.2) * mm, "end": v(-864.38, -63.2) * mm});
            skPoint(sketch, "E126.1.0.2", {"position": v(-865.68, -68) * mm});
            skLineSegment(sketch, "E126.1.0.3", {"start": v(-866.98, -63.2) * mm, "end": v(-866.98, -72.8) * mm});
            skLineSegment(sketch, "E126.1.0.4", {"start": v(-864.38, -63.2) * mm, "end": v(-864.38, -72.8) * mm});
            skLineSegment(sketch, "E126.2.0.0", {"start": v(-843.96, -72.8) * mm, "end": v(-841.36, -72.8) * mm});
            skLineSegment(sketch, "E126.2.0.1", {"start": v(-843.96, -63.2) * mm, "end": v(-841.36, -63.2) * mm});
            skPoint(sketch, "E126.2.0.2", {"position": v(-842.66, -68) * mm});
            skLineSegment(sketch, "E126.2.0.3", {"start": v(-843.96, -63.2) * mm, "end": v(-843.96, -72.8) * mm});
            skLineSegment(sketch, "E126.2.0.4", {"start": v(-841.36, -63.2) * mm, "end": v(-841.36, -72.8) * mm});
            skLineSegment(sketch, "E126.3.0.0", {"start": v(-820.93, -72.8) * mm, "end": v(-818.33, -72.8) * mm});
            skLineSegment(sketch, "E126.3.0.1", {"start": v(-820.93, -63.2) * mm, "end": v(-818.33, -63.2) * mm});
            skPoint(sketch, "E126.3.0.2", {"position": v(-819.63, -68) * mm});
            skLineSegment(sketch, "E126.3.0.3", {"start": v(-820.93, -63.2) * mm, "end": v(-820.93, -72.8) * mm});
            skLineSegment(sketch, "E126.3.0.4", {"start": v(-818.33, -63.2) * mm, "end": v(-818.33, -72.8) * mm});
            skLineSegment(sketch, "E126.4.0.0", {"start": v(-797.91, -72.8) * mm, "end": v(-795.31, -72.8) * mm});
            skLineSegment(sketch, "E126.4.0.1", {"start": v(-797.91, -63.2) * mm, "end": v(-795.31, -63.2) * mm});
            skPoint(sketch, "E126.4.0.2", {"position": v(-796.61, -68) * mm});
            skLineSegment(sketch, "E126.4.0.3", {"start": v(-797.91, -63.2) * mm, "end": v(-797.91, -72.8) * mm});
            skLineSegment(sketch, "E126.4.0.4", {"start": v(-795.31, -63.2) * mm, "end": v(-795.31, -72.8) * mm});
            skLineSegment(sketch, "E126.5.0.0", {"start": v(-774.89, -72.8) * mm, "end": v(-772.29, -72.8) * mm});
            skLineSegment(sketch, "E126.5.0.1", {"start": v(-774.89, -63.2) * mm, "end": v(-772.29, -63.2) * mm});
            skPoint(sketch, "E126.5.0.2", {"position": v(-773.59, -68) * mm});
            skLineSegment(sketch, "E126.5.0.3", {"start": v(-774.89, -63.2) * mm, "end": v(-774.89, -72.8) * mm});
            skLineSegment(sketch, "E126.5.0.4", {"start": v(-772.29, -63.2) * mm, "end": v(-772.29, -72.8) * mm});
            skLineSegment(sketch, "E126.6.0.0", {"start": v(-751.87, -72.8) * mm, "end": v(-749.27, -72.8) * mm});
            skLineSegment(sketch, "E126.6.0.1", {"start": v(-751.87, -63.2) * mm, "end": v(-749.27, -63.2) * mm});
            skPoint(sketch, "E126.6.0.2", {"position": v(-750.57, -68) * mm});
            skLineSegment(sketch, "E126.6.0.3", {"start": v(-751.87, -63.2) * mm, "end": v(-751.87, -72.8) * mm});
            skLineSegment(sketch, "E126.6.0.4", {"start": v(-749.27, -63.2) * mm, "end": v(-749.27, -72.8) * mm});
            skLineSegment(sketch, "E126.7.0.0", {"start": v(-728.84, -72.8) * mm, "end": v(-726.24, -72.8) * mm});
            skLineSegment(sketch, "E126.7.0.1", {"start": v(-728.84, -63.2) * mm, "end": v(-726.24, -63.2) * mm});
            skPoint(sketch, "E126.7.0.2", {"position": v(-727.54, -68) * mm});
            skLineSegment(sketch, "E126.7.0.3", {"start": v(-728.84, -63.2) * mm, "end": v(-728.84, -72.8) * mm});
            skLineSegment(sketch, "E126.7.0.4", {"start": v(-726.24, -63.2) * mm, "end": v(-726.24, -72.8) * mm});
            skLineSegment(sketch, "E126.8.0.0", {"start": v(-705.82, -72.8) * mm, "end": v(-703.22, -72.8) * mm});
            skLineSegment(sketch, "E126.8.0.1", {"start": v(-705.82, -63.2) * mm, "end": v(-703.22, -63.2) * mm});
            skPoint(sketch, "E126.8.0.2", {"position": v(-704.52, -68) * mm});
            skLineSegment(sketch, "E126.8.0.3", {"start": v(-705.82, -63.2) * mm, "end": v(-705.82, -72.8) * mm});
            skLineSegment(sketch, "E126.8.0.4", {"start": v(-703.22, -63.2) * mm, "end": v(-703.22, -72.8) * mm});
            skLineSegment(sketch, "E126.9.0.0", {"start": v(-682.8, -72.8) * mm, "end": v(-680.2, -72.8) * mm});
            skLineSegment(sketch, "E126.9.0.1", {"start": v(-682.8, -63.2) * mm, "end": v(-680.2, -63.2) * mm});
            skPoint(sketch, "E126.9.0.2", {"position": v(-681.5, -68) * mm});
            skLineSegment(sketch, "E126.9.0.3", {"start": v(-682.8, -63.2) * mm, "end": v(-682.8, -72.8) * mm});
            skLineSegment(sketch, "E126.9.0.4", {"start": v(-680.2, -63.2) * mm, "end": v(-680.2, -72.8) * mm});
            skLineSegment(sketch, "E126.10.0.0", {"start": v(-659.78, -72.8) * mm, "end": v(-657.18, -72.8) * mm});
            skLineSegment(sketch, "E126.10.0.1", {"start": v(-659.78, -63.2) * mm, "end": v(-657.18, -63.2) * mm});
            skPoint(sketch, "E126.10.0.2", {"position": v(-658.48, -68) * mm});
            skLineSegment(sketch, "E126.10.0.3", {"start": v(-659.78, -63.2) * mm, "end": v(-659.78, -72.8) * mm});
            skLineSegment(sketch, "E126.10.0.4", {"start": v(-657.18, -63.2) * mm, "end": v(-657.18, -72.8) * mm});
            skLineSegment(sketch, "E126.11.0.0", {"start": v(-636.76, -72.8) * mm, "end": v(-634.16, -72.8) * mm});
            skLineSegment(sketch, "E126.11.0.1", {"start": v(-636.76, -63.2) * mm, "end": v(-634.16, -63.2) * mm});
            skPoint(sketch, "E126.11.0.2", {"position": v(-635.46, -68) * mm});
            skLineSegment(sketch, "E126.11.0.3", {"start": v(-636.76, -63.2) * mm, "end": v(-636.76, -72.8) * mm});
            skLineSegment(sketch, "E126.11.0.4", {"start": v(-634.16, -63.2) * mm, "end": v(-634.16, -72.8) * mm});
            skLineSegment(sketch, "E126.12.0.0", {"start": v(-613.73, -72.8) * mm, "end": v(-611.13, -72.8) * mm});
            skLineSegment(sketch, "E126.12.0.1", {"start": v(-613.73, -63.2) * mm, "end": v(-611.13, -63.2) * mm});
            skPoint(sketch, "E126.12.0.2", {"position": v(-612.43, -68) * mm});
            skLineSegment(sketch, "E126.12.0.3", {"start": v(-613.73, -63.2) * mm, "end": v(-613.73, -72.8) * mm});
            skLineSegment(sketch, "E126.12.0.4", {"start": v(-611.13, -63.2) * mm, "end": v(-611.13, -72.8) * mm});
            skLineSegment(sketch, "E126.13.0.0", {"start": v(-590.71, -72.8) * mm, "end": v(-588.11, -72.8) * mm});
            skLineSegment(sketch, "E126.13.0.1", {"start": v(-590.71, -63.2) * mm, "end": v(-588.11, -63.2) * mm});
            skPoint(sketch, "E126.13.0.2", {"position": v(-589.41, -68) * mm});
            skLineSegment(sketch, "E126.13.0.3", {"start": v(-590.71, -63.2) * mm, "end": v(-590.71, -72.8) * mm});
            skLineSegment(sketch, "E126.13.0.4", {"start": v(-588.11, -63.2) * mm, "end": v(-588.11, -72.8) * mm});
            skLineSegment(sketch, "E126.14.0.0", {"start": v(-567.69, -72.8) * mm, "end": v(-565.09, -72.8) * mm});
            skLineSegment(sketch, "E126.14.0.1", {"start": v(-567.69, -63.2) * mm, "end": v(-565.09, -63.2) * mm});
            skPoint(sketch, "E126.14.0.2", {"position": v(-566.39, -68) * mm});
            skLineSegment(sketch, "E126.14.0.3", {"start": v(-567.69, -63.2) * mm, "end": v(-567.69, -72.8) * mm});
            skLineSegment(sketch, "E126.14.0.4", {"start": v(-565.09, -63.2) * mm, "end": v(-565.09, -72.8) * mm});
            skLineSegment(sketch, "E126.15.0.0", {"start": v(-544.67, -72.8) * mm, "end": v(-542.07, -72.8) * mm});
            skLineSegment(sketch, "E126.15.0.1", {"start": v(-544.67, -63.2) * mm, "end": v(-542.07, -63.2) * mm});
            skPoint(sketch, "E126.15.0.2", {"position": v(-543.37, -68) * mm});
            skLineSegment(sketch, "E126.15.0.3", {"start": v(-544.67, -63.2) * mm, "end": v(-544.67, -72.8) * mm});
            skLineSegment(sketch, "E126.15.0.4", {"start": v(-542.07, -63.2) * mm, "end": v(-542.07, -72.8) * mm});
            skLineSegment(sketch, "E126.16.0.0", {"start": v(-521.64, -72.8) * mm, "end": v(-519.04, -72.8) * mm});
            skLineSegment(sketch, "E126.16.0.1", {"start": v(-521.64, -63.2) * mm, "end": v(-519.04, -63.2) * mm});
            skPoint(sketch, "E126.16.0.2", {"position": v(-520.34, -68) * mm});
            skLineSegment(sketch, "E126.16.0.3", {"start": v(-521.64, -63.2) * mm, "end": v(-521.64, -72.8) * mm});
            skLineSegment(sketch, "E126.16.0.4", {"start": v(-519.04, -63.2) * mm, "end": v(-519.04, -72.8) * mm});
            skLineSegment(sketch, "E126.17.0.0", {"start": v(-498.62, -72.8) * mm, "end": v(-496.02, -72.8) * mm});
            skLineSegment(sketch, "E126.17.0.1", {"start": v(-498.62, -63.2) * mm, "end": v(-496.02, -63.2) * mm});
            skPoint(sketch, "E126.17.0.2", {"position": v(-497.32, -68) * mm});
            skLineSegment(sketch, "E126.17.0.3", {"start": v(-498.62, -63.2) * mm, "end": v(-498.62, -72.8) * mm});
            skLineSegment(sketch, "E126.17.0.4", {"start": v(-496.02, -63.2) * mm, "end": v(-496.02, -72.8) * mm});
            skLineSegment(sketch, "E126.18.0.0", {"start": v(-475.6, -72.8) * mm, "end": v(-473, -72.8) * mm});
            skLineSegment(sketch, "E126.18.0.1", {"start": v(-475.6, -63.2) * mm, "end": v(-473, -63.2) * mm});
            skPoint(sketch, "E126.18.0.2", {"position": v(-474.3, -68) * mm});
            skLineSegment(sketch, "E126.18.0.3", {"start": v(-475.6, -63.2) * mm, "end": v(-475.6, -72.8) * mm});
            skLineSegment(sketch, "E126.18.0.4", {"start": v(-473, -63.2) * mm, "end": v(-473, -72.8) * mm});
            skLineSegment(sketch, "E126.direction1", {"start": v(-890, -72.8) * mm, "end": v(-866.98, -72.8) * mm, "construction": true});
            skLineSegment(sketch, "E127", {"start": v(-453, 59) * mm, "end": v(-680, 59) * mm});
            skLineSegment(sketch, "E128", {"start": v(-680, 59) * mm, "end": v(-680, 63) * mm});
            skLineSegment(sketch, "E129", {"start": v(-680, 63) * mm, "end": v(-683, 63) * mm});
            skLineSegment(sketch, "E130", {"start": v(-683, 63) * mm, "end": v(-683, 73) * mm});
            skLineSegment(sketch, "E131", {"start": v(-453, 59) * mm, "end": v(-453, 63) * mm});
            skLineSegment(sketch, "E132", {"start": v(-453, 63) * mm, "end": v(-450, 63) * mm});
            skLineSegment(sketch, "E133", {"start": v(-450, 63) * mm, "end": v(-450, 73) * mm});
            skLineSegment(sketch, "E134", {"start": v(-450, 73) * mm, "end": v(-453, 73) * mm});
            skLineSegment(sketch, "E135", {"start": v(-453, 73) * mm, "end": v(-453, 77) * mm});
            skLineSegment(sketch, "E136", {"start": v(-683, 73) * mm, "end": v(-680, 73) * mm});
            skLineSegment(sketch, "E137", {"start": v(-680, 73) * mm, "end": v(-680, 77) * mm});
            skLineSegment(sketch, "E138", {"start": v(-680, 77) * mm, "end": v(-660, 77) * mm});
            skLineSegment(sketch, "E139", {"start": v(-660, 77) * mm, "end": v(-660, 67.4) * mm});
            skLineSegment(sketch, "E140", {"start": v(-660, 67.4) * mm, "end": v(-657, 67.4) * mm});
            skLineSegment(sketch, "E141", {"start": v(-657, 67.4) * mm, "end": v(-657, 77) * mm});
            skLineSegment(sketch, "E142", {"start": v(-657, 77) * mm, "end": v(-637, 77) * mm});
            skLineSegment(sketch, "E143.1.0.0", {"start": v(-634, 77) * mm, "end": v(-614, 77) * mm});
            skLineSegment(sketch, "E143.1.0.2", {"start": v(-637, 77) * mm, "end": v(-637, 67.4) * mm});
            skLineSegment(sketch, "E143.1.0.3", {"start": v(-634, 67.4) * mm, "end": v(-634, 77) * mm});
            skLineSegment(sketch, "E143.1.0.4", {"start": v(-637, 67.4) * mm, "end": v(-634, 67.4) * mm});
            skLineSegment(sketch, "E143.2.0.0", {"start": v(-611, 77) * mm, "end": v(-591, 77) * mm});
            skLineSegment(sketch, "E143.2.0.1", {"start": v(-634, 77) * mm, "end": v(-614, 77) * mm});
            skLineSegment(sketch, "E143.2.0.2", {"start": v(-614, 77) * mm, "end": v(-614, 67.4) * mm});
            skLineSegment(sketch, "E143.2.0.3", {"start": v(-611, 67.4) * mm, "end": v(-611, 77) * mm});
            skLineSegment(sketch, "E143.2.0.4", {"start": v(-614, 67.4) * mm, "end": v(-611, 67.4) * mm});
            skLineSegment(sketch, "E143.3.0.0", {"start": v(-588, 77) * mm, "end": v(-568, 77) * mm});
            skLineSegment(sketch, "E143.3.0.1", {"start": v(-611, 77) * mm, "end": v(-591, 77) * mm});
            skLineSegment(sketch, "E143.3.0.2", {"start": v(-591, 77) * mm, "end": v(-591, 67.4) * mm});
            skLineSegment(sketch, "E143.3.0.3", {"start": v(-588, 67.4) * mm, "end": v(-588, 77) * mm});
            skLineSegment(sketch, "E143.3.0.4", {"start": v(-591, 67.4) * mm, "end": v(-588, 67.4) * mm});
            skLineSegment(sketch, "E143.4.0.0", {"start": v(-565, 77) * mm, "end": v(-545, 77) * mm});
            skLineSegment(sketch, "E143.4.0.1", {"start": v(-588, 77) * mm, "end": v(-568, 77) * mm});
            skLineSegment(sketch, "E143.4.0.2", {"start": v(-568, 77) * mm, "end": v(-568, 67.4) * mm});
            skLineSegment(sketch, "E143.4.0.3", {"start": v(-565, 67.4) * mm, "end": v(-565, 77) * mm});
            skLineSegment(sketch, "E143.4.0.4", {"start": v(-568, 67.4) * mm, "end": v(-565, 67.4) * mm});
            skLineSegment(sketch, "E143.5.0.0", {"start": v(-542, 77) * mm, "end": v(-522, 77) * mm});
            skLineSegment(sketch, "E143.5.0.1", {"start": v(-565, 77) * mm, "end": v(-545, 77) * mm});
            skLineSegment(sketch, "E143.5.0.2", {"start": v(-545, 77) * mm, "end": v(-545, 67.4) * mm});
            skLineSegment(sketch, "E143.5.0.3", {"start": v(-542, 67.4) * mm, "end": v(-542, 77) * mm});
            skLineSegment(sketch, "E143.5.0.4", {"start": v(-545, 67.4) * mm, "end": v(-542, 67.4) * mm});
            skLineSegment(sketch, "E143.6.0.0", {"start": v(-519, 77) * mm, "end": v(-499, 77) * mm});
            skLineSegment(sketch, "E143.6.0.1", {"start": v(-542, 77) * mm, "end": v(-522, 77) * mm});
            skLineSegment(sketch, "E143.6.0.2", {"start": v(-522, 77) * mm, "end": v(-522, 67.4) * mm});
            skLineSegment(sketch, "E143.6.0.3", {"start": v(-519, 67.4) * mm, "end": v(-519, 77) * mm});
            skLineSegment(sketch, "E143.6.0.4", {"start": v(-522, 67.4) * mm, "end": v(-519, 67.4) * mm});
            skLineSegment(sketch, "E143.7.0.0", {"start": v(-496, 77) * mm, "end": v(-476, 77) * mm});
            skLineSegment(sketch, "E143.7.0.1", {"start": v(-519, 77) * mm, "end": v(-499, 77) * mm});
            skLineSegment(sketch, "E143.7.0.2", {"start": v(-499, 77) * mm, "end": v(-499, 67.4) * mm});
            skLineSegment(sketch, "E143.7.0.3", {"start": v(-496, 67.4) * mm, "end": v(-496, 77) * mm});
            skLineSegment(sketch, "E143.7.0.4", {"start": v(-499, 67.4) * mm, "end": v(-496, 67.4) * mm});
            skLineSegment(sketch, "E143.8.0.0", {"start": v(-473, 77) * mm, "end": v(-453, 77) * mm});
            skLineSegment(sketch, "E143.8.0.1", {"start": v(-496, 77) * mm, "end": v(-476, 77) * mm});
            skLineSegment(sketch, "E143.8.0.2", {"start": v(-476, 77) * mm, "end": v(-476, 67.4) * mm});
            skLineSegment(sketch, "E143.8.0.3", {"start": v(-473, 67.4) * mm, "end": v(-473, 77) * mm});
            skLineSegment(sketch, "E143.8.0.4", {"start": v(-476, 67.4) * mm, "end": v(-473, 67.4) * mm});
            skLineSegment(sketch, "E143.direction1", {"start": v(-680, 77) * mm, "end": v(-657, 77) * mm, "construction": true});
            skLineSegment(sketch, "E144", {"start": v(-450, -131) * mm, "end": v(-450, -141) * mm});
            skLineSegment(sketch, "E145", {"start": v(-450, -141) * mm, "end": v(-453, -141) * mm});
            skLineSegment(sketch, "E146", {"start": v(-453, -141) * mm, "end": v(-453, -145) * mm});
            skLineSegment(sketch, "E147", {"start": v(-450, -131) * mm, "end": v(-453, -131) * mm});
            skLineSegment(sketch, "E148", {"start": v(-453, -131) * mm, "end": v(-453, -127) * mm});
            skLineSegment(sketch, "E149", {"start": v(-453, -127) * mm, "end": v(-910, -127) * mm});
            skLineSegment(sketch, "E150", {"start": v(-910, -127) * mm, "end": v(-910, -131) * mm});
            skLineSegment(sketch, "E151", {"start": v(-910, -131) * mm, "end": v(-913, -131) * mm});
            skLineSegment(sketch, "E152", {"start": v(-913, -131) * mm, "end": v(-913, -141) * mm});
            skLineSegment(sketch, "E153", {"start": v(-913, -141) * mm, "end": v(-910, -141) * mm});
            skLineSegment(sketch, "E154", {"start": v(-910, -141) * mm, "end": v(-910, -145) * mm});
            skLineSegment(sketch, "E155", {"start": v(-910, -145) * mm, "end": v(-890, -145) * mm});
            skLineSegment(sketch, "E156", {"start": v(-890, -145) * mm, "end": v(-890, -136.6) * mm});
            skLineSegment(sketch, "E157", {"start": v(-890, -136.6) * mm, "end": v(-887, -136.6) * mm});
            skLineSegment(sketch, "E158", {"start": v(-887, -136.6) * mm, "end": v(-887, -145) * mm});
            skLineSegment(sketch, "E159", {"start": v(-887, -145) * mm, "end": v(-867, -145) * mm});
            skLineSegment(sketch, "E160.1.0.1", {"start": v(-867, -145) * mm, "end": v(-867, -136.6) * mm});
            skLineSegment(sketch, "E160.1.0.2", {"start": v(-864, -145) * mm, "end": v(-844, -145) * mm});
            skLineSegment(sketch, "E160.1.0.3", {"start": v(-864, -136.6) * mm, "end": v(-864, -145) * mm});
            skLineSegment(sketch, "E160.1.0.4", {"start": v(-867, -136.6) * mm, "end": v(-864, -136.6) * mm});
            skLineSegment(sketch, "E160.2.0.0", {"start": v(-864, -145) * mm, "end": v(-844, -145) * mm});
            skLineSegment(sketch, "E160.2.0.1", {"start": v(-844, -145) * mm, "end": v(-844, -136.6) * mm});
            skLineSegment(sketch, "E160.2.0.2", {"start": v(-841, -145) * mm, "end": v(-821, -145) * mm});
            skLineSegment(sketch, "E160.2.0.3", {"start": v(-841, -136.6) * mm, "end": v(-841, -145) * mm});
            skLineSegment(sketch, "E160.2.0.4", {"start": v(-844, -136.6) * mm, "end": v(-841, -136.6) * mm});
            skLineSegment(sketch, "E160.3.0.0", {"start": v(-841, -145) * mm, "end": v(-821, -145) * mm});
            skLineSegment(sketch, "E160.3.0.1", {"start": v(-821, -145) * mm, "end": v(-821, -136.6) * mm});
            skLineSegment(sketch, "E160.3.0.2", {"start": v(-818, -145) * mm, "end": v(-798, -145) * mm});
            skLineSegment(sketch, "E160.3.0.3", {"start": v(-818, -136.6) * mm, "end": v(-818, -145) * mm});
            skLineSegment(sketch, "E160.3.0.4", {"start": v(-821, -136.6) * mm, "end": v(-818, -136.6) * mm});
            skLineSegment(sketch, "E160.4.0.0", {"start": v(-818, -145) * mm, "end": v(-798, -145) * mm});
            skLineSegment(sketch, "E160.4.0.1", {"start": v(-798, -145) * mm, "end": v(-798, -136.6) * mm});
            skLineSegment(sketch, "E160.4.0.2", {"start": v(-795, -145) * mm, "end": v(-775, -145) * mm});
            skLineSegment(sketch, "E160.4.0.3", {"start": v(-795, -136.6) * mm, "end": v(-795, -145) * mm});
            skLineSegment(sketch, "E160.4.0.4", {"start": v(-798, -136.6) * mm, "end": v(-795, -136.6) * mm});
            skLineSegment(sketch, "E160.5.0.0", {"start": v(-795, -145) * mm, "end": v(-775, -145) * mm});
            skLineSegment(sketch, "E160.5.0.1", {"start": v(-775, -145) * mm, "end": v(-775, -136.6) * mm});
            skLineSegment(sketch, "E160.5.0.2", {"start": v(-772, -145) * mm, "end": v(-752, -145) * mm});
            skLineSegment(sketch, "E160.5.0.3", {"start": v(-772, -136.6) * mm, "end": v(-772, -145) * mm});
            skLineSegment(sketch, "E160.5.0.4", {"start": v(-775, -136.6) * mm, "end": v(-772, -136.6) * mm});
            skLineSegment(sketch, "E160.6.0.0", {"start": v(-772, -145) * mm, "end": v(-752, -145) * mm});
            skLineSegment(sketch, "E160.6.0.1", {"start": v(-752, -145) * mm, "end": v(-752, -136.6) * mm});
            skLineSegment(sketch, "E160.6.0.2", {"start": v(-749, -145) * mm, "end": v(-729, -145) * mm});
            skLineSegment(sketch, "E160.6.0.3", {"start": v(-749, -136.6) * mm, "end": v(-749, -145) * mm});
            skLineSegment(sketch, "E160.6.0.4", {"start": v(-752, -136.6) * mm, "end": v(-749, -136.6) * mm});
            skLineSegment(sketch, "E160.7.0.0", {"start": v(-749, -145) * mm, "end": v(-729, -145) * mm});
            skLineSegment(sketch, "E160.7.0.1", {"start": v(-729, -145) * mm, "end": v(-729, -136.6) * mm});
            skLineSegment(sketch, "E160.7.0.2", {"start": v(-726, -145) * mm, "end": v(-706, -145) * mm});
            skLineSegment(sketch, "E160.7.0.3", {"start": v(-726, -136.6) * mm, "end": v(-726, -145) * mm});
            skLineSegment(sketch, "E160.7.0.4", {"start": v(-729, -136.6) * mm, "end": v(-726, -136.6) * mm});
            skLineSegment(sketch, "E160.8.0.0", {"start": v(-726, -145) * mm, "end": v(-706, -145) * mm});
            skLineSegment(sketch, "E160.8.0.1", {"start": v(-706, -145) * mm, "end": v(-706, -136.6) * mm});
            skLineSegment(sketch, "E160.8.0.2", {"start": v(-703, -145) * mm, "end": v(-683, -145) * mm});
            skLineSegment(sketch, "E160.8.0.3", {"start": v(-703, -136.6) * mm, "end": v(-703, -145) * mm});
            skLineSegment(sketch, "E160.8.0.4", {"start": v(-706, -136.6) * mm, "end": v(-703, -136.6) * mm});
            skLineSegment(sketch, "E160.9.0.0", {"start": v(-703, -145) * mm, "end": v(-683, -145) * mm});
            skLineSegment(sketch, "E160.9.0.1", {"start": v(-683, -145) * mm, "end": v(-683, -136.6) * mm});
            skLineSegment(sketch, "E160.9.0.2", {"start": v(-680, -145) * mm, "end": v(-660, -145) * mm});
            skLineSegment(sketch, "E160.9.0.3", {"start": v(-680, -136.6) * mm, "end": v(-680, -145) * mm});
            skLineSegment(sketch, "E160.9.0.4", {"start": v(-683, -136.6) * mm, "end": v(-680, -136.6) * mm});
            skLineSegment(sketch, "E160.10.0.0", {"start": v(-680, -145) * mm, "end": v(-660, -145) * mm});
            skLineSegment(sketch, "E160.10.0.1", {"start": v(-660, -145) * mm, "end": v(-660, -136.6) * mm});
            skLineSegment(sketch, "E160.10.0.2", {"start": v(-657, -145) * mm, "end": v(-637, -145) * mm});
            skLineSegment(sketch, "E160.10.0.3", {"start": v(-657, -136.6) * mm, "end": v(-657, -145) * mm});
            skLineSegment(sketch, "E160.10.0.4", {"start": v(-660, -136.6) * mm, "end": v(-657, -136.6) * mm});
            skLineSegment(sketch, "E160.11.0.0", {"start": v(-657, -145) * mm, "end": v(-637, -145) * mm});
            skLineSegment(sketch, "E160.11.0.1", {"start": v(-637, -145) * mm, "end": v(-637, -136.6) * mm});
            skLineSegment(sketch, "E160.11.0.2", {"start": v(-634, -145) * mm, "end": v(-614, -145) * mm});
            skLineSegment(sketch, "E160.11.0.3", {"start": v(-634, -136.6) * mm, "end": v(-634, -145) * mm});
            skLineSegment(sketch, "E160.11.0.4", {"start": v(-637, -136.6) * mm, "end": v(-634, -136.6) * mm});
            skLineSegment(sketch, "E160.12.0.0", {"start": v(-634, -145) * mm, "end": v(-614, -145) * mm});
            skLineSegment(sketch, "E160.12.0.1", {"start": v(-614, -145) * mm, "end": v(-614, -136.6) * mm});
            skLineSegment(sketch, "E160.12.0.2", {"start": v(-611, -145) * mm, "end": v(-591, -145) * mm});
            skLineSegment(sketch, "E160.12.0.3", {"start": v(-611, -136.6) * mm, "end": v(-611, -145) * mm});
            skLineSegment(sketch, "E160.12.0.4", {"start": v(-614, -136.6) * mm, "end": v(-611, -136.6) * mm});
            skLineSegment(sketch, "E160.13.0.0", {"start": v(-611, -145) * mm, "end": v(-591, -145) * mm});
            skLineSegment(sketch, "E160.13.0.1", {"start": v(-591, -145) * mm, "end": v(-591, -136.6) * mm});
            skLineSegment(sketch, "E160.13.0.2", {"start": v(-588, -145) * mm, "end": v(-568, -145) * mm});
            skLineSegment(sketch, "E160.13.0.3", {"start": v(-588, -136.6) * mm, "end": v(-588, -145) * mm});
            skLineSegment(sketch, "E160.13.0.4", {"start": v(-591, -136.6) * mm, "end": v(-588, -136.6) * mm});
            skLineSegment(sketch, "E160.14.0.0", {"start": v(-588, -145) * mm, "end": v(-568, -145) * mm});
            skLineSegment(sketch, "E160.14.0.1", {"start": v(-568, -145) * mm, "end": v(-568, -136.6) * mm});
            skLineSegment(sketch, "E160.14.0.2", {"start": v(-565, -145) * mm, "end": v(-545, -145) * mm});
            skLineSegment(sketch, "E160.14.0.3", {"start": v(-565, -136.6) * mm, "end": v(-565, -145) * mm});
            skLineSegment(sketch, "E160.14.0.4", {"start": v(-568, -136.6) * mm, "end": v(-565, -136.6) * mm});
            skLineSegment(sketch, "E160.15.0.0", {"start": v(-565, -145) * mm, "end": v(-545, -145) * mm});
            skLineSegment(sketch, "E160.15.0.1", {"start": v(-545, -145) * mm, "end": v(-545, -136.6) * mm});
            skLineSegment(sketch, "E160.15.0.2", {"start": v(-542, -145) * mm, "end": v(-522, -145) * mm});
            skLineSegment(sketch, "E160.15.0.3", {"start": v(-542, -136.6) * mm, "end": v(-542, -145) * mm});
            skLineSegment(sketch, "E160.15.0.4", {"start": v(-545, -136.6) * mm, "end": v(-542, -136.6) * mm});
            skLineSegment(sketch, "E160.16.0.0", {"start": v(-542, -145) * mm, "end": v(-522, -145) * mm});
            skLineSegment(sketch, "E160.16.0.1", {"start": v(-522, -145) * mm, "end": v(-522, -136.6) * mm});
            skLineSegment(sketch, "E160.16.0.2", {"start": v(-519, -145) * mm, "end": v(-499, -145) * mm});
            skLineSegment(sketch, "E160.16.0.3", {"start": v(-519, -136.6) * mm, "end": v(-519, -145) * mm});
            skLineSegment(sketch, "E160.16.0.4", {"start": v(-522, -136.6) * mm, "end": v(-519, -136.6) * mm});
            skLineSegment(sketch, "E160.17.0.0", {"start": v(-519, -145) * mm, "end": v(-499, -145) * mm});
            skLineSegment(sketch, "E160.17.0.1", {"start": v(-499, -145) * mm, "end": v(-499, -136.6) * mm});
            skLineSegment(sketch, "E160.17.0.2", {"start": v(-496, -145) * mm, "end": v(-476, -145) * mm});
            skLineSegment(sketch, "E160.17.0.3", {"start": v(-496, -136.6) * mm, "end": v(-496, -145) * mm});
            skLineSegment(sketch, "E160.17.0.4", {"start": v(-499, -136.6) * mm, "end": v(-496, -136.6) * mm});
            skLineSegment(sketch, "E160.18.0.0", {"start": v(-496, -145) * mm, "end": v(-476, -145) * mm});
            skLineSegment(sketch, "E160.18.0.1", {"start": v(-476, -145) * mm, "end": v(-476, -136.6) * mm});
            skLineSegment(sketch, "E160.18.0.2", {"start": v(-473, -145) * mm, "end": v(-453, -145) * mm});
            skLineSegment(sketch, "E160.18.0.3", {"start": v(-473, -136.6) * mm, "end": v(-473, -145) * mm});
            skLineSegment(sketch, "E160.18.0.4", {"start": v(-476, -136.6) * mm, "end": v(-473, -136.6) * mm});
            skLineSegment(sketch, "E160.direction1", {"start": v(-910, -145) * mm, "end": v(-887, -145) * mm, "construction": true});
            skSolve(sketch);
        }
        {
            var Q0;
            Q0=makeQuery(id+"F17.imprint","IMPRINT",FACE,{"disambiguationData":[TD([[makeQuery(id+"F17.imprint","IMPRINT",EDGE,{"derivedFrom":sQuery(id+"F17.wireOp",EDGE,"E127")}),-1.0]])]});
            var Q1;
            Q1=makeQuery(id+"F17.imprint","IMPRINT",FACE,{"disambiguationData":[TD([[makeQuery(id+"F17.imprint","IMPRINT",EDGE,{"derivedFrom":sQuery(id+"F17.wireOp",EDGE,"E98.bottom")}),1.0]])]});
            var Q2;
            Q2=makeQuery(id+"F17.imprint","IMPRINT",FACE,{"disambiguationData":[TD([[makeQuery(id+"F17.imprint","IMPRINT",EDGE,{"derivedFrom":sQuery(id+"F17.wireOp",EDGE,"E113")}),1.0]])]});
            var Q3;
            Q3=makeQuery(id+"F17.imprint","IMPRINT",FACE,{"disambiguationData":[TD([[makeQuery(id+"F17.imprint","IMPRINT",EDGE,{"derivedFrom":sQuery(id+"F17.wireOp",EDGE,"E144")}),-1.0]])]});
            extrude(context, id + "F18", {"entities" : qUnion([Q0, Q1, Q2, Q3]), "depth" : (getVariable(context, 'Thickness')) * mm});
        }
    });
